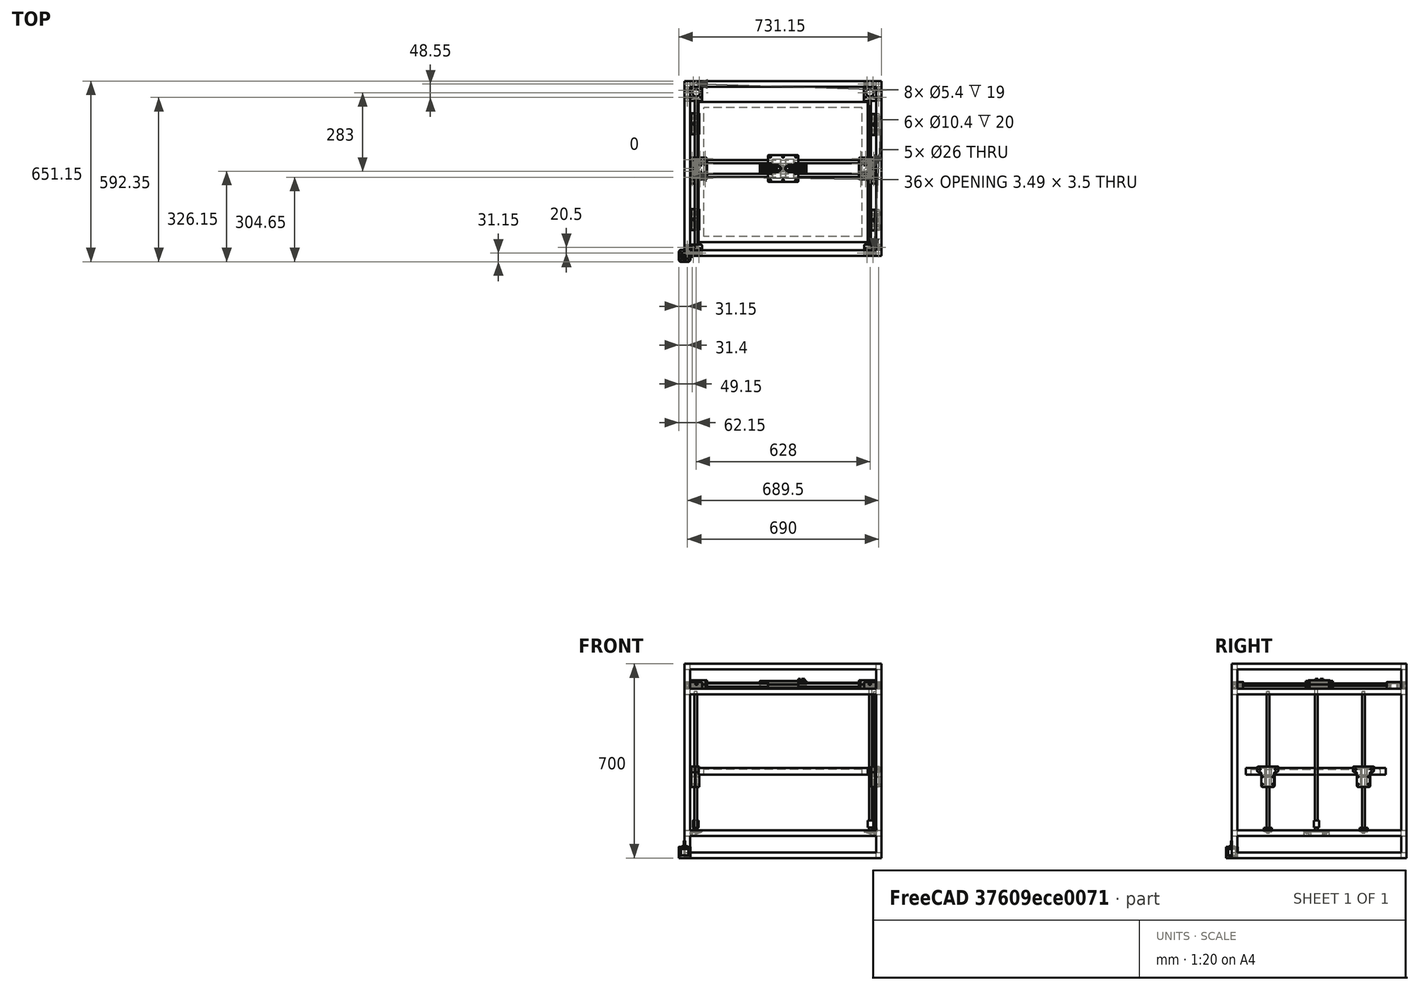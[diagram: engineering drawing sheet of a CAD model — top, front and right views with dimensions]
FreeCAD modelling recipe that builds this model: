
FCSTD DOCUMENT  (FreeCAD 0.17R13541 (Git))
Label: Modelo completo
License: All rights reserved
LicenseURL: http://en.wikipedia.org/wiki/All_rights_reserved
objects: Sketcher::SketchObject×105, Part::Cylinder×96, Part::Box×67, Part::Cut×63, Part::MultiFuse×62, Part::Prism×54, Part::FeaturePython×51, PartDesign::Pad×44, PartDesign::Pocket×44, PartDesign::Body×28, App::Part×28, Part::Fuse×24, Part::Extrusion×17, Part::Common×16, PartDesign::Chamfer×16, Part::Fillet×10, Part::Feature×10, PartDesign::Fillet×8, Part::Chamfer×5, Part::Mirroring×4, +5 more types
note: 832 computed .brp shape members not serialized (recipe doc carries the construction recipe); baked Part::Feature solids carry a one-line shape summary decoded from their .brp

FEATURE [Part::Box] Box  label="Columna"
  AttacherType = Attacher::AttachEngine3D
  Height = 700
  Length = 20
  Width = 20
FEATURE [Part::FeaturePython] Array  label="Columnas"  # Draft array (typed FeaturePython)
  Angle = 360
  ArrayType = 0
  Axis = (0,0,1)
  Base = -> Box
  Center = (0,0,0)
  Fuse = false
  IntervalAxis = (0,0,0)
  IntervalX = (690,0,0)
  IntervalY = (0,610,0)
  IntervalZ = (0,0,0)
  NumberPolar = 1
  NumberX = 2
  NumberY = 2
  NumberZ = 1
FEATURE [Part::Box] Box001  label="Laterales"
  AttacherType = Attacher::AttachEngine3D
  Height = 20
  Length = 20
  Placement = pos=(0,20,0) rot=(0,0,1;0rad)
  Width = 590
FEATURE [Part::Box] Box002  label="frontales"
  AttacherType = Attacher::AttachEngine3D
  Height = 20
  Length = 670
  Placement = pos=(20,0,0) rot=(0,0,1;0rad)
  Width = 20
FEATURE [Part::FeaturePython] Array001  label="Laterales inferiores"  # Draft array (typed FeaturePython)
  Angle = 360
  ArrayType = 0
  Axis = (0,0,1)
  Base = -> Box001
  Center = (0,0,0)
  Fuse = false
  IntervalAxis = (0,0,0)
  IntervalX = (690,0,0)
  IntervalY = (0,1,0)
  IntervalZ = (0,0,80)
  NumberPolar = 1
  NumberX = 2
  NumberY = 1
  NumberZ = 2
FEATURE [Part::Box] Box003  label="Laterales001"
  AttacherType = Attacher::AttachEngine3D
  Height = 20
  Length = 20
  Placement = pos=(0,20,0) rot=(0,0,1;0rad)
  Width = 590
FEATURE [Part::FeaturePython] Array002  label="Laterales Superiores"  # Draft array (typed FeaturePython)
  Angle = 360
  ArrayType = 0
  Axis = (0,0,1)
  Base = -> Box003
  Center = (0,0,0)
  Fuse = false
  IntervalAxis = (0,0,0)
  IntervalX = (690,0,0)
  IntervalY = (0,1,0)
  IntervalZ = (0,0,90)
  NumberPolar = 1
  NumberX = 2
  NumberY = 1
  NumberZ = 2
  Placement = pos=(0,0,590) rot=(0,0,1;0rad)
FEATURE [Part::FeaturePython] Array003  label="Frontales inferiores"  # Draft array (typed FeaturePython)
  Angle = 360
  ArrayType = 0
  Axis = (0,0,1)
  Base = -> Box002
  Center = (0,0,0)
  Fuse = false
  IntervalAxis = (0,0,0)
  IntervalX = (1,0,0)
  IntervalY = (0,610,0)
  IntervalZ = (0,0,80)
  NumberPolar = 1
  NumberX = 1
  NumberY = 2
  NumberZ = 2
FEATURE [Part::Box] Box004  label="frontales001"
  AttacherType = Attacher::AttachEngine3D
  Height = 20
  Length = 670
  Placement = pos=(20,0,0) rot=(0,0,1;0rad)
  Width = 20
FEATURE [Part::FeaturePython] Array004  label="Frontales superiores"  # Draft array (typed FeaturePython)
  Angle = 360
  ArrayType = 0
  Axis = (0,0,1)
  Base = -> Box004
  Center = (0,0,0)
  Fuse = false
  IntervalAxis = (0,0,0)
  IntervalX = (1,0,0)
  IntervalY = (0,610,0)
  IntervalZ = (0,0,90)
  NumberPolar = 1
  NumberX = 1
  NumberY = 2
  NumberZ = 2
  Placement = pos=(0,0,590) rot=(0,0,1;0rad)
FEATURE [Part::MultiFuse] Fusion  label="Estructura externa"
  Shapes = -> [Array,Array001,Array002,Array003,Array004]
FEATURE [Part::Cylinder] Cylinder  label="hueco_cabeza_tornillo"
  Angle = 360
  AttacherType = Attacher::AttachEngine3D
  Height = 35
  Placement = pos=(35,5,10) rot=(-1,0,0;1.5708rad)
  Radius = 5
FEATURE [Part::Box] Box005  label="soporte_vertical"
  AttacherType = Attacher::AttachEngine3D
  Height = 20
  Length = 28.5
  Placement = pos=(-50,0,0) rot=(0,0,1;0rad)
  Width = 5
FEATURE [Part::Box] Box006  label="Cubo"
  AttacherType = Attacher::AttachEngine3D
  Height = 20
  Length = 10
  Placement = pos=(45,0,0) rot=(0,0,1;0rad)
  Width = 20
FEATURE [Sketcher::SketchObject] Sketch002  label="sketch_refuerzo_triangular"
  MapMode = 5
  Placement = pos=(0,0,0) rot=(0.57735,0.57735,0.57735;2.0944rad)
  sketch-geometry (3):
    g0: LineSegment StartX=5 StartY=20 StartZ=0 EndX=42 EndY=6 EndZ=0
    g1: LineSegment StartX=42 StartY=6 StartZ=0 EndX=5 EndY=6 EndZ=0
    g2: LineSegment StartX=5 StartY=6 StartZ=0 EndX=5 EndY=20 EndZ=0
  constraints (9):
    c: Coincident(g0,g1)
    c: Horizontal(g1)
    c: Coincident(g1,g2)
    c: Coincident(g0,g2)
    c: Vertical(g2)
    c: DistanceX(g1,g0) = 37
    c: DistanceX(g-1,g1) = 5
    c: DistanceY(g-1,g1) = 6
    c: DistanceY(g-1,g0) = 20
FEATURE [Sketcher::SketchObject] Sketch  label="base_hueco_motor_sketch"
  MapMode = 5
  sketch-geometry (10):
    g0: LineSegment StartX=-30 StartY=42 StartZ=0 EndX=30 EndY=42 EndZ=0
    g1: LineSegment StartX=30 StartY=42 StartZ=0 EndX=50 EndY=0 EndZ=0
    g2: LineSegment StartX=50 StartY=0 StartZ=0 EndX=-50 EndY=0 EndZ=0
    g3: LineSegment StartX=-50 StartY=0 StartZ=0 EndX=-30 EndY=42 EndZ=0
    g4: Circle CenterX=-15.5 CenterY=36.5 CenterZ=0 NormalX=0 NormalY=0 NormalZ=1 AngleXU=0 Radius=1.65
    g5: Circle CenterX=15.5 CenterY=36.5 CenterZ=0 NormalX=0 NormalY=0 NormalZ=1 AngleXU=0 Radius=1.65
    g6: Circle CenterX=-15.5 CenterY=5.5 CenterZ=0 NormalX=0 NormalY=0 NormalZ=1 AngleXU=0 Radius=1.65
    g7: Circle CenterX=15.5 CenterY=5.5 CenterZ=0 NormalX=0 NormalY=0 NormalZ=1 AngleXU=0 Radius=1.65
    g8: GeomPoint [constr] X=0 Y=21 Z=0
    g9: Circle CenterX=0 CenterY=21 CenterZ=0 NormalX=0 NormalY=0 NormalZ=1 AngleXU=0 Radius=13
  constraints (28):
    c: Horizontal(g0)
    c: Coincident(g0,g1)
    c: Coincident(g1,g2)
    c: Horizontal(g2)
    c: Coincident(g2,g3)
    c: Coincident(g3,g0)
    c: DistanceY(g-1,g2) = 0
    c: DistanceX(g0,g-1) = 30
    c: DistanceX(g-1,g0) = 30
    c: DistanceX(g-1,g1) = 50
    c: DistanceX(g2,g-1) = 50
    c: DistanceY(g-1,g0) = 42
    c: Radius(g4) = 1.65  'M3'
    c: Equal(g4,g5)
    c: DistanceY(g4,g5) = 0
    c: DistanceX(g4,g5) = 31
    c: Equal(g4,g6)
    c: Equal(g7,g4)
    c: DistanceY(g6,g7) = 0
    c: DistanceX(g5,g7) = 0
    c: DistanceX(g6,g4) = 0
    c: DistanceY(g7,g5) = 31
    c: DistanceY(g-1,g8) = 21  'centro'
    c: DistanceX(g8,g-1) = 0
    c: DistanceX(g-1,g5) = 15.5
    c: DistanceY(g8,g5) = 15.5
    c: Coincident(g9,g8)
    c: Radius(g9) = 13
FEATURE [Sketcher::SketchObject] Sketch003  label="M5_repraphole"
  MapMode = 5
  Placement = pos=(0,0,10) rot=(1,0,0;1.5708rad)
  sketch-geometry (4):
    g0: ArcOfCircle CenterX=0 CenterY=0 CenterZ=0 NormalX=0 NormalY=0 NormalZ=1 AngleXU=0 Radius=2.68 StartAngle=2.3562 EndAngle=7.06858
    g1: LineSegment StartX=-1.89506 StartY=1.89504 StartZ=0 EndX=-1.11009 EndY=2.68 EndZ=0
    g2: LineSegment StartX=1.11009 StartY=2.68 StartZ=0 EndX=1.89506 EndY=1.89504 EndZ=0
    g3: LineSegment StartX=-1.11009 StartY=2.68 StartZ=0 EndX=1.11009 EndY=2.68 EndZ=0
  constraints (12):
    c: Coincident(g0,g-1)
    c: Radius(g0) = 2.68  'M5'
    c: Angle(g-1,g1) = 0.785398
    c: Horizontal(g3)
    c: Coincident(g3,g1)
    c: Coincident(g3,g2)
    c: Coincident(g0,g1)
    c: Coincident(g0,g2)
    c: DistanceY(g-1,g1) = 2.68  'M5radio'
    c: Angle(g2,g-1) = 0.785398
    c: Tangent(g2,g0)
    c: Tangent(g1,g0)
FEATURE [Part::Extrusion] Extrude002  label="M5_repraphole_extrusion"
  Base = -> Sketch003
  Dir = (0,10,0)
  DirMode = 0
  FaceMakerClass = Part::FaceMakerExtrusion
  LengthFwd = 0
  LengthRev = 0
  Placement = pos=(35,-1,0) rot=(0,0,1;0rad)
  Solid = true
  Symmetric = false
FEATURE [Part::Extrusion] Extrude001  label="refuerzo_triangular"
  Base = -> Sketch002
  Dir = (4.5,0,0)
  DirMode = 0
  FaceMakerClass = Part::FaceMakerExtrusion
  LengthFwd = 0
  LengthRev = 0
  Placement = pos=(21.5,0,0) rot=(0,0,1;0rad)
  Solid = true
  Symmetric = false
FEATURE [Part::FeaturePython] Clone001  label="refuerzo_triangular_2"  # Draft clone (typed FeaturePython)
  Objects = -> [Extrude001]
  Placement = pos=(-26,0,0) rot=(0,0,1;0rad)
  Scale = (1,1,1)
FEATURE [Part::FeaturePython] Clone  label="soporte_vertical_2"  # Draft clone (typed FeaturePython)
  Objects = -> [Box005]
  Placement = pos=(50,5,0) rot=(0,0,1;3.14159rad)
  Scale = (1,1,1)
FEATURE [Part::Cut] Cut001  label="soporte_vertical_contaladro_1"
  Base = -> Clone
  Tool = -> Extrude002
FEATURE [Part::FeaturePython] Clone003  label="hueco_cabeza_tornillo_2"  # Draft clone (typed FeaturePython)
  Objects = -> [Cylinder]
  Placement = pos=(-35,5,10) rot=(-1,0,0;1.5708rad)
  Scale = (1,1,1)
FEATURE [Part::FeaturePython] Clone004  label="Clone of Cubo"  # Draft clone (typed FeaturePython)
  Objects = -> [Box006]
  Placement = pos=(-55,0,0) rot=(0,0,1;0rad)
  Scale = (1,1,1)
FEATURE [Part::MultiFuse] Fusion002  label="cubos_recorte"
  Shapes = -> [Box006,Clone004]
FEATURE [Part::FeaturePython] Clone002  label="M5_repraphole_extrusion_2"  # Draft clone (typed FeaturePython)
  Objects = -> [Extrude002]
  Placement = pos=(-35,-1,0) rot=(0,0,1;0rad)
  Scale = (1,1,1)
FEATURE [Part::Cut] Cut  label="soporte_vertical_contaladro_2"
  Base = -> Box005
  Tool = -> Clone002
FEATURE [Part::Extrusion] Extrude  label="base_hueco_motor"
  Base = -> Sketch
  Dir = (0,0,6)
  DirMode = 0
  FaceMakerClass = Part::FaceMakerExtrusion
  LengthFwd = 0
  LengthRev = 0
  Solid = true
  Symmetric = false
FEATURE [Part::MultiFuse] Fusion003  label="huecos_cabeza_tornillo"
  Shapes = -> [Clone003,Cylinder]
FEATURE [Part::Cut] Cut002  label="base_hueco_motor_con_cabeza_tornillo"
  Base = -> Extrude
  Tool = -> Fusion003
FEATURE [Part::MultiFuse] Fusion001  label="nema17_holder"
  Shapes = -> [Extrude001,Cut,Cut001,Cut002,Clone001]
FEATURE [Part::Chamfer] Chamfer  label="nema17_holder_chaflan"
  Base = -> Fusion001
  Edges = 8 edges r=3: [Edge12,Edge13,Edge21,Edge24,Edge54,Edge55,Edge66,Edge67]
FEATURE [Part::Cut] Cut003  label="nema17_holder_recortado"
  Base = -> Chamfer
  Tool = -> Fusion002
FEATURE [Part::Fillet] Fillet  label="nema17_holder_v03"
  Base = -> Cut003
  Edges = 6 edges: [Edge10 r=2,Edge12 r=3,Edge16 r=3,Edge50 r=1,Edge76 r=2,Edge96 r=1]
  Placement = pos=(20,305,100) rot=(0.707107,0.707107,0;3.14159rad)
FEATURE [Part::Mirroring] mirror  label="Motor Z holder"
  Base = (355,315,100)
  Normal = (1,0,0)
  Source = -> Fillet
FEATURE [Part::Cylinder] Cylinder001  label="Tornillo sin fin"
  Angle = 360
  AttacherType = Attacher::AttachEngine3D
  Height = 510
  Placement = pos=(40,305,100) rot=(0,0,1;0rad)
  Radius = 5
FEATURE [Part::Cylinder] Cylinder002  label="conector tornillo sin fin y motor"
  Angle = 360
  AttacherType = Attacher::AttachEngine3D
  Height = 25
  Placement = pos=(40,305,110) rot=(0,0,1;0rad)
  Radius = 10
FEATURE [Part::MultiFuse] Fusion004
  Shapes = -> [Cylinder001,Cylinder002]
FEATURE [Part::Mirroring] mirror001  label="Mirror of Fusion004"
  Base = (355,315,0)
  Normal = (1,0,0)
  Source = -> Fusion004
FEATURE [Part::MultiFuse] Fusion005  label="tornillos y sujecciones Z"
  Shapes = -> [mirror,mirror001]
FEATURE [Part::Box] Box007  label="hueco_columna_z"
  AttacherType = Attacher::AttachEngine3D
  Height = 25
  Length = 20.5
  Width = 20.5
FEATURE [Part::Box] Box008  label="cubo_base"
  AttacherType = Attacher::AttachEngine3D
  Height = 25
  Length = 63.5
  Width = 71
FEATURE [Part::Cut] Cut004  label="cubo_base_sin_columna"
  Base = -> Box008
  Tool = -> Box007
FEATURE [Part::Box] Box009  label="hueco_motor"
  AttacherType = Attacher::AttachEngine3D
  Height = 20
  Length = 43
  Placement = pos=(20.5,20.5,5) rot=(0,0,1;0rad)
  Width = 42.3
FEATURE [Part::Chamfer] Chamfer001  label="hueco_motor_chaflan"
  Base = -> Box009
  Edges = 2 edges r=4: [Edge1,Edge3]
FEATURE [Sketcher::SketchObject] Sketch001  label="huecos_cabeza_tornillos"
  MapMode = 5
  sketch-geometry (4):
    g0: Circle CenterX=31.5 CenterY=10.25 CenterZ=0 NormalX=0 NormalY=0 NormalZ=1 AngleXU=0 Radius=5.2
    g1: Circle CenterX=52.5 CenterY=10.25 CenterZ=0 NormalX=0 NormalY=0 NormalZ=1 AngleXU=0 Radius=5.2
    g2: Circle CenterX=10.25 CenterY=32.5 CenterZ=0 NormalX=0 NormalY=0 NormalZ=1 AngleXU=0 Radius=5.2
    g3: Circle CenterX=10.25 CenterY=58.8 CenterZ=0 NormalX=0 NormalY=0 NormalZ=1 AngleXU=0 Radius=5.2
  constraints (12):
    c: DistanceY(g-1,g0) = 10.25
    c: Radius(g0) = 5.2
    c: DistanceX(g-1,g0) = 31.5
    c: DistanceY(g1,g0) = 0
    c: DistanceX(g1,g0) = -21
    c: Equal(g1,g0)
    c: DistanceX(g-1,g2) = 10.25
    c: Equal(g2,g0)
    c: DistanceY(g-1,g2) = 32.5
    c: DistanceX(g3,g2) = 0
    c: DistanceY(g3,g2) = -26.3
    c: Equal(g3,g2)
FEATURE [Sketcher::SketchObject] Sketch004
  MapMode = 5
  Placement = pos=(20.5,20.5,25) rot=(0,0,1;0rad)
  Support = -> [Box009]
  sketch-geometry (5):
    g0: Circle CenterX=21.5 CenterY=21.5 CenterZ=0 NormalX=0 NormalY=0 NormalZ=1 AngleXU=0 Radius=13
    g1: Circle CenterX=6 CenterY=37 CenterZ=0 NormalX=0 NormalY=0 NormalZ=1 AngleXU=0 Radius=1.65
    g2: Circle CenterX=37 CenterY=37 CenterZ=0 NormalX=0 NormalY=0 NormalZ=1 AngleXU=0 Radius=1.65
    g3: Circle CenterX=37 CenterY=6 CenterZ=0 NormalX=0 NormalY=0 NormalZ=1 AngleXU=0 Radius=1.65
    g4: Circle CenterX=6 CenterY=6 CenterZ=0 NormalX=0 NormalY=0 NormalZ=1 AngleXU=0 Radius=1.65
  constraints (15):
    c: DistanceY(g-1,g0) = 21.5
    c: DistanceX(g-1,g0) = 21.5
    c: Radius(g0) = 13
    c: DistanceX(g1,g0) = 15.5
    c: Radius(g1) = 1.65
    c: DistanceY(g2,g1) = 0
    c: DistanceY(g1,g0) = -15.5
    c: Equal(g2,g1)
    c: DistanceX(g2,g0) = -15.5
    c: DistanceX(g3,g2) = 0
    c: DistanceX(g4,g1) = 0
    c: DistanceY(g4,g3) = 0
    c: DistanceY(g3,g0) = 15.5
    c: Equal(g3,g2)
    c: Equal(g4,g3)
FEATURE [Part::Extrusion] Extrude003  label="agujero_motor"
  Base = -> Sketch004
  Dir = (0,0,5)
  DirMode = 0
  FaceMakerClass = Part::FaceMakerExtrusion
  LengthFwd = 0
  LengthRev = 0
  Placement = pos=(0,0,-25) rot=(0,0,1;0rad)
  Solid = true
  Symmetric = false
FEATURE [Part::MultiFuse] Fusion010  label="hueco_motor_total"
  Shapes = -> [Chamfer001,Extrude003]
FEATURE [Part::Cut] Cut006  label="base_sin_motor_columna"
  Base = -> Cut004
  Tool = -> Fusion010
FEATURE [Part::Extrusion] Extrude004  label="huecos_cabeza_tornillos_extr"
  Base = -> Sketch001
  Dir = (0,0,6)
  DirMode = 0
  FaceMakerClass = Part::FaceMakerExtrusion
  LengthFwd = 0
  LengthRev = 0
  Solid = true
  Symmetric = false
FEATURE [Sketcher::SketchObject] Sketch005  label="M10_repraphole"
  MapMode = 5
  Placement = pos=(0,0,0) rot=(0.57735,0.57735,0.57735;2.0944rad)
  sketch-geometry (4):
    g0: ArcOfCircle CenterX=0 CenterY=0 CenterZ=0 NormalX=0 NormalY=0 NormalZ=1 AngleXU=0 Radius=5.1 StartAngle=2.3562 EndAngle=7.06858
    g1: LineSegment StartX=-3.60626 StartY=3.60623 StartZ=0 EndX=-2.11249 EndY=5.1 EndZ=0
    g2: LineSegment StartX=2.11249 StartY=5.1 StartZ=0 EndX=3.60626 EndY=3.60623 EndZ=0
    g3: LineSegment StartX=-2.11249 StartY=5.1 StartZ=0 EndX=2.11249 EndY=5.1 EndZ=0
  constraints (12):
    c: Coincident(g0,g-1)
    c: Radius(g0) = 5.1  'M5'
    c: Angle(g-1,g1) = 0.785398
    c: Horizontal(g3)
    c: Coincident(g3,g1)
    c: Coincident(g3,g2)
    c: Coincident(g0,g1)
    c: Coincident(g0,g2)
    c: DistanceY(g-1,g1) = 5.1  'M5radio'
    c: Angle(g2,g-1) = 0.785398
    c: Tangent(g2,g0)
    c: Tangent(g1,g0)
FEATURE [Part::Extrusion] Extrude006  label="M10_repraphole_extr"
  Base = -> Sketch005
  Dir = (10,0,0)
  DirMode = 0
  FaceMakerClass = Part::FaceMakerExtrusion
  LengthFwd = 0
  LengthRev = 0
  Placement = pos=(42,62,10.2) rot=(0,0,1;1.5708rad)
  Solid = true
  Symmetric = false
FEATURE [Part::Prism] Prism001  label="hexagono_soporte"
  AttacherType = Attacher::AttachEngine3D
  Circumradius = 3.1
  Height = 0.3
  Placement = pos=(10.25,32.5,6.3) rot=(0,0,1;0.523599rad)
  Polygon = 6
FEATURE [Sketcher::SketchObject] Sketch006  label="huecos_tornillos"
  MapMode = 5
  sketch-geometry (4):
    g0: Circle CenterX=31.5 CenterY=10.25 CenterZ=0 NormalX=0 NormalY=0 NormalZ=1 AngleXU=0 Radius=2.7
    g1: Circle CenterX=52.5 CenterY=10.25 CenterZ=0 NormalX=0 NormalY=0 NormalZ=1 AngleXU=0 Radius=2.7
    g2: Circle CenterX=10.25 CenterY=32.5 CenterZ=0 NormalX=0 NormalY=0 NormalZ=1 AngleXU=0 Radius=2.7
    g3: Circle CenterX=10.25 CenterY=58.8 CenterZ=0 NormalX=0 NormalY=0 NormalZ=1 AngleXU=0 Radius=2.7
  constraints (12):
    c: DistanceY(g-1,g0) = 10.25
    c: Radius(g0) = 2.7
    c: DistanceX(g-1,g0) = 31.5
    c: DistanceY(g1,g0) = 0
    c: DistanceX(g1,g0) = -21
    c: Equal(g1,g0)
    c: DistanceX(g-1,g2) = 10.25
    c: Equal(g2,g0)
    c: DistanceY(g-1,g2) = 32.5
    c: DistanceX(g3,g2) = 0
    c: DistanceY(g3,g2) = -26.3
    c: Equal(g3,g2)
FEATURE [Part::Extrusion] Extrude005  label="huecos_tornillos_extr"
  Base = -> Sketch006
  Dir = (0,0,25)
  DirMode = 0
  FaceMakerClass = Part::FaceMakerExtrusion
  LengthFwd = 0
  LengthRev = 0
  Solid = true
  Symmetric = false
FEATURE [Part::MultiFuse] Fusion006  label="huecos_tornillos_todo"
  Shapes = -> [Extrude004,Extrude005]
FEATURE [Part::Prism] Prism  label="triangulo_soporte"
  AttacherType = Attacher::AttachEngine3D
  Circumradius = 5.3
  Height = 0.3
  Placement = pos=(10.25,32.5,6) rot=(0,0,1;0rad)
  Polygon = 3
FEATURE [Part::MultiFuse] Fusion007  label="soporte_circulos"
  Shapes = -> [Prism,Prism001]
FEATURE [Part::FeaturePython] Clone006  label="soporte_circulos_2"  # Draft clone (typed FeaturePython)
  Objects = -> [Fusion007]
  Placement = pos=(0,26.3,0) rot=(0,0,1;0rad)
  Scale = (1,1,1)
FEATURE [Part::FeaturePython] Clone007  label="soporte_circulos_3"  # Draft clone (typed FeaturePython)
  Objects = -> [Fusion007]
  Placement = pos=(21.25,-22.25,0) rot=(0,0,1;0rad)
  Scale = (1,1,1)
FEATURE [Part::FeaturePython] Clone005  label="soporte_circulos_4"  # Draft clone (typed FeaturePython)
  Objects = -> [Clone007]
  Placement = pos=(42.25,-22.25,0) rot=(0,0,1;0rad)
  Scale = (1,1,1)
FEATURE [Part::MultiFuse] Fusion008  label="huecos_soporte_taladros"
  Shapes = -> [Fusion007,Clone006,Clone007,Clone005]
FEATURE [Part::MultiFuse] Fusion009  label="huecos_2"
  Shapes = -> [Fusion006,Extrude006,Fusion008]
FEATURE [Part::Cut] Cut005  label="YmotorLeft_casi"
  Base = -> Cut006
  Tool = -> Fusion009
FEATURE [Part::Chamfer] Chamfer002  label="YmotorLeft_chaflan"
  Base = -> Cut005
  Edges = 2 edges: [Edge10 r=16,Edge13 r=3]
FEATURE [Part::Fillet] Fillet001  label="YmotorLeft"
  Base = -> Chamfer002
  Edges = 5 edges: [Edge17 r=2,Edge20 r=2,Edge27 r=1,Edge40 r=1,Edge44 r=2]
  Placement = pos=(0,630,635) rot=(1,0,0;3.14159rad)
FEATURE [Part::Prism] Prism002  label="triangulo_soporte001"
  AttacherType = Attacher::AttachEngine3D
  Circumradius = 5.3
  Height = 0.3
  Placement = pos=(10.25,32.5,6) rot=(0,0,1;0rad)
  Polygon = 3
FEATURE [Part::Prism] Prism003  label="hexagono_soporte001"
  AttacherType = Attacher::AttachEngine3D
  Circumradius = 3.1
  Height = 0.3
  Placement = pos=(10.25,32.5,6.3) rot=(0,0,1;0.523599rad)
  Polygon = 6
FEATURE [Part::Box] Box010  label="hueco_motor001"
  AttacherType = Attacher::AttachEngine3D
  Height = 20
  Length = 43
  Placement = pos=(20.5,20.5,5) rot=(0,0,1;0rad)
  Width = 42.3
FEATURE [Part::Box] Box011  label="hueco_columna_z001"
  AttacherType = Attacher::AttachEngine3D
  Height = 25
  Length = 20.5
  Width = 20.5
FEATURE [Part::Box] Box012  label="cubo_base001"
  AttacherType = Attacher::AttachEngine3D
  Height = 25
  Length = 63.5
  Width = 71
FEATURE [Part::Chamfer] Chamfer003  label="hueco_motor_chaflan001"
  Base = -> Box010
  Edges = 2 edges r=4: [Edge1,Edge3]
FEATURE [Part::Cut] Cut008  label="cubo_base_sin_columna001"
  Base = -> Box012
  Tool = -> Box011
FEATURE [Part::MultiFuse] Fusion012  label="soporte_circulos001"
  Shapes = -> [Prism002,Prism003]
FEATURE [Part::FeaturePython] Clone008  label="soporte_circulos_005"  # Draft clone (typed FeaturePython)
  Objects = -> [Fusion012]
  Placement = pos=(21.25,-22.25,0) rot=(0,0,1;0rad)
  Scale = (1,1,1)
FEATURE [Part::FeaturePython] Clone009  label="soporte_circulos_006"  # Draft clone (typed FeaturePython)
  Objects = -> [Fusion012]
  Placement = pos=(0,26.3,0) rot=(0,0,1;0rad)
  Scale = (1,1,1)
FEATURE [Part::FeaturePython] Clone010  label="soporte_circulos_007"  # Draft clone (typed FeaturePython)
  Objects = -> [Clone008]
  Placement = pos=(42.25,-22.25,0) rot=(0,0,1;0rad)
  Scale = (1,1,1)
FEATURE [Part::MultiFuse] Fusion013  label="huecos_soporte_taladros001"
  Shapes = -> [Fusion012,Clone009,Clone008,Clone010]
FEATURE [Sketcher::SketchObject] Sketch007
  MapMode = 5
  Placement = pos=(20.5,20.5,25) rot=(0,0,1;0rad)
  Support = -> [Box010]
  sketch-geometry (5):
    g0: Circle CenterX=21.5 CenterY=21.5 CenterZ=0 NormalX=0 NormalY=0 NormalZ=1 AngleXU=0 Radius=13
    g1: Circle CenterX=6 CenterY=37 CenterZ=0 NormalX=0 NormalY=0 NormalZ=1 AngleXU=0 Radius=1.65
    g2: Circle CenterX=37 CenterY=37 CenterZ=0 NormalX=0 NormalY=0 NormalZ=1 AngleXU=0 Radius=1.65
    g3: Circle CenterX=37 CenterY=6 CenterZ=0 NormalX=0 NormalY=0 NormalZ=1 AngleXU=0 Radius=1.65
    g4: Circle CenterX=6 CenterY=6 CenterZ=0 NormalX=0 NormalY=0 NormalZ=1 AngleXU=0 Radius=1.65
  constraints (15):
    c: DistanceY(g-1,g0) = 21.5
    c: DistanceX(g-1,g0) = 21.5
    c: Radius(g0) = 13
    c: DistanceX(g1,g0) = 15.5
    c: Radius(g1) = 1.65
    c: DistanceY(g2,g1) = 0
    c: DistanceY(g1,g0) = -15.5
    c: Equal(g2,g1)
    c: DistanceX(g2,g0) = -15.5
    c: DistanceX(g3,g2) = 0
    c: DistanceX(g4,g1) = 0
    c: DistanceY(g4,g3) = 0
    c: DistanceY(g3,g0) = 15.5
    c: Equal(g3,g2)
    c: Equal(g4,g3)
FEATURE [Sketcher::SketchObject] Sketch008  label="huecos_cabeza_tornillos001"
  MapMode = 5
  sketch-geometry (4):
    g0: Circle CenterX=31.5 CenterY=10.25 CenterZ=0 NormalX=0 NormalY=0 NormalZ=1 AngleXU=0 Radius=5.2
    g1: Circle CenterX=52.5 CenterY=10.25 CenterZ=0 NormalX=0 NormalY=0 NormalZ=1 AngleXU=0 Radius=5.2
    g2: Circle CenterX=10.25 CenterY=32.5 CenterZ=0 NormalX=0 NormalY=0 NormalZ=1 AngleXU=0 Radius=5.2
    g3: Circle CenterX=10.25 CenterY=58.8 CenterZ=0 NormalX=0 NormalY=0 NormalZ=1 AngleXU=0 Radius=5.2
  constraints (12):
    c: DistanceY(g-1,g0) = 10.25
    c: Radius(g0) = 5.2
    c: DistanceX(g-1,g0) = 31.5
    c: DistanceY(g1,g0) = 0
    c: DistanceX(g1,g0) = -21
    c: Equal(g1,g0)
    c: DistanceX(g-1,g2) = 10.25
    c: Equal(g2,g0)
    c: DistanceY(g-1,g2) = 32.5
    c: DistanceX(g3,g2) = 0
    c: DistanceY(g3,g2) = -26.3
    c: Equal(g3,g2)
FEATURE [Part::Extrusion] Extrude007  label="agujero_motor001"
  Base = -> Sketch007
  Dir = (0,0,5)
  DirMode = 0
  FaceMakerClass = Part::FaceMakerExtrusion
  LengthFwd = 0
  LengthRev = 0
  Placement = pos=(0,0,-25) rot=(0,0,1;0rad)
  Solid = true
  Symmetric = false
FEATURE [Part::MultiFuse] Fusion011  label="hueco_motor_total001"
  Shapes = -> [Chamfer003,Extrude007]
FEATURE [Part::Cut] Cut007  label="base_sin_motor_columna001"
  Base = -> Cut008
  Tool = -> Fusion011
FEATURE [Part::Extrusion] Extrude009  label="huecos_cabeza_tornillos_extr001"
  Base = -> Sketch008
  Dir = (0,0,6)
  DirMode = 0
  FaceMakerClass = Part::FaceMakerExtrusion
  LengthFwd = 0
  LengthRev = 0
  Solid = true
  Symmetric = false
FEATURE [Sketcher::SketchObject] Sketch009  label="huecos_tornillos001"
  MapMode = 5
  sketch-geometry (4):
    g0: Circle CenterX=31.5 CenterY=10.25 CenterZ=0 NormalX=0 NormalY=0 NormalZ=1 AngleXU=0 Radius=2.7
    g1: Circle CenterX=52.5 CenterY=10.25 CenterZ=0 NormalX=0 NormalY=0 NormalZ=1 AngleXU=0 Radius=2.7
    g2: Circle CenterX=10.25 CenterY=32.5 CenterZ=0 NormalX=0 NormalY=0 NormalZ=1 AngleXU=0 Radius=2.7
    g3: Circle CenterX=10.25 CenterY=58.8 CenterZ=0 NormalX=0 NormalY=0 NormalZ=1 AngleXU=0 Radius=2.7
  constraints (12):
    c: DistanceY(g-1,g0) = 10.25
    c: Radius(g0) = 2.7
    c: DistanceX(g-1,g0) = 31.5
    c: DistanceY(g1,g0) = 0
    c: DistanceX(g1,g0) = -21
    c: Equal(g1,g0)
    c: DistanceX(g-1,g2) = 10.25
    c: Equal(g2,g0)
    c: DistanceY(g-1,g2) = 32.5
    c: DistanceX(g3,g2) = 0
    c: DistanceY(g3,g2) = -26.3
    c: Equal(g3,g2)
FEATURE [Part::Extrusion] Extrude010  label="huecos_tornillos_extr001"
  Base = -> Sketch009
  Dir = (0,0,25)
  DirMode = 0
  FaceMakerClass = Part::FaceMakerExtrusion
  LengthFwd = 0
  LengthRev = 0
  Solid = true
  Symmetric = false
FEATURE [Part::MultiFuse] Fusion015  label="huecos_tornillos_todo001"
  Shapes = -> [Extrude009,Extrude010]
FEATURE [Sketcher::SketchObject] Sketch010  label="M10_repraphole001"
  MapMode = 5
  Placement = pos=(0,0,0) rot=(0.57735,0.57735,0.57735;2.0944rad)
  sketch-geometry (4):
    g0: ArcOfCircle CenterX=0 CenterY=0 CenterZ=0 NormalX=0 NormalY=0 NormalZ=1 AngleXU=0 Radius=5.1 StartAngle=2.3562 EndAngle=7.06858
    g1: LineSegment StartX=-3.60626 StartY=3.60623 StartZ=0 EndX=-2.11249 EndY=5.1 EndZ=0
    g2: LineSegment StartX=2.11249 StartY=5.1 StartZ=0 EndX=3.60626 EndY=3.60623 EndZ=0
    g3: LineSegment StartX=-2.11249 StartY=5.1 StartZ=0 EndX=2.11249 EndY=5.1 EndZ=0
  constraints (12):
    c: Coincident(g0,g-1)
    c: Radius(g0) = 5.1  'M5'
    c: Angle(g-1,g1) = 0.785398
    c: Horizontal(g3)
    c: Coincident(g3,g1)
    c: Coincident(g3,g2)
    c: Coincident(g0,g1)
    c: Coincident(g0,g2)
    c: DistanceY(g-1,g1) = 5.1  'M5radio'
    c: Angle(g2,g-1) = 0.785398
    c: Tangent(g2,g0)
    c: Tangent(g1,g0)
FEATURE [Part::Extrusion] Extrude008  label="M10_repraphole_extr001"
  Base = -> Sketch010
  Dir = (10,0,0)
  DirMode = 0
  FaceMakerClass = Part::FaceMakerExtrusion
  LengthFwd = 0
  LengthRev = 0
  Placement = pos=(42,62,10.2) rot=(0,0,1;1.5708rad)
  Solid = true
  Symmetric = false
FEATURE [Part::MultiFuse] Fusion014  label="huecos_003"
  Shapes = -> [Fusion015,Extrude008,Fusion013]
FEATURE [Part::Cut] Cut009  label="YmotorLeft_casi001"
  Base = -> Cut007
  Tool = -> Fusion014
FEATURE [Part::Chamfer] Chamfer004  label="YmotorLeft_chaflan001"
  Base = -> Cut009
  Edges = 2 edges: [Edge10 r=16,Edge13 r=3]
FEATURE [Part::Fillet] Fillet002  label="YmotorLeft001"
  Base = -> Chamfer004
  Edges = 5 edges: [Edge17 r=2,Edge20 r=2,Edge27 r=1,Edge40 r=1,Edge44 r=2]
FEATURE [Part::Mirroring] Part__Mirroring  label="YmotorRight"
  Base = (0,0,0)
  Normal = (0,1,0)
  Placement = pos=(710,630,635) rot=(0,1,0;3.14159rad)
  Source = -> Fillet002
FEATURE [Part::Cylinder] Cylinder003  label="taladro_endstop"
  Angle = 360
  AttacherType = Attacher::AttachEngine3D
  Height = 7
  Placement = pos=(35.5,26.14,12) rot=(0,0,1;0rad)
  Radius = 1.05
FEATURE [Part::FeaturePython] Clone011  label="taladro_endstop_2"  # Draft clone (typed FeaturePython)
  Objects = -> [Cylinder003]
  Placement = pos=(35.5,33.14,12) rot=(0,0,1;0rad)
  Scale = (1,1,1)
FEATURE [Part::Cylinder] Cylinder004  label="taladro4"
  Angle = 360
  AttacherType = Attacher::AttachEngine3D
  Height = 5
  Placement = pos=(10,42.7,20) rot=(0,0,1;0rad)
  Radius = 2.1
FEATURE [Part::FeaturePython] Clone012  label="taladro4_2"  # Draft clone (typed FeaturePython)
  Objects = -> [Cylinder004]
  Placement = pos=(25.5,55.8,20) rot=(0,0,1;0rad)
  Scale = (1,1,1)
FEATURE [Part::Cylinder] Cylinder005  label="taladro5"
  Angle = 360
  AttacherType = Attacher::AttachEngine3D
  Height = 5
  Placement = pos=(30.5,10,0) rot=(0,0,1;0rad)
  Radius = 2.65
FEATURE [Part::FeaturePython] Clone014  label="taladro5_2"  # Draft clone (typed FeaturePython)
  Objects = -> [Cylinder005]
  Placement = pos=(10,31,0) rot=(0,0,1;0rad)
  Scale = (1,1,1)
FEATURE [Part::FeaturePython] Clone016  label="taladro5_3"  # Draft clone (typed FeaturePython)
  Objects = -> [Clone014]
  Placement = pos=(10,52.3,0) rot=(0,0,1;0rad)
  Scale = (1,1,1)
FEATURE [Part::Box] Box013  label="hueco_taladro4"
  AttacherType = Attacher::AttachEngine3D
  Height = 6
  Length = 15
  Placement = pos=(0,39,14) rot=(0,0,1;0rad)
  Width = 7.5
FEATURE [Part::Box] Box014  label="hueco_endstop"
  AttacherType = Attacher::AttachEngine3D
  Height = 6
  Length = 13
  Placement = pos=(27.5,23.14,19) rot=(0,0,1;0rad)
  Width = 13
FEATURE [Part::Box] Box015  label="hueco_ejez"
  AttacherType = Attacher::AttachEngine3D
  Height = 25
  Length = 20.5
  Width = 20.5
FEATURE [Part::Cylinder] Cylinder006  label="taladro10"
  Angle = 360
  AttacherType = Attacher::AttachEngine3D
  Height = 20
  Placement = pos=(30.5,10,5) rot=(0,0,1;0rad)
  Radius = 5.2
FEATURE [Part::FeaturePython] Clone015  label="taladro10_2"  # Draft clone (typed FeaturePython)
  Objects = -> [Cylinder006]
  Placement = pos=(10,31,5) rot=(0,0,1;0rad)
  Scale = (1,1,1)
FEATURE [Part::FeaturePython] Clone013  label="taladro10_3"  # Draft clone (typed FeaturePython)
  Objects = -> [Clone015]
  Placement = pos=(10,52.3,5) rot=(0,0,1;0rad)
  Scale = (1,1,1)
FEATURE [Part::Box] Box016  label="hueco_taladro4_2"
  AttacherType = Attacher::AttachEngine3D
  Height = 6
  Length = 7.5
  Placement = pos=(21.75,49.8,14) rot=(0,0,1;0rad)
  Width = 13
FEATURE [Part::MultiFuse] Fusion016  label="huecos"
  Shapes = -> [Box016,Box013,Clone012,Cylinder004,Clone011,Cylinder003,Box014,Clone016,Clone014,Cylinder005,Clone013,Clone015,Cylinder006,Box015]
FEATURE [Part::Box] Box017  label="cubo_base002"
  AttacherType = Attacher::AttachEngine3D
  Height = 25
  Length = 40.5
  Width = 62.8
FEATURE [Part::Cut] Cut011  label="Yidler_right_ahuecado"
  Base = -> Box017
  Tool = -> Fusion016
FEATURE [Sketcher::SketchObject] Sketch011  label="M10_repraphole002"
  MapMode = 5
  Placement = pos=(0,0,0) rot=(0.57735,0.57735,0.57735;2.0944rad)
  sketch-geometry (4):
    g0: ArcOfCircle CenterX=0 CenterY=0 CenterZ=0 NormalX=0 NormalY=0 NormalZ=1 AngleXU=0 Radius=5.1 StartAngle=2.35619 EndAngle=7.06858
    g1: LineSegment StartX=-3.60624 StartY=3.60625 StartZ=0 EndX=-2.11249 EndY=5.1 EndZ=0
    g2: LineSegment StartX=2.11249 StartY=5.1 StartZ=0 EndX=3.60624 EndY=3.60625 EndZ=0
    g3: LineSegment StartX=-2.11249 StartY=5.1 StartZ=0 EndX=2.11249 EndY=5.1 EndZ=0
  constraints (12):
    c: Coincident(g0,g-1)
    c: Radius(g0) = 5.1  'M10'
    c: Angle(g-1,g1) = 0.785398
    c: Horizontal(g3)
    c: Coincident(g3,g1)
    c: Coincident(g3,g2)
    c: Coincident(g0,g1)
    c: Coincident(g0,g2)
    c: DistanceY(g-1,g1) = 5.1  'M10radio'
    c: Angle(g2,g-1) = 0.785398
    c: Tangent(g2,g0)
    c: Tangent(g1,g0)
FEATURE [Part::Extrusion] Extrude011  label="M10_repraphole_extrud"
  Base = -> Sketch011
  Dir = (20,0,0)
  DirMode = 0
  FaceMakerClass = Part::FaceMakerExtrusion
  LengthFwd = 0
  LengthRev = 0
  Placement = pos=(20.5,41.65,15) rot=(0,0,1;0rad)
  Solid = true
  Symmetric = false
FEATURE [Part::Cut] Cut010  label="Yidler_right_ahuecado2"
  Base = -> Cut011
  Tool = -> Extrude011
FEATURE [Part::Fillet] Fillet003  label="Yidler_right"
  Base = -> Cut010
  Edges = 5 edges: [Edge1 r=1,Edge3 r=3,Edge26 r=3,Edge46 r=1,Edge47 r=3]
  Placement = pos=(710,0,610) rot=(0,0,1;1.5708rad)
FEATURE [Part::Box] Box018  label="hueco_endstop001"
  AttacherType = Attacher::AttachEngine3D
  Height = 6
  Length = 13
  Placement = pos=(27.5,23.14,19) rot=(0,0,1;0rad)
  Width = 13
FEATURE [Part::Box] Box019  label="cubo_base003"
  AttacherType = Attacher::AttachEngine3D
  Height = 25
  Length = 40.5
  Width = 62.8
FEATURE [Part::Cylinder] Cylinder007  label="taladro011"
  Angle = 360
  AttacherType = Attacher::AttachEngine3D
  Height = 20
  Placement = pos=(30.5,10,5) rot=(0,0,1;0rad)
  Radius = 5.2
FEATURE [Part::FeaturePython] Clone018  label="taladro10_004"  # Draft clone (typed FeaturePython)
  Objects = -> [Cylinder007]
  Placement = pos=(10,31,5) rot=(0,0,1;0rad)
  Scale = (1,1,1)
FEATURE [Part::FeaturePython] Clone020  label="taladro10_005"  # Draft clone (typed FeaturePython)
  Objects = -> [Clone018]
  Placement = pos=(10,52.3,5) rot=(0,0,1;0rad)
  Scale = (1,1,1)
FEATURE [Part::Box] Box020  label="hueco_taladro005"
  AttacherType = Attacher::AttachEngine3D
  Height = 6
  Length = 15
  Placement = pos=(0,39,14) rot=(0,0,1;0rad)
  Width = 7.5
FEATURE [Part::Box] Box021  label="hueco_ejez001"
  AttacherType = Attacher::AttachEngine3D
  Height = 25
  Length = 20.5
  Width = 20.5
FEATURE [Part::Cylinder] Cylinder008  label="taladro012"
  Angle = 360
  AttacherType = Attacher::AttachEngine3D
  Height = 5
  Placement = pos=(30.5,10,0) rot=(0,0,1;0rad)
  Radius = 2.65
FEATURE [Part::FeaturePython] Clone021  label="taladro5_005"  # Draft clone (typed FeaturePython)
  Objects = -> [Cylinder008]
  Placement = pos=(10,31,0) rot=(0,0,1;0rad)
  Scale = (1,1,1)
FEATURE [Part::FeaturePython] Clone017  label="taladro5_004"  # Draft clone (typed FeaturePython)
  Objects = -> [Clone021]
  Placement = pos=(10,52.3,0) rot=(0,0,1;0rad)
  Scale = (1,1,1)
FEATURE [Part::Cylinder] Cylinder009  label="taladro_endstop001"
  Angle = 360
  AttacherType = Attacher::AttachEngine3D
  Height = 7
  Placement = pos=(35.5,26.14,12) rot=(0,0,1;0rad)
  Radius = 1.05
FEATURE [Part::FeaturePython] Clone022  label="taladro_endstop_003"  # Draft clone (typed FeaturePython)
  Objects = -> [Cylinder009]
  Placement = pos=(35.5,33.14,12) rot=(0,0,1;0rad)
  Scale = (1,1,1)
FEATURE [Part::Box] Box022  label="hueco_taladro4_003"
  AttacherType = Attacher::AttachEngine3D
  Height = 6
  Length = 7.5
  Placement = pos=(21.75,49.8,14) rot=(0,0,1;0rad)
  Width = 13
FEATURE [Part::Cylinder] Cylinder010  label="taladro013"
  Angle = 360
  AttacherType = Attacher::AttachEngine3D
  Height = 5
  Placement = pos=(10,42.7,20) rot=(0,0,1;0rad)
  Radius = 2.1
FEATURE [Part::FeaturePython] Clone019  label="taladro4_003"  # Draft clone (typed FeaturePython)
  Objects = -> [Cylinder010]
  Placement = pos=(25.5,55.8,20) rot=(0,0,1;0rad)
  Scale = (1,1,1)
FEATURE [Part::MultiFuse] Fusion017  label="huecos001"
  Shapes = -> [Box022,Box020,Clone019,Cylinder010,Clone022,Cylinder009,Box018,Clone017,Clone021,Cylinder008,Clone020,Clone018,Cylinder007,Box021]
FEATURE [Part::Cut] Cut012  label="Yidler_right_ahuecado003"
  Base = -> Box019
  Tool = -> Fusion017
FEATURE [Sketcher::SketchObject] Sketch012  label="M10_repraphole003"
  MapMode = 5
  Placement = pos=(0,0,0) rot=(0.57735,0.57735,0.57735;2.0944rad)
  sketch-geometry (4):
    g0: ArcOfCircle CenterX=0 CenterY=0 CenterZ=0 NormalX=0 NormalY=0 NormalZ=1 AngleXU=0 Radius=5.1 StartAngle=2.35619 EndAngle=7.06858
    g1: LineSegment StartX=-3.60624 StartY=3.60625 StartZ=0 EndX=-2.11249 EndY=5.1 EndZ=0
    g2: LineSegment StartX=2.11249 StartY=5.1 StartZ=0 EndX=3.60624 EndY=3.60625 EndZ=0
    g3: LineSegment StartX=-2.11249 StartY=5.1 StartZ=0 EndX=2.11249 EndY=5.1 EndZ=0
  constraints (12):
    c: Coincident(g0,g-1)
    c: Radius(g0) = 5.1  'M10'
    c: Angle(g-1,g1) = 0.785398
    c: Horizontal(g3)
    c: Coincident(g3,g1)
    c: Coincident(g3,g2)
    c: Coincident(g0,g1)
    c: Coincident(g0,g2)
    c: DistanceY(g-1,g1) = 5.1  'M10radio'
    c: Angle(g2,g-1) = 0.785398
    c: Tangent(g2,g0)
    c: Tangent(g1,g0)
FEATURE [Part::Extrusion] Extrude012  label="M10_repraphole_extrud001"
  Base = -> Sketch012
  Dir = (20,0,0)
  DirMode = 0
  FaceMakerClass = Part::FaceMakerExtrusion
  LengthFwd = 0
  LengthRev = 0
  Placement = pos=(20.5,41.65,15) rot=(0,0,1;0rad)
  Solid = true
  Symmetric = false
FEATURE [Part::Cut] Cut013  label="Yidler_right_ahuecado004"
  Base = -> Cut012
  Tool = -> Extrude012
FEATURE [Part::Fillet] Fillet004  label="Yidler_right001"
  Base = -> Cut013
  Edges = 5 edges: [Edge1 r=1,Edge3 r=3,Edge26 r=3,Edge46 r=1,Edge47 r=3]
FEATURE [Part::Mirroring] Part__Mirroring001  label="Yidler_left"
  Base = (0,0,0)
  Normal = (0,1,0)
  Placement = pos=(0,0,610) rot=(0,0,1;1.5708rad)
  Source = -> Fillet004
FEATURE [Part::Fuse] Fusion018
  Base = -> Fillet003
  Tool = -> Part__Mirroring001
FEATURE [Part::MultiFuse] Fusion019
  Shapes = -> [Part__Mirroring,Fillet001]
FEATURE [Part::MultiFuse] Fusion020  label="Soportes motores XY"
  Shapes = -> [Fusion018,Fusion019]
FEATURE [Part::Box] Box023  label="Cubo005"
  AttacherType = Attacher::AttachEngine3D
  Height = 20
  Length = 20
  Placement = pos=(485,20,0) rot=(0,0,1;0rad)
  Width = 570
FEATURE [Part::Box] Box024  label="Cubo006"
  AttacherType = Attacher::AttachEngine3D
  Height = 5
  Length = 505
  Placement = pos=(0,0,20) rot=(0,0,1;0rad)
  Width = 610
FEATURE [Part::Box] Box025  label="Cubo002"
  AttacherType = Attacher::AttachEngine3D
  Height = 20
  Length = 505
  Width = 20
FEATURE [Part::Box] Box026  label="Cubo003"
  AttacherType = Attacher::AttachEngine3D
  Height = 20
  Length = 20
  Placement = pos=(0,20,0) rot=(0,0,1;0rad)
  Width = 570
FEATURE [Part::MultiFuse] Fusion021
  Shapes = -> [Box026,Box023]
FEATURE [Part::Box] Box027  label="Cubo004"
  AttacherType = Attacher::AttachEngine3D
  Height = 20
  Length = 505
  Placement = pos=(0,590,0) rot=(0,0,1;0rad)
  Width = 20
FEATURE [Part::FeaturePython] BooleanFragments  # WARN: FeaturePython — macro-defined, semantics opaque (R4)
  Mode = 0
  Objects = -> [Box025,Box027]
  Tolerance = 0
FEATURE [Part::MultiFuse] Fusion022
  Shapes = -> [BooleanFragments,Fusion021]
FEATURE [Part::MultiFuse] Fusion023  label="Cama"
  Placement = pos=(660,50,300) rot=(0,0,1;1.5708rad)
  Shapes = -> [Fusion022,Box024]
FEATURE [Part::Polygon] gt2clamp0base_plane_yz
  Close = true
  Nodes = (12) [(0,2.60417,0),(0,2.60417,2.34375),(0,0,4.94792),(0,0,7.55208),(0,2.60417,10.1562),(0,2.60417,12.5),(0,13.4042,12.5),(0,13.4042,10.1562),+4 more]
FEATURE [Part::Cylinder] extr_outup
  Angle = 360
  AttacherType = Attacher::AttachEngine3D
  Height = 3.7
  Placement = pos=(0,0,8) rot=(0,0,1;0rad)
  Radius = 8.2
FEATURE [Part::Cylinder] extr_outup_2
  Angle = 360
  AttacherType = Attacher::AttachEngine3D
  Height = 3.7
  Placement = pos=(0,0,8) rot=(0,0,1;0rad)
  Radius = 8.2
FEATURE [Part::Box] extr_hold_tab0_hole
  AttacherType = Attacher::AttachEngine3D
  Height = 7.05
  Length = 13.24
  Placement = pos=(-40.5,0,5.65) rot=(0,0,1;0rad)
  Width = 12.8
FEATURE [Part::Box] extr_hold_tab2
  AttacherType = Attacher::AttachEngine3D
  Height = 5.65
  Length = 11.84
  Placement = pos=(27.66,-11.8,6.05) rot=(0,0,1;0rad)
  Width = 12.8
FEATURE [Part::Box] extr_hold_tab2_hole
  AttacherType = Attacher::AttachEngine3D
  Height = 7.05
  Length = 13.24
  Placement = pos=(27.26,-12.8,5.65) rot=(0,0,1;0rad)
  Width = 12.8
FEATURE [Part::Box] extr_hold_2
  AttacherType = Attacher::AttachEngine3D
  Height = 11.7
  Length = 79
  Placement = pos=(-39.5,-11.8,0) rot=(0,0,1;0rad)
  Width = 11.8
FEATURE [Part::Cylinder] extr_outbot
  Angle = 360
  AttacherType = Attacher::AttachEngine3D
  Height = 3.4
  Placement = pos=(0,0,-1) rot=(0,0,1;0rad)
  Radius = 8.2
FEATURE [Part::Box] extr_hold_tab1_hole
  AttacherType = Attacher::AttachEngine3D
  Height = 7.05
  Length = 13.24
  Placement = pos=(-40.5,-12.8,-1) rot=(0,0,1;0rad)
  Width = 12.8
FEATURE [Part::MultiFuse] extr_hold2_holes_joint
  Shapes = -> [extr_hold_tab1_hole,extr_hold_tab2_hole]
FEATURE [Part::Cylinder] extr_outbot_2
  Angle = 360
  AttacherType = Attacher::AttachEngine3D
  Height = 3.4
  Placement = pos=(0,0,-1) rot=(0,0,1;0rad)
  Radius = 8.2
FEATURE [Part::Box] extr_hold_tab3
  AttacherType = Attacher::AttachEngine3D
  Height = 5.65
  Length = 11.84
  Placement = pos=(27.66,-1,0) rot=(0,0,1;0rad)
  Width = 12.8
FEATURE [Part::Box] extr_hold_tab3_hole
  AttacherType = Attacher::AttachEngine3D
  Height = 7.05
  Length = 13.24
  Placement = pos=(27.26,0,-1) rot=(0,0,1;0rad)
  Width = 12.8
FEATURE [Part::MultiFuse] extr_hold1_holes_joint
  Shapes = -> [extr_hold_tab0_hole,extr_hold_tab3_hole]
FEATURE [Part::Cylinder] extr_in
  Angle = 360
  AttacherType = Attacher::AttachEngine3D
  Height = 5.6
  Placement = pos=(0,0,2.4) rot=(0,0,1;0rad)
  Radius = 6.2
FEATURE [Part::MultiFuse] extr_rings_1
  Placement = pos=(16.5,0,0) rot=(0,0,1;0rad)
  Shapes = -> [extr_outup,extr_in,extr_outbot]
FEATURE [Part::Cylinder] extr_in_2
  Angle = 360
  AttacherType = Attacher::AttachEngine3D
  Height = 5.6
  Placement = pos=(0,0,2.4) rot=(0,0,1;0rad)
  Radius = 6.2
FEATURE [Part::MultiFuse] extr_rings_2
  Placement = pos=(-16.5,0,0) rot=(0,0,1;0rad)
  Shapes = -> [extr_outup_2,extr_in_2,extr_outbot_2]
FEATURE [Part::Box] extr_hold_tab1
  AttacherType = Attacher::AttachEngine3D
  Height = 5.65
  Length = 11.84
  Placement = pos=(-39.5,-11.8,0) rot=(0,0,1;0rad)
  Width = 12.8
FEATURE [Part::Box] extr_hold_tab0
  AttacherType = Attacher::AttachEngine3D
  Height = 5.65
  Length = 11.84
  Placement = pos=(-39.5,-1,6.05) rot=(0,0,1;0rad)
  Width = 12.8
FEATURE [Part::MultiFuse] extr_hold2_tabs_joint
  Shapes = -> [extr_hold_2,extr_hold_tab0,extr_hold_tab3]
FEATURE [Part::Cut] extr_hold2_joint
  Base = -> extr_hold2_tabs_joint
  Tool = -> extr_hold2_holes_joint
FEATURE [Part::Box] carlow_box
  AttacherType = Attacher::AttachEngine3D
  Height = 12.5
  Length = 109.8
  Placement = pos=(-54.9,-48.7,0) rot=(0,0,1;0rad)
  Width = 97.4
FEATURE [Part::Box] carhig_box
  AttacherType = Attacher::AttachEngine3D
  Height = 12.5
  Length = 109.8
  Placement = pos=(-54.9,-48.7,0) rot=(0,0,1;0rad)
  Width = 97.4
FEATURE [Part::Box] extrhold_higcar
  AttacherType = Attacher::AttachEngine3D
  Height = 1.4
  Length = 79
  Placement = pos=(-39.5,-11.8,12.1) rot=(0,0,1;0rad)
  Width = 23.6
FEATURE [Part::Cylinder] rod_n
  Angle = 360
  AttacherType = Attacher::AttachEngine3D
  Height = 111.8
  Placement = pos=(-55.9,-25,12.5) rot=(0,1,0;1.5708rad)
  Radius = 6
FEATURE [Part::Cylinder] bearing_0
  Angle = 360
  AttacherType = Attacher::AttachEngine3D
  Height = 29.4
  Placement = pos=(8.5,25,12.5) rot=(0,1,0;1.5708rad)
  Radius = 9.7
FEATURE [Part::Box] inrect
  AttacherType = Attacher::AttachEngine3D
  Height = 14.5
  Length = 79.8
  Placement = pos=(-39.9,-12.2,-1) rot=(0,0,1;0rad)
  Width = 24.4
FEATURE [Part::Cylinder] rod_p
  Angle = 360
  AttacherType = Attacher::AttachEngine3D
  Height = 111.8
  Placement = pos=(-55.9,25,12.5) rot=(0,1,0;1.5708rad)
  Radius = 6
FEATURE [Part::Cylinder] bearing_1
  Angle = 360
  AttacherType = Attacher::AttachEngine3D
  Height = 29.4
  Placement = pos=(-37.9,25,12.5) rot=(0,1,0;1.5708rad)
  Radius = 9.7
FEATURE [Part::Box] extr_hold_1
  AttacherType = Attacher::AttachEngine3D
  Height = 11.7
  Length = 79
  Placement = pos=(-39.5,0,0) rot=(0,0,1;0rad)
  Width = 11.8
FEATURE [Part::MultiFuse] extr_hold1_tabs_joint
  Shapes = -> [extr_hold_1,extr_hold_tab1,extr_hold_tab2]
FEATURE [Part::Cut] extr_hold1_joint
  Base = -> extr_hold1_tabs_joint
  Tool = -> extr_hold1_holes_joint
FEATURE [Part::Fillet] carhig_box_fllt
  Base = -> carhig_box
  Edges = 4 edges r=4: [Edge1,Edge3,Edge5,Edge7]
  Placement = pos=(0,0,12.5) rot=(0,0,1;0rad)
FEATURE [Part::Fuse] carghig_fuse
  Base = -> carhig_box_fllt
  Tool = -> extrhold_higcar
FEATURE [Part::Fillet] carlow_box_fllt
  Base = -> carlow_box
  Edges = 4 edges r=4: [Edge1,Edge3,Edge5,Edge7]
FEATURE [Part::Prism] m3_extrbolt_hole_supnut2
  AttacherType = Attacher::AttachEngine3D
  Circumradius = 1.955
  Height = 3.6
  Placement = pos=(0,0,20) rot=(0,0,1;0rad)
  Polygon = 6
FEATURE [Part::Prism] m3_bolt_hole_bolt_sup1
  AttacherType = Attacher::AttachEngine3D
  Circumradius = 3.4
  Height = 3.7
  Placement = pos=(0,0,21.3) rot=(0,0,1;0.523599rad)
  Polygon = 3
FEATURE [Part::Prism] m3_bolt_hole_bolt_sup2
  AttacherType = Attacher::AttachEngine3D
  Circumradius = 1.955
  Height = 4
  Placement = pos=(0,0,21) rot=(0,0,1;0rad)
  Polygon = 6
FEATURE [Part::Prism] m3_bolt_hole_nut
  AttacherType = Attacher::AttachEngine3D
  Circumradius = 3.605
  Height = 3.8
  Placement = pos=(0,0,-1) rot=(0,0,1;0rad)
  Polygon = 6
FEATURE [Part::Prism] m3_extrbolt_hole_bolt_sup1
  AttacherType = Attacher::AttachEngine3D
  Circumradius = 3.4
  Height = 3.7
  Placement = pos=(0,0,0) rot=(0,0,1;0.523599rad)
  Polygon = 3
FEATURE [Part::Prism] m3_extrbolt_hole_bolt_sup2
  AttacherType = Attacher::AttachEngine3D
  Circumradius = 1.955
  Height = 4
  Polygon = 6
FEATURE [Part::Prism] m3_bolt_hole_bolt_sup1001
  AttacherType = Attacher::AttachEngine3D
  Circumradius = 3.4
  Height = 3.7
  Placement = pos=(0,0,21.3) rot=(0,0,1;0.523599rad)
  Polygon = 3
FEATURE [Part::Prism] m3_bolt_hole_bolt_sup2001
  AttacherType = Attacher::AttachEngine3D
  Circumradius = 1.955
  Height = 4
  Placement = pos=(0,0,21) rot=(0,0,1;0rad)
  Polygon = 6
FEATURE [Part::Prism] m3_bolt_hole_nut001
  AttacherType = Attacher::AttachEngine3D
  Circumradius = 3.605
  Height = 3.8
  Placement = pos=(0,0,-1) rot=(0,0,1;0rad)
  Polygon = 6
FEATURE [Part::Prism] m3_bolt_hole_bolt_sup1002
  AttacherType = Attacher::AttachEngine3D
  Circumradius = 3.4
  Height = 3.7
  Placement = pos=(0,0,21.3) rot=(0,0,1;0.523599rad)
  Polygon = 3
FEATURE [Part::Prism] m3_bolt_hole_bolt_sup2002
  AttacherType = Attacher::AttachEngine3D
  Circumradius = 1.955
  Height = 4
  Placement = pos=(0,0,21) rot=(0,0,1;0rad)
  Polygon = 6
FEATURE [Part::Prism] m3_extrbolt_hole_nut
  AttacherType = Attacher::AttachEngine3D
  Circumradius = 3.605
  Height = 4
  Placement = pos=(0,0,20.6) rot=(0,0,1;0rad)
  Polygon = 6
FEATURE [Part::Prism] m3_extrbolt_hole_nutsup1
  AttacherType = Attacher::AttachEngine3D
  Circumradius = 3.4
  Height = 3.3
  Placement = pos=(0,0,20.3) rot=(0,0,1;0.523599rad)
  Polygon = 3
FEATURE [Part::Prism] m3_extrbolt_hole_supnut1away
  AttacherType = Attacher::AttachEngine3D
  Circumradius = 3.605
  Height = 3.3
  Placement = pos=(0,0,20.3) rot=(0,0,1;0rad)
  Polygon = 6
FEATURE [Part::Common] supnut1_cut
  Base = -> m3_extrbolt_hole_nutsup1
  Tool = -> m3_extrbolt_hole_supnut1away
FEATURE [Part::Cylinder] m3_bolt_hole_bolt_sup1away003
  Angle = 360
  AttacherType = Attacher::AttachEngine3D
  Height = 3.7
  Placement = pos=(0,0,21.3) rot=(0,0,1;0rad)
  Radius = 2.95
FEATURE [Part::Cylinder] m3_bolt_hole_bolt_shank
  Angle = 360
  AttacherType = Attacher::AttachEngine3D
  Height = 27
  Placement = pos=(0,0,-1) rot=(0,0,1;0rad)
  Radius = 1.7
FEATURE [Part::Cylinder] m3_bolt_hole_bolt_head004
  Angle = 360
  AttacherType = Attacher::AttachEngine3D
  Height = 4.4
  Placement = pos=(0,0,21.6) rot=(0,0,1;0rad)
  Radius = 2.95
FEATURE [Part::Cylinder] m3_extrbolt_hole_bolt_head
  Angle = 360
  AttacherType = Attacher::AttachEngine3D
  Height = 4.4
  Placement = pos=(0,0,-1) rot=(0,0,1;0rad)
  Radius = 2.95
FEATURE [Part::Cylinder] m3_bolt_hole_bolt_sup1away004
  Angle = 360
  AttacherType = Attacher::AttachEngine3D
  Height = 3.7
  Placement = pos=(0,0,21.3) rot=(0,0,1;0rad)
  Radius = 2.95
FEATURE [Part::Cylinder] m3_bolt_hole_bolt_shank005
  Angle = 360
  AttacherType = Attacher::AttachEngine3D
  Height = 27
  Placement = pos=(0,0,-1) rot=(0,0,1;0rad)
  Radius = 1.7
FEATURE [Part::Cylinder] higcar_fil_hole2
  Angle = 360
  AttacherType = Attacher::AttachEngine3D
  Height = 15.3
  Placement = pos=(-16.5,0,10.7) rot=(0,0,1;0rad)
  Radius = 9.2
FEATURE [Part::Cylinder] m3_bolt_hole_bolt_head005
  Angle = 360
  AttacherType = Attacher::AttachEngine3D
  Height = 4.4
  Placement = pos=(0,0,21.6) rot=(0,0,1;0rad)
  Radius = 2.95
FEATURE [Part::Cylinder] m3_bolt_hole_bolt_head001
  Angle = 360
  AttacherType = Attacher::AttachEngine3D
  Height = 4.4
  Placement = pos=(0,0,21.6) rot=(0,0,1;0rad)
  Radius = 2.95
FEATURE [Part::Cylinder] m3_bolt_hole_bolt_sup1away001
  Angle = 360
  AttacherType = Attacher::AttachEngine3D
  Height = 3.7
  Placement = pos=(0,0,21.3) rot=(0,0,1;0rad)
  Radius = 2.95
FEATURE [Part::Common] sup1cut002
  Base = -> m3_bolt_hole_bolt_sup1001
  Tool = -> m3_bolt_hole_bolt_sup1away001
FEATURE [Part::Cylinder] bearing_3
  Angle = 360
  AttacherType = Attacher::AttachEngine3D
  Height = 29.4
  Placement = pos=(-37.9,-25,12.5) rot=(0,1,0;1.5708rad)
  Radius = 9.7
FEATURE [Part::Cylinder] m3_bolt_hole_bolt_sup1away
  Angle = 360
  AttacherType = Attacher::AttachEngine3D
  Height = 3.7
  Placement = pos=(0,0,21.3) rot=(0,0,1;0rad)
  Radius = 2.95
FEATURE [Part::Common] sup1cut001
  Base = -> m3_bolt_hole_bolt_sup1
  Tool = -> m3_bolt_hole_bolt_sup1away
FEATURE [Part::Cylinder] m3_bolt_hole_bolt_shank001
  Angle = 360
  AttacherType = Attacher::AttachEngine3D
  Height = 27
  Placement = pos=(0,0,-1) rot=(0,0,1;0rad)
  Radius = 1.7
FEATURE [Part::Cylinder] m3_bolt_hole_bolt_head002
  Angle = 360
  AttacherType = Attacher::AttachEngine3D
  Height = 4.4
  Placement = pos=(0,0,21.6) rot=(0,0,1;0rad)
  Radius = 2.95
FEATURE [Part::Cylinder] m3_bolt_hole_bolt_sup1away002
  Angle = 360
  AttacherType = Attacher::AttachEngine3D
  Height = 3.7
  Placement = pos=(0,0,21.3) rot=(0,0,1;0rad)
  Radius = 2.95
FEATURE [Part::Common] sup1cut003
  Base = -> m3_bolt_hole_bolt_sup1002
  Tool = -> m3_bolt_hole_bolt_sup1away002
FEATURE [Part::Cylinder] bearing_2
  Angle = 360
  AttacherType = Attacher::AttachEngine3D
  Height = 29.4
  Placement = pos=(8.5,-25,12.5) rot=(0,1,0;1.5708rad)
  Radius = 9.7
FEATURE [Part::Cylinder] m3_extrbolt_hole_bolt_shank
  Angle = 360
  AttacherType = Attacher::AttachEngine3D
  Height = 25.6
  Placement = pos=(0,0,-1) rot=(0,0,1;0rad)
  Radius = 1.7
FEATURE [Part::Cylinder] m3_bolt_hole_bolt_shank003
  Angle = 360
  AttacherType = Attacher::AttachEngine3D
  Height = 27
  Placement = pos=(0,0,-1) rot=(0,0,1;0rad)
  Radius = 1.7
FEATURE [Part::Cylinder] m3_extrbolt_hole_bolt_sup1away
  Angle = 360
  AttacherType = Attacher::AttachEngine3D
  Height = 3.7
  Radius = 2.95
FEATURE [Part::Common] sup1cut
  Base = -> m3_extrbolt_hole_bolt_sup1
  Tool = -> m3_extrbolt_hole_bolt_sup1away
FEATURE [Part::MultiFuse] m3_extrbolt_hole_bolt
  Shapes = -> [m3_extrbolt_hole_bolt_shank,m3_extrbolt_hole_bolt_head,sup1cut,m3_extrbolt_hole_bolt_sup2]
FEATURE [Part::Cylinder] m3_bolt_hole_bolt_head
  Angle = 360
  AttacherType = Attacher::AttachEngine3D
  Height = 4.4
  Placement = pos=(0,0,21.6) rot=(0,0,1;0rad)
  Radius = 2.95
FEATURE [Part::Cylinder] m3_bolt_hole_bolt_head003
  Angle = 360
  AttacherType = Attacher::AttachEngine3D
  Height = 4.4
  Placement = pos=(0,0,21.6) rot=(0,0,1;0rad)
  Radius = 2.95
FEATURE [Part::Cylinder] higcar_fil_hole1
  Angle = 360
  AttacherType = Attacher::AttachEngine3D
  Height = 15.3
  Placement = pos=(16.5,0,10.7) rot=(0,0,1;0rad)
  Radius = 9.2
FEATURE [Part::Cylinder] m3_bolt_hole_bolt_shank002
  Angle = 360
  AttacherType = Attacher::AttachEngine3D
  Height = 27
  Placement = pos=(0,0,-1) rot=(0,0,1;0rad)
  Radius = 1.7
FEATURE [Part::Cylinder] m3_bolt_hole_bolt_shank004
  Angle = 360
  AttacherType = Attacher::AttachEngine3D
  Height = 27
  Placement = pos=(0,0,-1) rot=(0,0,1;0rad)
  Radius = 1.7
FEATURE [Part::Extrusion] gt2clamp0extr_base
  Base = -> gt2clamp0base_plane_yz
  Dir = (23,0,0)
  DirMode = 0
  FaceMakerClass = Part::FaceMakerExtrusion
  LengthFwd = 0
  LengthRev = 0
  Solid = true
  Symmetric = false
FEATURE [Part::Prism] m3_bolt_hole_nut002
  AttacherType = Attacher::AttachEngine3D
  Circumradius = 3.605
  Height = 3.8
  Placement = pos=(0,0,-1) rot=(0,0,1;0rad)
  Polygon = 6
FEATURE [Part::Prism] m3_bolt_hole_nutsup1
  AttacherType = Attacher::AttachEngine3D
  Circumradius = 3.4
  Height = 3.1
  Placement = pos=(0,0,0) rot=(0,0,1;0.523599rad)
  Polygon = 3
FEATURE [Part::Prism] m3_bolt_hole_supnut1away
  AttacherType = Attacher::AttachEngine3D
  Circumradius = 3.605
  Height = 3.1
  Polygon = 6
FEATURE [Part::Common] supnut1_cut001
  Base = -> m3_bolt_hole_nutsup1
  Tool = -> m3_bolt_hole_supnut1away
FEATURE [Part::MultiFuse] m3_bolt_hole_bolt002
  Shapes = -> [m3_bolt_hole_bolt_shank002,m3_bolt_hole_bolt_head002,sup1cut003,m3_bolt_hole_bolt_sup2002]
FEATURE [Part::MultiFuse] m3_bolt_hole_bolt
  Shapes = -> [m3_bolt_hole_bolt_shank,m3_bolt_hole_bolt_head,sup1cut001,m3_bolt_hole_bolt_sup2]
FEATURE [Part::MultiFuse] m3_bolt_hole_bolt001
  Shapes = -> [m3_bolt_hole_bolt_shank001,m3_bolt_hole_bolt_head001,sup1cut002,m3_bolt_hole_bolt_sup2001]
FEATURE [Part::MultiFuse] boltnut002
  Placement = pos=(-33.58,0,0) rot=(0,0,1;0rad)
  Shapes = -> [m3_bolt_hole_bolt001,m3_bolt_hole_nut001]
FEATURE [Part::MultiFuse] boltnut001
  Placement = pos=(33.58,0,0) rot=(0,0,1;0rad)
  Shapes = -> [m3_bolt_hole_bolt,m3_bolt_hole_nut]
FEATURE [Part::MultiFuse] boltnut
  Placement = pos=(0,11.8,5.85) rot=(1,0,0;1.5708rad)
  Shapes = -> [m3_extrbolt_hole_bolt,m3_extrbolt_hole_nut,supnut1_cut,m3_extrbolt_hole_supnut2]
FEATURE [Part::Prism] m3_bolt_hole_supnut2
  AttacherType = Attacher::AttachEngine3D
  Circumradius = 1.955
  Height = 3.4
  Polygon = 6
FEATURE [Part::MultiFuse] boltnut003
  Placement = pos=(46.4,41.7,0) rot=(0,0,1;0rad)
  Shapes = -> [m3_bolt_hole_bolt002,m3_bolt_hole_nut002,supnut1_cut001,m3_bolt_hole_supnut2]
FEATURE [Part::Prism] m3_bolt_hole_bolt_sup2003
  AttacherType = Attacher::AttachEngine3D
  Circumradius = 1.955
  Height = 4
  Placement = pos=(0,0,21) rot=(0,0,1;0rad)
  Polygon = 6
FEATURE [Part::Prism] m3_bolt_hole_nut003
  AttacherType = Attacher::AttachEngine3D
  Circumradius = 3.605
  Height = 3.8
  Placement = pos=(0,0,-1) rot=(0,0,1;0rad)
  Polygon = 6
FEATURE [Part::Prism] m3_bolt_hole_bolt_sup1003
  AttacherType = Attacher::AttachEngine3D
  Circumradius = 3.4
  Height = 3.7
  Placement = pos=(0,0,21.3) rot=(0,0,1;0.523599rad)
  Polygon = 3
FEATURE [Part::Common] sup1cut004
  Base = -> m3_bolt_hole_bolt_sup1003
  Tool = -> m3_bolt_hole_bolt_sup1away003
FEATURE [Part::MultiFuse] m3_bolt_hole_bolt003
  Shapes = -> [m3_bolt_hole_bolt_shank003,m3_bolt_hole_bolt_head003,sup1cut004,m3_bolt_hole_bolt_sup2003]
FEATURE [Part::Prism] m3_bolt_hole_nutsup1001
  AttacherType = Attacher::AttachEngine3D
  Circumradius = 3.4
  Height = 3.1
  Placement = pos=(0,0,0) rot=(0,0,1;0.523599rad)
  Polygon = 3
FEATURE [Part::Prism] m3_bolt_hole_supnut1away001
  AttacherType = Attacher::AttachEngine3D
  Circumradius = 3.605
  Height = 3.1
  Polygon = 6
FEATURE [Part::Common] supnut1_cut002
  Base = -> m3_bolt_hole_nutsup1001
  Tool = -> m3_bolt_hole_supnut1away001
FEATURE [Part::Prism] m3_bolt_hole_bolt_sup1005
  AttacherType = Attacher::AttachEngine3D
  Circumradius = 3.4
  Height = 3.7
  Placement = pos=(0,0,21.3) rot=(0,0,1;0.523599rad)
  Polygon = 3
FEATURE [Part::Prism] m3_bolt_hole_bolt_sup2005
  AttacherType = Attacher::AttachEngine3D
  Circumradius = 1.955
  Height = 4
  Placement = pos=(0,0,21) rot=(0,0,1;0rad)
  Polygon = 6
FEATURE [Part::Prism] m3_bolt_hole_bolt_sup2004
  AttacherType = Attacher::AttachEngine3D
  Circumradius = 1.955
  Height = 4
  Placement = pos=(0,0,21) rot=(0,0,1;0rad)
  Polygon = 6
FEATURE [Part::Prism] m3_bolt_hole_nut004
  AttacherType = Attacher::AttachEngine3D
  Circumradius = 3.605
  Height = 3.8
  Placement = pos=(0,0,-1) rot=(0,0,1;0rad)
  Polygon = 6
FEATURE [Part::Prism] m3_bolt_hole_bolt_sup1004
  AttacherType = Attacher::AttachEngine3D
  Circumradius = 3.4
  Height = 3.7
  Placement = pos=(0,0,21.3) rot=(0,0,1;0.523599rad)
  Polygon = 3
FEATURE [Part::Common] sup1cut005
  Base = -> m3_bolt_hole_bolt_sup1004
  Tool = -> m3_bolt_hole_bolt_sup1away004
FEATURE [Part::MultiFuse] m3_bolt_hole_bolt004
  Shapes = -> [m3_bolt_hole_bolt_shank004,m3_bolt_hole_bolt_head004,sup1cut005,m3_bolt_hole_bolt_sup2004]
FEATURE [Part::Prism] m3_bolt_hole_supnut2001
  AttacherType = Attacher::AttachEngine3D
  Circumradius = 1.955
  Height = 3.4
  Polygon = 6
FEATURE [Part::MultiFuse] boltnut004
  Placement = pos=(0,41.7,0) rot=(0,0,1;0rad)
  Shapes = -> [m3_bolt_hole_bolt003,m3_bolt_hole_nut003,supnut1_cut002,m3_bolt_hole_supnut2001]
FEATURE [Part::Prism] m3_bolt_hole_nutsup1002
  AttacherType = Attacher::AttachEngine3D
  Circumradius = 3.4
  Height = 3.1
  Placement = pos=(0,0,0) rot=(0,0,1;0.523599rad)
  Polygon = 3
FEATURE [Part::Prism] m3_bolt_hole_supnut1away002
  AttacherType = Attacher::AttachEngine3D
  Circumradius = 3.605
  Height = 3.1
  Polygon = 6
FEATURE [Part::Prism] m3_bolt_hole_supnut2002
  AttacherType = Attacher::AttachEngine3D
  Circumradius = 1.955
  Height = 3.4
  Polygon = 6
FEATURE [Part::Common] supnut1_cut003
  Base = -> m3_bolt_hole_nutsup1002
  Tool = -> m3_bolt_hole_supnut1away002
FEATURE [Part::MultiFuse] boltnut005
  Placement = pos=(-46.4,41.7,0) rot=(0,0,1;0rad)
  Shapes = -> [m3_bolt_hole_bolt004,m3_bolt_hole_nut004,supnut1_cut003,m3_bolt_hole_supnut2002]
FEATURE [Part::Cylinder] gt2clamp1_cyl
  Angle = 360
  AttacherType = Attacher::AttachEngine3D
  Height = 9
  Placement = pos=(4,8.00417,11.5) rot=(0,0,1;0rad)
  Radius = 4
FEATURE [Part::Cylinder] gt2clamp1_base_lscrew_head
  Angle = 360
  AttacherType = Attacher::AttachEngine3D
  Height = 9.5
  Placement = pos=(0,0,-1) rot=(0,0,1;0rad)
  Radius = 2.95
FEATURE [Part::Cylinder] m3_bolt_hole_bolt_shank006
  Angle = 360
  AttacherType = Attacher::AttachEngine3D
  Height = 27
  Placement = pos=(0,0,-1) rot=(0,0,1;0rad)
  Radius = 1.7
FEATURE [Part::Cylinder] m3_bolt_hole_bolt_head007
  Angle = 360
  AttacherType = Attacher::AttachEngine3D
  Height = 4.4
  Placement = pos=(0,0,21.6) rot=(0,0,1;0rad)
  Radius = 2.95
FEATURE [Part::Box] gt2clamp0_cb3
  AttacherType = Attacher::AttachEngine3D
  Height = 9
  Length = 12
  Placement = pos=(11,9.40417,11.5) rot=(0,0,1;0rad)
  Width = 4
FEATURE [Part::Cylinder] gt2clamp0_cyl
  Angle = 360
  AttacherType = Attacher::AttachEngine3D
  Height = 9
  Placement = pos=(4,8.00417,11.5) rot=(0,0,1;0rad)
  Radius = 4
FEATURE [Part::Box] gt2clamp1_cb1
  AttacherType = Attacher::AttachEngine3D
  Height = 9
  Length = 12
  Placement = pos=(11,2.60417,11.5) rot=(0,0,1;0rad)
  Width = 4
FEATURE [Part::Cylinder] m3_bolt_hole_bolt_sup1away006
  Angle = 360
  AttacherType = Attacher::AttachEngine3D
  Height = 3.7
  Placement = pos=(0,0,21.3) rot=(0,0,1;0rad)
  Radius = 2.95
FEATURE [Part::Cylinder] m3_bolt_hole_bolt_head006
  Angle = 360
  AttacherType = Attacher::AttachEngine3D
  Height = 4.4
  Placement = pos=(0,0,21.6) rot=(0,0,1;0rad)
  Radius = 2.95
FEATURE [Part::Cylinder] m3_bolt_hole_bolt_shank007
  Angle = 360
  AttacherType = Attacher::AttachEngine3D
  Height = 27
  Placement = pos=(0,0,-1) rot=(0,0,1;0rad)
  Radius = 1.7
FEATURE [Part::Box] bccr_box
  AttacherType = Attacher::AttachEngine3D
  Height = 25
  Length = 41
  Placement = pos=(43,-19,0) rot=(0,0,1;0rad)
  Width = 38
FEATURE [Part::Box] bccr_box001
  AttacherType = Attacher::AttachEngine3D
  Height = 25
  Length = 41
  Placement = pos=(42.6,-19.4,0) rot=(0,0,1;0rad)
  Width = 38.8
FEATURE [Part::Box] gt2clamp0_cb1
  AttacherType = Attacher::AttachEngine3D
  Height = 9
  Length = 12
  Placement = pos=(11,2.60417,11.5) rot=(0,0,1;0rad)
  Width = 4
FEATURE [Part::MultiFuse] gt2clamp0clamp_base
  Shapes = -> [gt2clamp0_cb1,gt2clamp0_cb3,gt2clamp0_cyl,gt2clamp0extr_base]
FEATURE [Part::Box] gt2clamp1_base_lscrew_nut2
  AttacherType = Attacher::AttachEngine3D
  Height = 6.65
  Length = 5.04
  Placement = pos=(3,4.88224,0) rot=(0,0,1;0rad)
  Width = 6.24386
FEATURE [Part::Box] bccr_box_of_clean
  AttacherType = Attacher::AttachEngine3D
  Height = 6
  Length = 41
  Placement = pos=(42.6,-25,12.5) rot=(0,0,1;0rad)
  Width = 50
FEATURE [Part::Fuse] fuse_bccr_box_of
  Base = -> bccr_box001
  Tool = -> bccr_box_of_clean
FEATURE [Part::FeaturePython] Clone024  label="Clone of fuse_bccr_box_of"  # Draft clone (typed FeaturePython)
  Objects = -> [fuse_bccr_box_of]
  Placement = pos=(0,0,0) rot=(0,0,1;3.14159rad)
  Scale = (1,1,1)
FEATURE [Part::Box] highcar_lscrew_hole0
  AttacherType = Attacher::AttachEngine3D
  Height = 11
  Length = 27.1
  Placement = pos=(16.5,5.45417,15) rot=(0,0,1;0rad)
  Width = 7.5
FEATURE [Part::Box] highcar_lscrew_hole1
  AttacherType = Attacher::AttachEngine3D
  Height = 11
  Length = 27.1
  Placement = pos=(16.5,-12.9542,15) rot=(0,0,1;0rad)
  Width = 7.5
FEATURE [Part::Fuse] higcar_lscrew_fuse
  Base = -> highcar_lscrew_hole0
  Tool = -> highcar_lscrew_hole1
FEATURE [Part::FeaturePython] Clone023  label="Clone of higcar_lscrew_fuse"  # Draft clone (typed FeaturePython)
  Objects = -> [higcar_lscrew_fuse]
  Placement = pos=(0,0,0) rot=(0,0,1;3.14159rad)
  Scale = (1,1,1)
FEATURE [Part::Cylinder] m3_bolt_hole_bolt_sup1away005
  Angle = 360
  AttacherType = Attacher::AttachEngine3D
  Height = 3.7
  Placement = pos=(0,0,21.3) rot=(0,0,1;0rad)
  Radius = 2.95
FEATURE [Part::Common] sup1cut006
  Base = -> m3_bolt_hole_bolt_sup1005
  Tool = -> m3_bolt_hole_bolt_sup1away005
FEATURE [Part::MultiFuse] m3_bolt_hole_bolt005
  Shapes = -> [m3_bolt_hole_bolt_shank005,m3_bolt_hole_bolt_head005,sup1cut006,m3_bolt_hole_bolt_sup2005]
FEATURE [Part::Cylinder] m3_bolt_hole_bolt_sup1away007
  Angle = 360
  AttacherType = Attacher::AttachEngine3D
  Height = 3.7
  Placement = pos=(0,0,21.3) rot=(0,0,1;0rad)
  Radius = 2.95
FEATURE [Part::Cylinder] gt2clamp0_base_lscrew_head
  Angle = 360
  AttacherType = Attacher::AttachEngine3D
  Height = 9.5
  Placement = pos=(0,0,-1) rot=(0,0,1;0rad)
  Radius = 2.95
FEATURE [Part::Cylinder] gt2clamp0_base_lscrew_shank
  Angle = 360
  AttacherType = Attacher::AttachEngine3D
  Height = 25
  Placement = pos=(0,0,-1) rot=(0,0,1;0rad)
  Radius = 1.7
FEATURE [Part::MultiFuse] gt2clamp0_base_lscrew
  Placement = pos=(23,8.00417,6.25) rot=(0,-1,0;1.5708rad)
  Shapes = -> [gt2clamp0_base_lscrew_shank,gt2clamp0_base_lscrew_head]
FEATURE [Part::Box] gt2clamp0_base_lscrew_nut2
  AttacherType = Attacher::AttachEngine3D
  Height = 6.65
  Length = 5.04
  Placement = pos=(3,4.88224,0) rot=(0,0,1;0rad)
  Width = 6.24386
FEATURE [Part::Cylinder] gt2clamp1_base_lscrew_shank
  Angle = 360
  AttacherType = Attacher::AttachEngine3D
  Height = 25
  Placement = pos=(0,0,-1) rot=(0,0,1;0rad)
  Radius = 1.7
FEATURE [Part::Box] gt2clamp1_cb3
  AttacherType = Attacher::AttachEngine3D
  Height = 9
  Length = 12
  Placement = pos=(11,9.40417,11.5) rot=(0,0,1;0rad)
  Width = 4
FEATURE [Part::Prism] m3_bolt_hole_bolt_sup1006
  AttacherType = Attacher::AttachEngine3D
  Circumradius = 3.4
  Height = 3.7
  Placement = pos=(0,0,21.3) rot=(0,0,1;0.523599rad)
  Polygon = 3
FEATURE [Part::Common] sup1cut007
  Base = -> m3_bolt_hole_bolt_sup1006
  Tool = -> m3_bolt_hole_bolt_sup1away006
FEATURE [Part::Prism] m3_bolt_hole_supnut2003
  AttacherType = Attacher::AttachEngine3D
  Circumradius = 1.955
  Height = 3.4
  Polygon = 6
FEATURE [Part::Prism] m3_bolt_hole_bolt_sup2006
  AttacherType = Attacher::AttachEngine3D
  Circumradius = 1.955
  Height = 4
  Placement = pos=(0,0,21) rot=(0,0,1;0rad)
  Polygon = 6
FEATURE [Part::MultiFuse] m3_bolt_hole_bolt006
  Shapes = -> [m3_bolt_hole_bolt_shank006,m3_bolt_hole_bolt_head006,sup1cut007,m3_bolt_hole_bolt_sup2006]
FEATURE [Part::Prism] m3_bolt_hole_nut006
  AttacherType = Attacher::AttachEngine3D
  Circumradius = 3.605
  Height = 3.8
  Placement = pos=(0,0,-1) rot=(0,0,1;0rad)
  Polygon = 6
FEATURE [Part::Prism] m3_bolt_hole_supnut1away004
  AttacherType = Attacher::AttachEngine3D
  Circumradius = 3.605
  Height = 3.1
  Polygon = 6
FEATURE [Part::Prism] m3_bolt_hole_nutsup1003
  AttacherType = Attacher::AttachEngine3D
  Circumradius = 3.4
  Height = 3.1
  Placement = pos=(0,0,0) rot=(0,0,1;0.523599rad)
  Polygon = 3
FEATURE [Part::Prism] m3_bolt_hole_nutsup1004
  AttacherType = Attacher::AttachEngine3D
  Circumradius = 3.4
  Height = 3.1
  Placement = pos=(0,0,0) rot=(0,0,1;0.523599rad)
  Polygon = 3
FEATURE [Part::Common] supnut1_cut005
  Base = -> m3_bolt_hole_nutsup1004
  Tool = -> m3_bolt_hole_supnut1away004
FEATURE [Part::Prism] m3_bolt_hole_nut005
  AttacherType = Attacher::AttachEngine3D
  Circumradius = 3.605
  Height = 3.8
  Placement = pos=(0,0,-1) rot=(0,0,1;0rad)
  Polygon = 6
FEATURE [Part::Prism] m3_bolt_hole_supnut1away003
  AttacherType = Attacher::AttachEngine3D
  Circumradius = 3.605
  Height = 3.1
  Polygon = 6
FEATURE [Part::Common] supnut1_cut004
  Base = -> m3_bolt_hole_nutsup1003
  Tool = -> m3_bolt_hole_supnut1away003
FEATURE [Part::MultiFuse] boltnut006
  Placement = pos=(46.4,-41.7,0) rot=(0,0,1;0rad)
  Shapes = -> [m3_bolt_hole_bolt005,m3_bolt_hole_nut005,supnut1_cut004,m3_bolt_hole_supnut2003]
FEATURE [Part::Prism] m3_bolt_hole_supnut2004
  AttacherType = Attacher::AttachEngine3D
  Circumradius = 1.955
  Height = 3.4
  Polygon = 6
FEATURE [Part::MultiFuse] boltnut007
  Placement = pos=(0,-41.7,0) rot=(0,0,1;0rad)
  Shapes = -> [m3_bolt_hole_bolt006,m3_bolt_hole_nut006,supnut1_cut005,m3_bolt_hole_supnut2004]
FEATURE [Part::Prism] m3_bolt_hole_bolt_sup2007
  AttacherType = Attacher::AttachEngine3D
  Circumradius = 1.955
  Height = 4
  Placement = pos=(0,0,21) rot=(0,0,1;0rad)
  Polygon = 6
FEATURE [Part::Prism] m3_bolt_hole_bolt_sup1007
  AttacherType = Attacher::AttachEngine3D
  Circumradius = 3.4
  Height = 3.7
  Placement = pos=(0,0,21.3) rot=(0,0,1;0.523599rad)
  Polygon = 3
FEATURE [Part::Common] sup1cut008
  Base = -> m3_bolt_hole_bolt_sup1007
  Tool = -> m3_bolt_hole_bolt_sup1away007
FEATURE [Part::MultiFuse] m3_bolt_hole_bolt007
  Shapes = -> [m3_bolt_hole_bolt_shank007,m3_bolt_hole_bolt_head007,sup1cut008,m3_bolt_hole_bolt_sup2007]
FEATURE [Part::Prism] m3_bolt_hole_nut007
  AttacherType = Attacher::AttachEngine3D
  Circumradius = 3.605
  Height = 3.8
  Placement = pos=(0,0,-1) rot=(0,0,1;0rad)
  Polygon = 6
FEATURE [Part::Prism] gt2clamp0_base_lscrew_nut
  AttacherType = Attacher::AttachEngine3D
  Circumradius = 3.605
  Height = 5.04
  Placement = pos=(3,8.00417,6.65) rot=(0,1,0;1.5708rad)
  Polygon = 6
FEATURE [Part::Prism] m3_bolt_hole_supnut2005
  AttacherType = Attacher::AttachEngine3D
  Circumradius = 1.955
  Height = 3.4
  Polygon = 6
FEATURE [Part::Prism] m3_bolt_hole_supnut1away005
  AttacherType = Attacher::AttachEngine3D
  Circumradius = 3.605
  Height = 3.1
  Polygon = 6
FEATURE [Part::Prism] m3_bolt_hole_nutsup1005
  AttacherType = Attacher::AttachEngine3D
  Circumradius = 3.4
  Height = 3.1
  Placement = pos=(0,0,0) rot=(0,0,1;0.523599rad)
  Polygon = 3
FEATURE [Part::Common] supnut1_cut006
  Base = -> m3_bolt_hole_nutsup1005
  Tool = -> m3_bolt_hole_supnut1away005
FEATURE [Part::MultiFuse] boltnut008
  Placement = pos=(-46.4,-41.7,0) rot=(0,0,1;0rad)
  Shapes = -> [m3_bolt_hole_bolt007,m3_bolt_hole_nut007,supnut1_cut006,m3_bolt_hole_supnut2005]
FEATURE [Part::Polygon] gt2clamp1base_plane_yz
  Close = true
  Nodes = (12) [(0,2.60417,0),(0,2.60417,2.34375),(0,0,4.94792),(0,0,7.55208),(0,2.60417,10.1562),(0,2.60417,12.5),(0,13.4042,12.5),(0,13.4042,10.1562),+4 more]
FEATURE [Part::Polygon] gt2clamp0_baseof_plane_yz
  Close = true
  Nodes = (12) [(0,2.20417,0),(0,2.20417,2.34375),(0,-0.4,4.94792),(0,-0.4,7.55208),(0,2.20417,10.1562),(0,2.20417,12.5),(0,13.8042,12.5),(0,13.8042,10.1562),+4 more]
FEATURE [Part::Polygon] gt2clamp1_baseof_plane_yz
  Close = true
  Nodes = (12) [(0,2.20417,0),(0,2.20417,2.34375),(0,-0.4,4.94792),(0,-0.4,7.55208),(0,2.20417,10.1562),(0,2.20417,12.5),(0,13.8042,12.5),(0,13.8042,10.1562),+4 more]
FEATURE [Part::Extrusion] gt2clamp0_baseof
  Base = -> gt2clamp0_baseof_plane_yz
  Dir = (39,0,0)
  DirMode = 0
  FaceMakerClass = Part::FaceMakerExtrusion
  LengthFwd = 0
  LengthRev = 0
  Placement = pos=(46,1.2,12.5) rot=(0,0,1;0rad)
  Solid = true
  Symmetric = false
FEATURE [Part::Extrusion] gt2clamp1extr_base
  Base = -> gt2clamp1base_plane_yz
  Dir = (23,0,0)
  DirMode = 0
  FaceMakerClass = Part::FaceMakerExtrusion
  LengthFwd = 0
  LengthRev = 0
  Solid = true
  Symmetric = false
FEATURE [Part::Extrusion] gt2clamp1_baseof
  Base = -> gt2clamp1_baseof_plane_yz
  Dir = (39,0,0)
  DirMode = 0
  FaceMakerClass = Part::FaceMakerExtrusion
  LengthFwd = 0
  LengthRev = 0
  Placement = pos=(46,-17.2083,12.5) rot=(0,0,1;0rad)
  Solid = true
  Symmetric = false
FEATURE [Part::Fillet] bccr_fllt
  Base = -> bccr_box
  Edges = 4 edges r=4: [Edge1,Edge3,Edge5,Edge7]
FEATURE [Part::MultiFuse] gt2clamp1_base_lscrew
  Placement = pos=(23,8.00417,6.25) rot=(0,-1,0;1.5708rad)
  Shapes = -> [gt2clamp1_base_lscrew_shank,gt2clamp1_base_lscrew_head]
FEATURE [Part::MultiFuse] fuse_extr_holder_holes
  Shapes = -> [extr_rings_1,extr_rings_2,boltnut,boltnut001,boltnut002]
FEATURE [Part::Cut] tot_extr_hold_1
  Base = -> extr_hold1_joint
  Tool = -> fuse_extr_holder_holes
FEATURE [Part::Cut] tot_extr_hold_2
  Base = -> extr_hold2_joint
  Tool = -> fuse_extr_holder_holes
FEATURE [Part::MultiFuse] fuse_higcar_holes
  Shapes = -> [rod_n,rod_p,bearing_0,bearing_1,bearing_2,bearing_3,higcar_fil_hole1,higcar_fil_hole2,boltnut001,boltnut002,boltnut003,boltnut004,boltnut005,boltnut006,boltnut007,boltnut008,fuse_bccr_box_of,Clone024,higcar_lscrew_fuse,Clone023]
FEATURE [Part::Cut] higcar_hole
  Base = -> carghig_fuse
  Tool = -> fuse_higcar_holes
FEATURE [Part::MultiFuse] gt2clamp0_clamp_hole
  Shapes = -> [gt2clamp0_base_lscrew,gt2clamp0_base_lscrew_nut,gt2clamp0_base_lscrew_nut2]
FEATURE [Part::Cut] gt2clamp0
  Base = -> gt2clamp0clamp_base
  Placement = pos=(54.9,1.2,12.5) rot=(0,0,1;0rad)
  Tool = -> gt2clamp0_clamp_hole
FEATURE [Part::MultiFuse] gt2clamp1clamp_base
  Shapes = -> [gt2clamp1_cb1,gt2clamp1_cb3,gt2clamp1_cyl,gt2clamp1extr_base]
FEATURE [Part::Prism] gt2clamp1_base_lscrew_nut
  AttacherType = Attacher::AttachEngine3D
  Circumradius = 3.605
  Height = 5.04
  Placement = pos=(3,8.00417,6.65) rot=(0,1,0;1.5708rad)
  Polygon = 6
FEATURE [Part::MultiFuse] gt2clamp1_clamp_hole
  Shapes = -> [gt2clamp1_base_lscrew,gt2clamp1_base_lscrew_nut,gt2clamp1_base_lscrew_nut2]
FEATURE [Part::Cut] gt2clamp1
  Base = -> gt2clamp1clamp_base
  Placement = pos=(54.9,-17.2083,12.5) rot=(0,0,1;0rad)
  Tool = -> gt2clamp1_clamp_hole
FEATURE [Part::Box] bccr_bthole0
  AttacherType = Attacher::AttachEngine3D
  Height = 14.5
  Length = 35
  Placement = pos=(0,-3.12193,0) rot=(0,0,1;0rad)
  Width = 6.24386
FEATURE [Part::Fillet] bccr_bthole0_fllt
  Base = -> bccr_bthole0
  Edges = 4 edges r=2: [Edge1,Edge3,Edge5,Edge7]
  Placement = pos=(46,9.20417,-1) rot=(0,0,1;0rad)
FEATURE [Part::Cylinder] bccr_bolthole1
  Angle = 360
  AttacherType = Attacher::AttachEngine3D
  Height = 5
  Placement = pos=(42,-9.20417,18.75) rot=(0,1,0;1.5708rad)
  Radius = 1.7
FEATURE [Part::Box] bccr_bthole1
  AttacherType = Attacher::AttachEngine3D
  Height = 14.5
  Length = 35
  Placement = pos=(0,-3.12193,0) rot=(0,0,1;0rad)
  Width = 6.24386
FEATURE [Part::Fillet] bccr_bthole1_fllt
  Base = -> bccr_bthole1
  Edges = 4 edges r=2: [Edge1,Edge3,Edge5,Edge7]
  Placement = pos=(46,-9.20417,-1) rot=(0,0,1;0rad)
FEATURE [Part::Fuse] bccr_bthole_fused
  Base = -> bccr_bthole0_fllt
  Tool = -> bccr_bthole1_fllt
FEATURE [Part::FeaturePython] Clone025  label="Clone of bccr_bthole_fused"  # Draft clone (typed FeaturePython)
  Objects = -> [bccr_bthole_fused]
  Placement = pos=(0,0,0) rot=(0,0,1;3.14159rad)
  Scale = (1,1,1)
FEATURE [Part::MultiFuse] fuse_lowcar_holes
  Shapes = -> [inrect,rod_n,rod_p,bearing_0,bearing_1,bearing_2,bearing_3,boltnut003,boltnut004,boltnut005,boltnut006,boltnut007,boltnut008,bccr_bthole_fused,Clone025]
FEATURE [Part::Cut] lowcar_hole
  Base = -> carlow_box_fllt
  Tool = -> fuse_lowcar_holes
FEATURE [Part::Cylinder] bccr_bolthole0
  Angle = 360
  AttacherType = Attacher::AttachEngine3D
  Height = 5
  Placement = pos=(42,9.20417,18.75) rot=(0,1,0;1.5708rad)
  Radius = 1.7
FEATURE [Part::MultiFuse] bccr_holes
  Shapes = -> [gt2clamp0_baseof,gt2clamp1_baseof,bccr_bthole0_fllt,bccr_bthole1_fllt,bccr_bolthole0,bccr_bolthole1]
FEATURE [Part::Cut] bccr_final
  Base = -> bccr_fllt
  Tool = -> bccr_holes
FEATURE [Part::FeaturePython] Clone026  label="Clone of bccr_final"  # Draft clone (typed FeaturePython)
  Objects = -> [bccr_final]
  Placement = pos=(0,0,0) rot=(0,0,1;3.14159rad)
  Scale = (1,1,1)
FEATURE [Part::MultiFuse] lowcar_bccr
  Shapes = -> [lowcar_hole,bccr_final,Clone026]
FEATURE [Part::FeaturePython] BooleanFragments001  label="Carrito"  # WARN: FeaturePython — macro-defined, semantics opaque (R4)
  Mode = 0
  Objects = -> [gt2clamp1,gt2clamp0,tot_extr_hold_1,lowcar_bccr,tot_extr_hold_2,higcar_hole]
  Placement = pos=(355,315,613) rot=(0,0,1;0rad)
  Tolerance = 0
FEATURE [Part::Cylinder] Cylinder013  label="Cilindro002"
  Angle = 360
  AttacherType = Attacher::AttachEngine3D
  Height = 32.4
  Placement = pos=(0,3,14) rot=(-1,0,0;1.5708rad)
  Radius = 11.3
FEATURE [Part::Cylinder] Cylinder014  label="Cilindro003"
  Angle = 360
  AttacherType = Attacher::AttachEngine3D
  Height = 80
  Placement = pos=(0,-2,14) rot=(-1,0,0;1.5708rad)
  Radius = 7
FEATURE [Part::Feature] Cylinder015  label="Cilindro2"
  Placement = pos=(0,38.4,14) rot=(-1,0,0;1.5708rad)
  shape: bbox 22.6 x 32.4 x 22.6 mm, 3 faces (baked)
FEATURE [Sketcher::SketchObject] Sketch013
  MapMode = 5
  sketch-geometry (22):
    g0: LineSegment StartX=-33 StartY=0 StartZ=0 EndX=33 EndY=0 EndZ=0
    g1: ArcOfCircle CenterX=-33 CenterY=5 CenterZ=0 NormalX=0 NormalY=0 NormalZ=1 AngleXU=0 Radius=5 StartAngle=3.14159 EndAngle=4.71239
    g2: LineSegment StartX=-38 StartY=5 StartZ=0 EndX=-38 EndY=15 EndZ=0
    g3: ArcOfCircle CenterX=-33 CenterY=15 CenterZ=0 NormalX=0 NormalY=0 NormalZ=1 AngleXU=0 Radius=5 StartAngle=1.5708 EndAngle=3.14159
    g4: LineSegment StartX=-33 StartY=20 StartZ=0 EndX=-28 EndY=20 EndZ=0
    g5: ArcOfCircle CenterX=-28 CenterY=25 CenterZ=0 NormalX=0 NormalY=0 NormalZ=1 AngleXU=0 Radius=5 StartAngle=4.71239 EndAngle=6.28319
    g6: LineSegment StartX=-23 StartY=25 StartZ=0 EndX=-23 EndY=69 EndZ=0
    g7: ArcOfCircle CenterX=-18 CenterY=69 CenterZ=0 NormalX=0 NormalY=0 NormalZ=1 AngleXU=0 Radius=5 StartAngle=1.57079 EndAngle=3.14159
    g8: LineSegment StartX=-18 StartY=74 StartZ=0 EndX=18 EndY=74 EndZ=0
    g9: ArcOfCircle CenterX=33 CenterY=5 CenterZ=0 NormalX=0 NormalY=0 NormalZ=1 AngleXU=0 Radius=5 StartAngle=4.71239 EndAngle=6.28319
    g10: LineSegment StartX=38 StartY=5 StartZ=0 EndX=38 EndY=15 EndZ=0
    g11: ArcOfCircle CenterX=18 CenterY=69 CenterZ=0 NormalX=0 NormalY=0 NormalZ=1 AngleXU=0 Radius=5 StartAngle=2.37406e-07 EndAngle=1.5708
    g12: LineSegment StartX=23 StartY=69 StartZ=0 EndX=23 EndY=25 EndZ=0
    g13: ArcOfCircle CenterX=28 CenterY=25 CenterZ=0 NormalX=0 NormalY=0 NormalZ=1 AngleXU=0 Radius=5 StartAngle=3.14159 EndAngle=4.71239
    g14: LineSegment StartX=28 StartY=20 StartZ=0 EndX=33 EndY=20 EndZ=0
    g15: ArcOfCircle CenterX=33 CenterY=15 CenterZ=0 NormalX=0 NormalY=0 NormalZ=1 AngleXU=0 Radius=5 StartAngle=6.28318 EndAngle=7.85398
    g16: Circle CenterX=28 CenterY=10 CenterZ=0 NormalX=0 NormalY=0 NormalZ=1 AngleXU=0 Radius=2.7
    g17: Circle CenterX=-28 CenterY=10 CenterZ=0 NormalX=0 NormalY=0 NormalZ=1 AngleXU=0 Radius=2.7
    g18: Circle CenterX=18 CenterY=64 CenterZ=0 NormalX=0 NormalY=0 NormalZ=1 AngleXU=0 Radius=1.68
    g19: Circle CenterX=18 CenterY=37 CenterZ=0 NormalX=0 NormalY=0 NormalZ=1 AngleXU=0 Radius=1.68
    g20: Circle CenterX=-18 CenterY=37 CenterZ=0 NormalX=0 NormalY=0 NormalZ=1 AngleXU=0 Radius=1.68
    g21: Circle CenterX=-18 CenterY=64 CenterZ=0 NormalX=0 NormalY=0 NormalZ=1 AngleXU=0 Radius=1.68
  constraints (67):
    c: Horizontal(g0)
    c: Vertical(g2)
    c: Coincident(g1,g2)
    c: Coincident(g1,g0)
    c: Coincident(g2,g3)
    c: Tangent(g2,g3)
    c: Tangent(g1,g2)
    c: Tangent(g0,g1)
    c: Horizontal(g4)
    c: Coincident(g3,g4)
    c: Tangent(g4,g5) = -1.5708
    c: Vertical(g6)
    c: Tangent(g4,g3)
    c: Coincident(g6,g7)
    c: Tangent(g7,g6)
    c: Horizontal(g8)
    c: Coincident(g8,g7)
    c: Tangent(g8,g7)
    c: Coincident(g5,g6)
    c: Tangent(g5,g6)
    c: DistanceX(g-1,g6) = -23
    c: Radius(g3) = 5
    c: Radius(g1) = 5
    c: Radius(g5) = 5
    c: Equal(g7,g5)
    c: DistanceY(g3,g0) = -20
    c: DistanceY(g7,g0) = -74
    c: Coincident(g9,g0)
    c: Equal(g9,g1)
    c: Tangent(g9,g0)
    c: DistanceY(g-1,g0) = 0
    c: DistanceX(g2,g5) = 15
    c: Vertical(g10)
    c: Symmetric(g10,g1,g-2)
    c: Coincident(g10,g9)
    c: Symmetric(g10,g2,g-2)
    c: Symmetric(g8,g7,g-2)
    c: Symmetric(g11,g7,g-2)
    c: Coincident(g11,g8)
    c: Vertical(g12)
    c: Coincident(g12,g11)
    c: Coincident(g13,g12)
    c: Tangent(g12,g11)
    c: Tangent(g13,g12)
    c: Horizontal(g14)
    c: Coincident(g13,g14)
    c: Coincident(g15,g14)
    c: Coincident(g15,g10)
    c: Symmetric(g13,g4,g-2)
    c: Symmetric(g14,g3,g-2)
    c: Equal(g13,g5)
    c: Equal(g15,g3)
    c: DistanceY(g16,g0) = -10
    c: DistanceX(g16,g10) = 10
    c: Radius(g16) = 2.7
    c: Symmetric(g17,g16,g-2)
    c: Equal(g17,g16)
    c: DistanceY(g18,g8) = 10
    c: Radius(g18) = 1.68
    c: DistanceX(g18,g11) = 5
    c: DistanceY(g19,g16) = -27
    c: Equal(g19,g18)
    c: DistanceX(g19,g18) = 0
    c: Symmetric(g20,g19,g-2)
    c: Equal(g20,g19)
    c: Equal(g21,g18)
    c: Symmetric(g21,g18,g-2)
FEATURE [PartDesign::Pad] Pad
  Length = 14
  Length2 = 100
  Profile = -> Sketch013
  Type = 0
FEATURE [Part::Cut] Cut015
  Base = -> Pad
  Tool = -> Cylinder013
FEATURE [Part::Cut] Cut014  label="Z_axis_LM12UU_nut"
  Base = -> Cut015
  Tool = -> Cylinder015
FEATURE [Part::Cut] Cut016  label="CoreXY_Z_Axix_LM12UU_Nut A"
  Base = -> Cut014
  Placement = pos=(24,305,330) rot=(0.57735,-0.57735,0.57735;4.18879rad)
  Tool = -> Cylinder014
FEATURE [Part::Feature] Cylinder017  label="Cilindro004"
  Placement = pos=(0,38.4,14) rot=(-1,0,0;1.5708rad)
  shape: bbox 22.6 x 32.4 x 22.6 mm, 3 faces (baked)
FEATURE [Sketcher::SketchObject] Sketch014
  MapMode = 5
  sketch-geometry (22):
    g0: LineSegment StartX=-33 StartY=0 StartZ=0 EndX=33 EndY=0 EndZ=0
    g1: ArcOfCircle CenterX=-33 CenterY=5 CenterZ=0 NormalX=0 NormalY=0 NormalZ=1 AngleXU=0 Radius=5 StartAngle=3.14159 EndAngle=4.71239
    g2: LineSegment StartX=-38 StartY=5 StartZ=0 EndX=-38 EndY=15 EndZ=0
    g3: ArcOfCircle CenterX=-33 CenterY=15 CenterZ=0 NormalX=0 NormalY=0 NormalZ=1 AngleXU=0 Radius=5 StartAngle=1.5708 EndAngle=3.14159
    g4: LineSegment StartX=-33 StartY=20 StartZ=0 EndX=-28 EndY=20 EndZ=0
    g5: ArcOfCircle CenterX=-28 CenterY=25 CenterZ=0 NormalX=0 NormalY=0 NormalZ=1 AngleXU=0 Radius=5 StartAngle=4.71239 EndAngle=6.28319
    g6: LineSegment StartX=-23 StartY=25 StartZ=0 EndX=-23 EndY=69 EndZ=0
    g7: ArcOfCircle CenterX=-18 CenterY=69 CenterZ=0 NormalX=0 NormalY=0 NormalZ=1 AngleXU=0 Radius=5 StartAngle=1.57079 EndAngle=3.14159
    g8: LineSegment StartX=-18 StartY=74 StartZ=0 EndX=18 EndY=74 EndZ=0
    g9: ArcOfCircle CenterX=33 CenterY=5 CenterZ=0 NormalX=0 NormalY=0 NormalZ=1 AngleXU=0 Radius=5 StartAngle=4.71239 EndAngle=6.28319
    g10: LineSegment StartX=38 StartY=5 StartZ=0 EndX=38 EndY=15 EndZ=0
    g11: ArcOfCircle CenterX=18 CenterY=69 CenterZ=0 NormalX=0 NormalY=0 NormalZ=1 AngleXU=0 Radius=5 StartAngle=2.37406e-07 EndAngle=1.5708
    g12: LineSegment StartX=23 StartY=69 StartZ=0 EndX=23 EndY=25 EndZ=0
    g13: ArcOfCircle CenterX=28 CenterY=25 CenterZ=0 NormalX=0 NormalY=0 NormalZ=1 AngleXU=0 Radius=5 StartAngle=3.14159 EndAngle=4.71239
    g14: LineSegment StartX=28 StartY=20 StartZ=0 EndX=33 EndY=20 EndZ=0
    g15: ArcOfCircle CenterX=33 CenterY=15 CenterZ=0 NormalX=0 NormalY=0 NormalZ=1 AngleXU=0 Radius=5 StartAngle=6.28318 EndAngle=7.85398
    g16: Circle CenterX=28 CenterY=10 CenterZ=0 NormalX=0 NormalY=0 NormalZ=1 AngleXU=0 Radius=2.7
    g17: Circle CenterX=-28 CenterY=10 CenterZ=0 NormalX=0 NormalY=0 NormalZ=1 AngleXU=0 Radius=2.7
    g18: Circle CenterX=18 CenterY=64 CenterZ=0 NormalX=0 NormalY=0 NormalZ=1 AngleXU=0 Radius=1.68
    g19: Circle CenterX=18 CenterY=37 CenterZ=0 NormalX=0 NormalY=0 NormalZ=1 AngleXU=0 Radius=1.68
    g20: Circle CenterX=-18 CenterY=37 CenterZ=0 NormalX=0 NormalY=0 NormalZ=1 AngleXU=0 Radius=1.68
    g21: Circle CenterX=-18 CenterY=64 CenterZ=0 NormalX=0 NormalY=0 NormalZ=1 AngleXU=0 Radius=1.68
  constraints (67):
    c: Horizontal(g0)
    c: Vertical(g2)
    c: Coincident(g1,g2)
    c: Coincident(g1,g0)
    c: Coincident(g2,g3)
    c: Tangent(g2,g3)
    c: Tangent(g1,g2)
    c: Tangent(g0,g1)
    c: Horizontal(g4)
    c: Coincident(g3,g4)
    c: Tangent(g4,g5) = -1.5708
    c: Vertical(g6)
    c: Tangent(g4,g3)
    c: Coincident(g6,g7)
    c: Tangent(g7,g6)
    c: Horizontal(g8)
    c: Coincident(g8,g7)
    c: Tangent(g8,g7)
    c: Coincident(g5,g6)
    c: Tangent(g5,g6)
    c: DistanceX(g-1,g6) = -23
    c: Radius(g3) = 5
    c: Radius(g1) = 5
    c: Radius(g5) = 5
    c: Equal(g7,g5)
    c: DistanceY(g3,g0) = -20
    c: DistanceY(g7,g0) = -74
    c: Coincident(g9,g0)
    c: Equal(g9,g1)
    c: Tangent(g9,g0)
    c: DistanceY(g-1,g0) = 0
    c: DistanceX(g2,g5) = 15
    c: Vertical(g10)
    c: Symmetric(g10,g1,g-2)
    c: Coincident(g10,g9)
    c: Symmetric(g10,g2,g-2)
    c: Symmetric(g8,g7,g-2)
    c: Symmetric(g11,g7,g-2)
    c: Coincident(g11,g8)
    c: Vertical(g12)
    c: Coincident(g12,g11)
    c: Coincident(g13,g12)
    c: Tangent(g12,g11)
    c: Tangent(g13,g12)
    c: Horizontal(g14)
    c: Coincident(g13,g14)
    c: Coincident(g15,g14)
    c: Coincident(g15,g10)
    c: Symmetric(g13,g4,g-2)
    c: Symmetric(g14,g3,g-2)
    c: Equal(g13,g5)
    c: Equal(g15,g3)
    c: DistanceY(g16,g0) = -10
    c: DistanceX(g16,g10) = 10
    c: Radius(g16) = 2.7
    c: Symmetric(g17,g16,g-2)
    c: Equal(g17,g16)
    c: DistanceY(g18,g8) = 10
    c: Radius(g18) = 1.68
    c: DistanceX(g18,g11) = 5
    c: DistanceY(g19,g16) = -27
    c: Equal(g19,g18)
    c: DistanceX(g19,g18) = 0
    c: Symmetric(g20,g19,g-2)
    c: Equal(g20,g19)
    c: Equal(g21,g18)
    c: Symmetric(g21,g18,g-2)
FEATURE [Part::Cylinder] Cylinder018  label="Cilindro005"
  Angle = 360
  AttacherType = Attacher::AttachEngine3D
  Height = 32.4
  Placement = pos=(0,3,14) rot=(-1,0,0;1.5708rad)
  Radius = 11.3
FEATURE [Part::Cylinder] Cylinder019  label="Cilindro006"
  Angle = 360
  AttacherType = Attacher::AttachEngine3D
  Height = 80
  Placement = pos=(0,-2,14) rot=(-1,0,0;1.5708rad)
  Radius = 7
FEATURE [PartDesign::Pad] Pad001
  Length = 14
  Length2 = 100
  Profile = -> Sketch014
  Type = 0
FEATURE [Part::Cut] Cut017
  Base = -> Pad001
  Tool = -> Cylinder018
FEATURE [Part::Cut] Cut019  label="Z_axis_LM12UU_nut001"
  Base = -> Cut017
  Tool = -> Cylinder017
FEATURE [Part::Cut] Cut018  label="CoreXY_Z_Axix_LM12UU_Nut B"
  Base = -> Cut019
  Placement = pos=(53,305,330) rot=(0.57735,0.57735,-0.57735;4.18879rad)
  Tool = -> Cylinder019
FEATURE [Part::Fuse] Fusion024  label="sujetacamas izquierdo"
  Base = -> Cut016
  Placement = pos=(0,-174,0) rot=(0,0,1;0rad)
  Tool = -> Cut018
FEATURE [Part::Feature] X_End_Nut001_solid002  label="X_End_Nut001 (Solid)002"
  Placement = pos=(380,0,30.5275) rot=(0,1,0;3.14159rad)
  shape: bbox 79 x 58 x 15 mm, 1430 faces (baked)
FEATURE [Part::Feature] X_End_Nut001_solid001  label="X_End_Nut001 (Solid)001"
  shape: bbox 79 x 58 x 15 mm, 1430 faces (baked)
FEATURE [Part::Fuse] Fusion026
  Base = -> X_End_Nut001_solid001
  Placement = pos=(737,125,610) rot=(0,0,1;1.5708rad)
  Tool = -> X_End_Nut001_solid002
FEATURE [Part::Fuse] Fusion027
  Base = -> X_End_Nut001_solid001
  Placement = pos=(-28,505,610) rot=(0,0,-1;1.5708rad)
  Tool = -> X_End_Nut001_solid002
FEATURE [Part::FeaturePython] BooleanFragments002  label="Tornillo sin fin005"  # WARN: FeaturePython — macro-defined, semantics opaque (R4)
  Mode = 0
  Objects = -> [Fusion004,Fillet,mirror001,mirror,Fusion005]
  Tolerance = 0
FEATURE [Part::Cylinder] Cylinder027  label="Tornillo sin fin001"
  Angle = 360
  AttacherType = Attacher::AttachEngine3D
  Height = 510
  Placement = pos=(40,130,90) rot=(0,0,1;0rad)
  Radius = 5
FEATURE [Part::Box] Box028  label="Cubo007"
  AttacherType = Attacher::AttachEngine3D
  Height = 14
  Length = 2
  Placement = pos=(6,8,0) rot=(0,0,1;0rad)
  Width = 10
FEATURE [Part::Cylinder] Cylinder029  label="Cilindro013"
  Angle = 360
  AttacherType = Attacher::AttachEngine3D
  Height = 10
  Placement = pos=(17,7,7) rot=(1,0,0;1.5708rad)
  Radius = 2
FEATURE [Part::Box] Box029  label="Cubo008"
  AttacherType = Attacher::AttachEngine3D
  Height = 14
  Length = 14
  Width = 14
FEATURE [Part::Box] Box030  label="Cubo001"
  AttacherType = Attacher::AttachEngine3D
  Height = 14
  Length = 26
  Placement = pos=(-6,0,0) rot=(0,0,1;0rad)
  Width = 2
FEATURE [Part::MultiFuse] Fusion028
  Shapes = -> [Box029,Box030]
FEATURE [Part::Cylinder] Cylinder030  label="Cilindro014"
  Angle = 360
  AttacherType = Attacher::AttachEngine3D
  Height = 10
  Placement = pos=(-3,7,7) rot=(1,0,0;1.5708rad)
  Radius = 2
FEATURE [Part::Cylinder] Cylinder031  label="Cilindro015"
  Angle = 360
  AttacherType = Attacher::AttachEngine3D
  Height = 14
  Placement = pos=(7,8,0) rot=(0,0,1;0rad)
  Radius = 5
FEATURE [Part::Cut] Cut027
  Base = -> Fusion028
  Tool = -> Cylinder031
FEATURE [Part::Cut] Cut026
  Base = -> Cut027
  Tool = -> Box028
FEATURE [Part::Cut] Cut029
  Base = -> Cut026
  Tool = -> Cylinder030
FEATURE [Part::Cut] Cut028  label="Sujección barilla eje zZ"
  Base = -> Cut029
  Placement = pos=(32,135,95) rot=(0,0,-1;1.5708rad)
  Tool = -> Cylinder029
FEATURE [Part::Fuse] Fusion029  label="Barra sujeeción 1"
  Base = -> Cylinder027
  Tool = -> Cut028
FEATURE [Part::Fuse] Fusion030  label="Sujetacamas izq 1"
  Base = -> Fusion024
  Tool = -> Fusion029
FEATURE [Part::Cylinder] Cylinder032  label="Cilindro016"
  Angle = 360
  AttacherType = Attacher::AttachEngine3D
  Height = 32.4
  Placement = pos=(0,3,14) rot=(-1,0,0;1.5708rad)
  Radius = 11.3
FEATURE [Part::Cylinder] Cylinder033  label="Cilindro017"
  Angle = 360
  AttacherType = Attacher::AttachEngine3D
  Height = 32.4
  Placement = pos=(0,3,14) rot=(-1,0,0;1.5708rad)
  Radius = 11.3
FEATURE [Part::Feature] Cylinder036  label="Cilindro020"
  Placement = pos=(0,38.4,14) rot=(-1,0,0;1.5708rad)
  shape: bbox 22.6 x 32.4 x 22.6 mm, 3 faces (baked)
FEATURE [Part::Feature] Cylinder037  label="Cilindro021"
  Placement = pos=(0,38.4,14) rot=(-1,0,0;1.5708rad)
  shape: bbox 22.6 x 32.4 x 22.6 mm, 3 faces (baked)
FEATURE [Sketcher::SketchObject] Sketch017
  MapMode = 5
  sketch-geometry (22):
    g0: LineSegment StartX=-33 StartY=0 StartZ=0 EndX=33 EndY=0 EndZ=0
    g1: ArcOfCircle CenterX=-33 CenterY=5 CenterZ=0 NormalX=0 NormalY=0 NormalZ=1 AngleXU=0 Radius=5 StartAngle=3.14159 EndAngle=4.71239
    g2: LineSegment StartX=-38 StartY=5 StartZ=0 EndX=-38 EndY=15 EndZ=0
    g3: ArcOfCircle CenterX=-33 CenterY=15 CenterZ=0 NormalX=0 NormalY=0 NormalZ=1 AngleXU=0 Radius=5 StartAngle=1.5708 EndAngle=3.14159
    g4: LineSegment StartX=-33 StartY=20 StartZ=0 EndX=-28 EndY=20 EndZ=0
    g5: ArcOfCircle CenterX=-28 CenterY=25 CenterZ=0 NormalX=0 NormalY=0 NormalZ=1 AngleXU=0 Radius=5 StartAngle=4.71239 EndAngle=6.28319
    g6: LineSegment StartX=-23 StartY=25 StartZ=0 EndX=-23 EndY=69 EndZ=0
    g7: ArcOfCircle CenterX=-18 CenterY=69 CenterZ=0 NormalX=0 NormalY=0 NormalZ=1 AngleXU=0 Radius=5 StartAngle=1.57079 EndAngle=3.14159
    g8: LineSegment StartX=-18 StartY=74 StartZ=0 EndX=18 EndY=74 EndZ=0
    g9: ArcOfCircle CenterX=33 CenterY=5 CenterZ=0 NormalX=0 NormalY=0 NormalZ=1 AngleXU=0 Radius=5 StartAngle=4.71239 EndAngle=6.28319
    g10: LineSegment StartX=38 StartY=5 StartZ=0 EndX=38 EndY=15 EndZ=0
    g11: ArcOfCircle CenterX=18 CenterY=69 CenterZ=0 NormalX=0 NormalY=0 NormalZ=1 AngleXU=0 Radius=5 StartAngle=2.37406e-07 EndAngle=1.5708
    g12: LineSegment StartX=23 StartY=69 StartZ=0 EndX=23 EndY=25 EndZ=0
    g13: ArcOfCircle CenterX=28 CenterY=25 CenterZ=0 NormalX=0 NormalY=0 NormalZ=1 AngleXU=0 Radius=5 StartAngle=3.14159 EndAngle=4.71239
    g14: LineSegment StartX=28 StartY=20 StartZ=0 EndX=33 EndY=20 EndZ=0
    g15: ArcOfCircle CenterX=33 CenterY=15 CenterZ=0 NormalX=0 NormalY=0 NormalZ=1 AngleXU=0 Radius=5 StartAngle=6.28318 EndAngle=7.85398
    g16: Circle CenterX=28 CenterY=10 CenterZ=0 NormalX=0 NormalY=0 NormalZ=1 AngleXU=0 Radius=2.7
    g17: Circle CenterX=-28 CenterY=10 CenterZ=0 NormalX=0 NormalY=0 NormalZ=1 AngleXU=0 Radius=2.7
    g18: Circle CenterX=18 CenterY=64 CenterZ=0 NormalX=0 NormalY=0 NormalZ=1 AngleXU=0 Radius=1.68
    g19: Circle CenterX=18 CenterY=37 CenterZ=0 NormalX=0 NormalY=0 NormalZ=1 AngleXU=0 Radius=1.68
    g20: Circle CenterX=-18 CenterY=37 CenterZ=0 NormalX=0 NormalY=0 NormalZ=1 AngleXU=0 Radius=1.68
    g21: Circle CenterX=-18 CenterY=64 CenterZ=0 NormalX=0 NormalY=0 NormalZ=1 AngleXU=0 Radius=1.68
  constraints (67):
    c: Horizontal(g0)
    c: Vertical(g2)
    c: Coincident(g1,g2)
    c: Coincident(g1,g0)
    c: Coincident(g2,g3)
    c: Tangent(g2,g3)
    c: Tangent(g1,g2)
    c: Tangent(g0,g1)
    c: Horizontal(g4)
    c: Coincident(g3,g4)
    c: Tangent(g4,g5) = -1.5708
    c: Vertical(g6)
    c: Tangent(g4,g3)
    c: Coincident(g6,g7)
    c: Tangent(g7,g6)
    c: Horizontal(g8)
    c: Coincident(g8,g7)
    c: Tangent(g8,g7)
    c: Coincident(g5,g6)
    c: Tangent(g5,g6)
    c: DistanceX(g-1,g6) = -23
    c: Radius(g3) = 5
    c: Radius(g1) = 5
    c: Radius(g5) = 5
    c: Equal(g7,g5)
    c: DistanceY(g3,g0) = -20
    c: DistanceY(g7,g0) = -74
    c: Coincident(g9,g0)
    c: Equal(g9,g1)
    c: Tangent(g9,g0)
    c: DistanceY(g-1,g0) = 0
    c: DistanceX(g2,g5) = 15
    c: Vertical(g10)
    c: Symmetric(g10,g1,g-2)
    c: Coincident(g10,g9)
    c: Symmetric(g10,g2,g-2)
    c: Symmetric(g8,g7,g-2)
    c: Symmetric(g11,g7,g-2)
    c: Coincident(g11,g8)
    c: Vertical(g12)
    c: Coincident(g12,g11)
    c: Coincident(g13,g12)
    c: Tangent(g12,g11)
    c: Tangent(g13,g12)
    c: Horizontal(g14)
    c: Coincident(g13,g14)
    c: Coincident(g15,g14)
    c: Coincident(g15,g10)
    c: Symmetric(g13,g4,g-2)
    c: Symmetric(g14,g3,g-2)
    c: Equal(g13,g5)
    c: Equal(g15,g3)
    c: DistanceY(g16,g0) = -10
    c: DistanceX(g16,g10) = 10
    c: Radius(g16) = 2.7
    c: Symmetric(g17,g16,g-2)
    c: Equal(g17,g16)
    c: DistanceY(g18,g8) = 10
    c: Radius(g18) = 1.68
    c: DistanceX(g18,g11) = 5
    c: DistanceY(g19,g16) = -27
    c: Equal(g19,g18)
    c: DistanceX(g19,g18) = 0
    c: Symmetric(g20,g19,g-2)
    c: Equal(g20,g19)
    c: Equal(g21,g18)
    c: Symmetric(g21,g18,g-2)
FEATURE [PartDesign::Pad] Pad005
  Length = 14
  Length2 = 100
  Profile = -> Sketch017
  Type = 0
FEATURE [Part::Cut] Cut036
  Base = -> Pad005
  Tool = -> Cylinder033
FEATURE [Sketcher::SketchObject] Sketch018
  MapMode = 5
  sketch-geometry (22):
    g0: LineSegment StartX=-33 StartY=0 StartZ=0 EndX=33 EndY=0 EndZ=0
    g1: ArcOfCircle CenterX=-33 CenterY=5 CenterZ=0 NormalX=0 NormalY=0 NormalZ=1 AngleXU=0 Radius=5 StartAngle=3.14159 EndAngle=4.71239
    g2: LineSegment StartX=-38 StartY=5 StartZ=0 EndX=-38 EndY=15 EndZ=0
    g3: ArcOfCircle CenterX=-33 CenterY=15 CenterZ=0 NormalX=0 NormalY=0 NormalZ=1 AngleXU=0 Radius=5 StartAngle=1.5708 EndAngle=3.14159
    g4: LineSegment StartX=-33 StartY=20 StartZ=0 EndX=-28 EndY=20 EndZ=0
    g5: ArcOfCircle CenterX=-28 CenterY=25 CenterZ=0 NormalX=0 NormalY=0 NormalZ=1 AngleXU=0 Radius=5 StartAngle=4.71239 EndAngle=6.28319
    g6: LineSegment StartX=-23 StartY=25 StartZ=0 EndX=-23 EndY=69 EndZ=0
    g7: ArcOfCircle CenterX=-18 CenterY=69 CenterZ=0 NormalX=0 NormalY=0 NormalZ=1 AngleXU=0 Radius=5 StartAngle=1.57079 EndAngle=3.14159
    g8: LineSegment StartX=-18 StartY=74 StartZ=0 EndX=18 EndY=74 EndZ=0
    g9: ArcOfCircle CenterX=33 CenterY=5 CenterZ=0 NormalX=0 NormalY=0 NormalZ=1 AngleXU=0 Radius=5 StartAngle=4.71239 EndAngle=6.28319
    g10: LineSegment StartX=38 StartY=5 StartZ=0 EndX=38 EndY=15 EndZ=0
    g11: ArcOfCircle CenterX=18 CenterY=69 CenterZ=0 NormalX=0 NormalY=0 NormalZ=1 AngleXU=0 Radius=5 StartAngle=2.37406e-07 EndAngle=1.5708
    g12: LineSegment StartX=23 StartY=69 StartZ=0 EndX=23 EndY=25 EndZ=0
    g13: ArcOfCircle CenterX=28 CenterY=25 CenterZ=0 NormalX=0 NormalY=0 NormalZ=1 AngleXU=0 Radius=5 StartAngle=3.14159 EndAngle=4.71239
    g14: LineSegment StartX=28 StartY=20 StartZ=0 EndX=33 EndY=20 EndZ=0
    g15: ArcOfCircle CenterX=33 CenterY=15 CenterZ=0 NormalX=0 NormalY=0 NormalZ=1 AngleXU=0 Radius=5 StartAngle=6.28318 EndAngle=7.85398
    g16: Circle CenterX=28 CenterY=10 CenterZ=0 NormalX=0 NormalY=0 NormalZ=1 AngleXU=0 Radius=2.7
    g17: Circle CenterX=-28 CenterY=10 CenterZ=0 NormalX=0 NormalY=0 NormalZ=1 AngleXU=0 Radius=2.7
    g18: Circle CenterX=18 CenterY=64 CenterZ=0 NormalX=0 NormalY=0 NormalZ=1 AngleXU=0 Radius=1.68
    g19: Circle CenterX=18 CenterY=37 CenterZ=0 NormalX=0 NormalY=0 NormalZ=1 AngleXU=0 Radius=1.68
    g20: Circle CenterX=-18 CenterY=37 CenterZ=0 NormalX=0 NormalY=0 NormalZ=1 AngleXU=0 Radius=1.68
    g21: Circle CenterX=-18 CenterY=64 CenterZ=0 NormalX=0 NormalY=0 NormalZ=1 AngleXU=0 Radius=1.68
  constraints (67):
    c: Horizontal(g0)
    c: Vertical(g2)
    c: Coincident(g1,g2)
    c: Coincident(g1,g0)
    c: Coincident(g2,g3)
    c: Tangent(g2,g3)
    c: Tangent(g1,g2)
    c: Tangent(g0,g1)
    c: Horizontal(g4)
    c: Coincident(g3,g4)
    c: Tangent(g4,g5) = -1.5708
    c: Vertical(g6)
    c: Tangent(g4,g3)
    c: Coincident(g6,g7)
    c: Tangent(g7,g6)
    c: Horizontal(g8)
    c: Coincident(g8,g7)
    c: Tangent(g8,g7)
    c: Coincident(g5,g6)
    c: Tangent(g5,g6)
    c: DistanceX(g-1,g6) = -23
    c: Radius(g3) = 5
    c: Radius(g1) = 5
    c: Radius(g5) = 5
    c: Equal(g7,g5)
    c: DistanceY(g3,g0) = -20
    c: DistanceY(g7,g0) = -74
    c: Coincident(g9,g0)
    c: Equal(g9,g1)
    c: Tangent(g9,g0)
    c: DistanceY(g-1,g0) = 0
    c: DistanceX(g2,g5) = 15
    c: Vertical(g10)
    c: Symmetric(g10,g1,g-2)
    c: Coincident(g10,g9)
    c: Symmetric(g10,g2,g-2)
    c: Symmetric(g8,g7,g-2)
    c: Symmetric(g11,g7,g-2)
    c: Coincident(g11,g8)
    c: Vertical(g12)
    c: Coincident(g12,g11)
    c: Coincident(g13,g12)
    c: Tangent(g12,g11)
    c: Tangent(g13,g12)
    c: Horizontal(g14)
    c: Coincident(g13,g14)
    c: Coincident(g15,g14)
    c: Coincident(g15,g10)
    c: Symmetric(g13,g4,g-2)
    c: Symmetric(g14,g3,g-2)
    c: Equal(g13,g5)
    c: Equal(g15,g3)
    c: DistanceY(g16,g0) = -10
    c: DistanceX(g16,g10) = 10
    c: Radius(g16) = 2.7
    c: Symmetric(g17,g16,g-2)
    c: Equal(g17,g16)
    c: DistanceY(g18,g8) = 10
    c: Radius(g18) = 1.68
    c: DistanceX(g18,g11) = 5
    c: DistanceY(g19,g16) = -27
    c: Equal(g19,g18)
    c: DistanceX(g19,g18) = 0
    c: Symmetric(g20,g19,g-2)
    c: Equal(g20,g19)
    c: Equal(g21,g18)
    c: Symmetric(g21,g18,g-2)
FEATURE [PartDesign::Pad] Pad004
  Length = 14
  Length2 = 100
  Profile = -> Sketch018
  Type = 0
FEATURE [Part::Cut] Cut039
  Base = -> Pad004
  Tool = -> Cylinder032
FEATURE [Part::Cylinder] Cylinder039  label="Cilindro022"
  Angle = 360
  AttacherType = Attacher::AttachEngine3D
  Height = 10
  Placement = pos=(-3,7,7) rot=(1,0,0;1.5708rad)
  Radius = 2
FEATURE [Part::Box] Box031  label="Cubo009"
  AttacherType = Attacher::AttachEngine3D
  Height = 14
  Length = 26
  Placement = pos=(-6,0,0) rot=(0,0,1;0rad)
  Width = 2
FEATURE [Part::Cylinder] Cylinder041  label="Cilindro024"
  Angle = 360
  AttacherType = Attacher::AttachEngine3D
  Height = 14
  Placement = pos=(7,8,0) rot=(0,0,1;0rad)
  Radius = 5
FEATURE [Part::Box] Box032  label="Cubo010"
  AttacherType = Attacher::AttachEngine3D
  Height = 14
  Length = 2
  Placement = pos=(6,8,0) rot=(0,0,1;0rad)
  Width = 10
FEATURE [Part::Box] Box033  label="Cubo011"
  AttacherType = Attacher::AttachEngine3D
  Height = 14
  Length = 14
  Width = 14
FEATURE [Part::MultiFuse] Fusion034
  Shapes = -> [Box033,Box031]
FEATURE [Part::Cut] Cut030
  Base = -> Fusion034
  Tool = -> Cylinder041
FEATURE [Part::Cut] Cut033
  Base = -> Cut030
  Tool = -> Box032
FEATURE [Part::Cylinder] Cylinder042  label="Cilindro025"
  Angle = 360
  AttacherType = Attacher::AttachEngine3D
  Height = 32.4
  Placement = pos=(0,3,14) rot=(-1,0,0;1.5708rad)
  Radius = 11.3
FEATURE [Part::Cylinder] Cylinder043  label="Cilindro026"
  Angle = 360
  AttacherType = Attacher::AttachEngine3D
  Height = 32.4
  Placement = pos=(0,3,14) rot=(-1,0,0;1.5708rad)
  Radius = 11.3
FEATURE [Part::Cylinder] Cylinder044  label="Cilindro027"
  Angle = 360
  AttacherType = Attacher::AttachEngine3D
  Height = 80
  Placement = pos=(0,-2,14) rot=(-1,0,0;1.5708rad)
  Radius = 7
FEATURE [Part::Cylinder] Cylinder045  label="Cilindro028"
  Angle = 360
  AttacherType = Attacher::AttachEngine3D
  Height = 80
  Placement = pos=(0,-2,14) rot=(-1,0,0;1.5708rad)
  Radius = 7
FEATURE [Part::Box] Box034  label="Cubo012"
  AttacherType = Attacher::AttachEngine3D
  Height = 14
  Length = 14
  Width = 14
FEATURE [Part::Cylinder] Cylinder046  label="Cilindro029"
  Angle = 360
  AttacherType = Attacher::AttachEngine3D
  Height = 32.4
  Placement = pos=(0,3,14) rot=(-1,0,0;1.5708rad)
  Radius = 11.3
FEATURE [Part::Cylinder] Cylinder047  label="Cilindro030"
  Angle = 360
  AttacherType = Attacher::AttachEngine3D
  Height = 80
  Placement = pos=(0,-2,14) rot=(-1,0,0;1.5708rad)
  Radius = 7
FEATURE [Part::Cylinder] Cylinder048  label="Tornillo sin fin003"
  Angle = 360
  AttacherType = Attacher::AttachEngine3D
  Height = 510
  Placement = pos=(40,130,90) rot=(0,0,1;0rad)
  Radius = 5
FEATURE [Part::Cylinder] Cylinder049  label="Cilindro031"
  Angle = 360
  AttacherType = Attacher::AttachEngine3D
  Height = 10
  Placement = pos=(-3,7,7) rot=(1,0,0;1.5708rad)
  Radius = 2
FEATURE [Part::Box] Box035  label="Cubo013"
  AttacherType = Attacher::AttachEngine3D
  Height = 14
  Length = 26
  Placement = pos=(-6,0,0) rot=(0,0,1;0rad)
  Width = 2
FEATURE [Part::MultiFuse] Fusion043
  Shapes = -> [Box034,Box035]
FEATURE [Part::Cylinder] Cylinder050  label="Cilindro032"
  Angle = 360
  AttacherType = Attacher::AttachEngine3D
  Height = 10
  Placement = pos=(17,7,7) rot=(1,0,0;1.5708rad)
  Radius = 2
FEATURE [Part::Cylinder] Cylinder051  label="Cilindro033"
  Angle = 360
  AttacherType = Attacher::AttachEngine3D
  Height = 14
  Placement = pos=(7,8,0) rot=(0,0,1;0rad)
  Radius = 5
FEATURE [Part::Cut] Cut053
  Base = -> Fusion043
  Tool = -> Cylinder051
FEATURE [Part::Cylinder] Cylinder052  label="Cilindro034"
  Angle = 360
  AttacherType = Attacher::AttachEngine3D
  Height = 32.4
  Placement = pos=(0,3,14) rot=(-1,0,0;1.5708rad)
  Radius = 11.3
FEATURE [Part::Box] Box036  label="Cubo014"
  AttacherType = Attacher::AttachEngine3D
  Height = 14
  Length = 2
  Placement = pos=(6,8,0) rot=(0,0,1;0rad)
  Width = 10
FEATURE [Part::Cut] Cut047
  Base = -> Cut053
  Tool = -> Box036
FEATURE [Part::Cut] Cut054
  Base = -> Cut047
  Tool = -> Cylinder049
FEATURE [Part::Cut] Cut049  label="Sujección barilla eje zZ003"
  Base = -> Cut054
  Placement = pos=(32,135,95) rot=(0,0,-1;1.5708rad)
  Tool = -> Cylinder050
FEATURE [Part::Fuse] Fusion038  label="Barra sujeeción 004"
  Base = -> Cylinder048
  Tool = -> Cut049
FEATURE [Part::Cylinder] Cylinder053  label="Cilindro035"
  Angle = 360
  AttacherType = Attacher::AttachEngine3D
  Height = 80
  Placement = pos=(0,-2,14) rot=(-1,0,0;1.5708rad)
  Radius = 7
FEATURE [Sketcher::SketchObject] Sketch019
  MapMode = 5
  sketch-geometry (22):
    g0: LineSegment StartX=-33 StartY=0 StartZ=0 EndX=33 EndY=0 EndZ=0
    g1: ArcOfCircle CenterX=-33 CenterY=5 CenterZ=0 NormalX=0 NormalY=0 NormalZ=1 AngleXU=0 Radius=5 StartAngle=3.14159 EndAngle=4.71239
    g2: LineSegment StartX=-38 StartY=5 StartZ=0 EndX=-38 EndY=15 EndZ=0
    g3: ArcOfCircle CenterX=-33 CenterY=15 CenterZ=0 NormalX=0 NormalY=0 NormalZ=1 AngleXU=0 Radius=5 StartAngle=1.5708 EndAngle=3.14159
    g4: LineSegment StartX=-33 StartY=20 StartZ=0 EndX=-28 EndY=20 EndZ=0
    g5: ArcOfCircle CenterX=-28 CenterY=25 CenterZ=0 NormalX=0 NormalY=0 NormalZ=1 AngleXU=0 Radius=5 StartAngle=4.71239 EndAngle=6.28319
    g6: LineSegment StartX=-23 StartY=25 StartZ=0 EndX=-23 EndY=69 EndZ=0
    g7: ArcOfCircle CenterX=-18 CenterY=69 CenterZ=0 NormalX=0 NormalY=0 NormalZ=1 AngleXU=0 Radius=5 StartAngle=1.57079 EndAngle=3.14159
    g8: LineSegment StartX=-18 StartY=74 StartZ=0 EndX=18 EndY=74 EndZ=0
    g9: ArcOfCircle CenterX=33 CenterY=5 CenterZ=0 NormalX=0 NormalY=0 NormalZ=1 AngleXU=0 Radius=5 StartAngle=4.71239 EndAngle=6.28319
    g10: LineSegment StartX=38 StartY=5 StartZ=0 EndX=38 EndY=15 EndZ=0
    g11: ArcOfCircle CenterX=18 CenterY=69 CenterZ=0 NormalX=0 NormalY=0 NormalZ=1 AngleXU=0 Radius=5 StartAngle=2.37406e-07 EndAngle=1.5708
    g12: LineSegment StartX=23 StartY=69 StartZ=0 EndX=23 EndY=25 EndZ=0
    g13: ArcOfCircle CenterX=28 CenterY=25 CenterZ=0 NormalX=0 NormalY=0 NormalZ=1 AngleXU=0 Radius=5 StartAngle=3.14159 EndAngle=4.71239
    g14: LineSegment StartX=28 StartY=20 StartZ=0 EndX=33 EndY=20 EndZ=0
    g15: ArcOfCircle CenterX=33 CenterY=15 CenterZ=0 NormalX=0 NormalY=0 NormalZ=1 AngleXU=0 Radius=5 StartAngle=6.28318 EndAngle=7.85398
    g16: Circle CenterX=28 CenterY=10 CenterZ=0 NormalX=0 NormalY=0 NormalZ=1 AngleXU=0 Radius=2.7
    g17: Circle CenterX=-28 CenterY=10 CenterZ=0 NormalX=0 NormalY=0 NormalZ=1 AngleXU=0 Radius=2.7
    g18: Circle CenterX=18 CenterY=64 CenterZ=0 NormalX=0 NormalY=0 NormalZ=1 AngleXU=0 Radius=1.68
    g19: Circle CenterX=18 CenterY=37 CenterZ=0 NormalX=0 NormalY=0 NormalZ=1 AngleXU=0 Radius=1.68
    g20: Circle CenterX=-18 CenterY=37 CenterZ=0 NormalX=0 NormalY=0 NormalZ=1 AngleXU=0 Radius=1.68
    g21: Circle CenterX=-18 CenterY=64 CenterZ=0 NormalX=0 NormalY=0 NormalZ=1 AngleXU=0 Radius=1.68
  constraints (67):
    c: Horizontal(g0)
    c: Vertical(g2)
    c: Coincident(g1,g2)
    c: Coincident(g1,g0)
    c: Coincident(g2,g3)
    c: Tangent(g2,g3)
    c: Tangent(g1,g2)
    c: Tangent(g0,g1)
    c: Horizontal(g4)
    c: Coincident(g3,g4)
    c: Tangent(g4,g5) = -1.5708
    c: Vertical(g6)
    c: Tangent(g4,g3)
    c: Coincident(g6,g7)
    c: Tangent(g7,g6)
    c: Horizontal(g8)
    c: Coincident(g8,g7)
    c: Tangent(g8,g7)
    c: Coincident(g5,g6)
    c: Tangent(g5,g6)
    c: DistanceX(g-1,g6) = -23
    c: Radius(g3) = 5
    c: Radius(g1) = 5
    c: Radius(g5) = 5
    c: Equal(g7,g5)
    c: DistanceY(g3,g0) = -20
    c: DistanceY(g7,g0) = -74
    c: Coincident(g9,g0)
    c: Equal(g9,g1)
    c: Tangent(g9,g0)
    c: DistanceY(g-1,g0) = 0
    c: DistanceX(g2,g5) = 15
    c: Vertical(g10)
    c: Symmetric(g10,g1,g-2)
    c: Coincident(g10,g9)
    c: Symmetric(g10,g2,g-2)
    c: Symmetric(g8,g7,g-2)
    c: Symmetric(g11,g7,g-2)
    c: Coincident(g11,g8)
    c: Vertical(g12)
    c: Coincident(g12,g11)
    c: Coincident(g13,g12)
    c: Tangent(g12,g11)
    c: Tangent(g13,g12)
    c: Horizontal(g14)
    c: Coincident(g13,g14)
    c: Coincident(g15,g14)
    c: Coincident(g15,g10)
    c: Symmetric(g13,g4,g-2)
    c: Symmetric(g14,g3,g-2)
    c: Equal(g13,g5)
    c: Equal(g15,g3)
    c: DistanceY(g16,g0) = -10
    c: DistanceX(g16,g10) = 10
    c: Radius(g16) = 2.7
    c: Symmetric(g17,g16,g-2)
    c: Equal(g17,g16)
    c: DistanceY(g18,g8) = 10
    c: Radius(g18) = 1.68
    c: DistanceX(g18,g11) = 5
    c: DistanceY(g19,g16) = -27
    c: Equal(g19,g18)
    c: DistanceX(g19,g18) = 0
    c: Symmetric(g20,g19,g-2)
    c: Equal(g20,g19)
    c: Equal(g21,g18)
    c: Symmetric(g21,g18,g-2)
FEATURE [Sketcher::SketchObject] Sketch020
  MapMode = 5
  sketch-geometry (22):
    g0: LineSegment StartX=-33 StartY=0 StartZ=0 EndX=33 EndY=0 EndZ=0
    g1: ArcOfCircle CenterX=-33 CenterY=5 CenterZ=0 NormalX=0 NormalY=0 NormalZ=1 AngleXU=0 Radius=5 StartAngle=3.14159 EndAngle=4.71239
    g2: LineSegment StartX=-38 StartY=5 StartZ=0 EndX=-38 EndY=15 EndZ=0
    g3: ArcOfCircle CenterX=-33 CenterY=15 CenterZ=0 NormalX=0 NormalY=0 NormalZ=1 AngleXU=0 Radius=5 StartAngle=1.5708 EndAngle=3.14159
    g4: LineSegment StartX=-33 StartY=20 StartZ=0 EndX=-28 EndY=20 EndZ=0
    g5: ArcOfCircle CenterX=-28 CenterY=25 CenterZ=0 NormalX=0 NormalY=0 NormalZ=1 AngleXU=0 Radius=5 StartAngle=4.71239 EndAngle=6.28319
    g6: LineSegment StartX=-23 StartY=25 StartZ=0 EndX=-23 EndY=69 EndZ=0
    g7: ArcOfCircle CenterX=-18 CenterY=69 CenterZ=0 NormalX=0 NormalY=0 NormalZ=1 AngleXU=0 Radius=5 StartAngle=1.57079 EndAngle=3.14159
    g8: LineSegment StartX=-18 StartY=74 StartZ=0 EndX=18 EndY=74 EndZ=0
    g9: ArcOfCircle CenterX=33 CenterY=5 CenterZ=0 NormalX=0 NormalY=0 NormalZ=1 AngleXU=0 Radius=5 StartAngle=4.71239 EndAngle=6.28319
    g10: LineSegment StartX=38 StartY=5 StartZ=0 EndX=38 EndY=15 EndZ=0
    g11: ArcOfCircle CenterX=18 CenterY=69 CenterZ=0 NormalX=0 NormalY=0 NormalZ=1 AngleXU=0 Radius=5 StartAngle=2.37406e-07 EndAngle=1.5708
    g12: LineSegment StartX=23 StartY=69 StartZ=0 EndX=23 EndY=25 EndZ=0
    g13: ArcOfCircle CenterX=28 CenterY=25 CenterZ=0 NormalX=0 NormalY=0 NormalZ=1 AngleXU=0 Radius=5 StartAngle=3.14159 EndAngle=4.71239
    g14: LineSegment StartX=28 StartY=20 StartZ=0 EndX=33 EndY=20 EndZ=0
    g15: ArcOfCircle CenterX=33 CenterY=15 CenterZ=0 NormalX=0 NormalY=0 NormalZ=1 AngleXU=0 Radius=5 StartAngle=6.28318 EndAngle=7.85398
    g16: Circle CenterX=28 CenterY=10 CenterZ=0 NormalX=0 NormalY=0 NormalZ=1 AngleXU=0 Radius=2.7
    g17: Circle CenterX=-28 CenterY=10 CenterZ=0 NormalX=0 NormalY=0 NormalZ=1 AngleXU=0 Radius=2.7
    g18: Circle CenterX=18 CenterY=64 CenterZ=0 NormalX=0 NormalY=0 NormalZ=1 AngleXU=0 Radius=1.68
    g19: Circle CenterX=18 CenterY=37 CenterZ=0 NormalX=0 NormalY=0 NormalZ=1 AngleXU=0 Radius=1.68
    g20: Circle CenterX=-18 CenterY=37 CenterZ=0 NormalX=0 NormalY=0 NormalZ=1 AngleXU=0 Radius=1.68
    g21: Circle CenterX=-18 CenterY=64 CenterZ=0 NormalX=0 NormalY=0 NormalZ=1 AngleXU=0 Radius=1.68
  constraints (67):
    c: Horizontal(g0)
    c: Vertical(g2)
    c: Coincident(g1,g2)
    c: Coincident(g1,g0)
    c: Coincident(g2,g3)
    c: Tangent(g2,g3)
    c: Tangent(g1,g2)
    c: Tangent(g0,g1)
    c: Horizontal(g4)
    c: Coincident(g3,g4)
    c: Tangent(g4,g5) = -1.5708
    c: Vertical(g6)
    c: Tangent(g4,g3)
    c: Coincident(g6,g7)
    c: Tangent(g7,g6)
    c: Horizontal(g8)
    c: Coincident(g8,g7)
    c: Tangent(g8,g7)
    c: Coincident(g5,g6)
    c: Tangent(g5,g6)
    c: DistanceX(g-1,g6) = -23
    c: Radius(g3) = 5
    c: Radius(g1) = 5
    c: Radius(g5) = 5
    c: Equal(g7,g5)
    c: DistanceY(g3,g0) = -20
    c: DistanceY(g7,g0) = -74
    c: Coincident(g9,g0)
    c: Equal(g9,g1)
    c: Tangent(g9,g0)
    c: DistanceY(g-1,g0) = 0
    c: DistanceX(g2,g5) = 15
    c: Vertical(g10)
    c: Symmetric(g10,g1,g-2)
    c: Coincident(g10,g9)
    c: Symmetric(g10,g2,g-2)
    c: Symmetric(g8,g7,g-2)
    c: Symmetric(g11,g7,g-2)
    c: Coincident(g11,g8)
    c: Vertical(g12)
    c: Coincident(g12,g11)
    c: Coincident(g13,g12)
    c: Tangent(g12,g11)
    c: Tangent(g13,g12)
    c: Horizontal(g14)
    c: Coincident(g13,g14)
    c: Coincident(g15,g14)
    c: Coincident(g15,g10)
    c: Symmetric(g13,g4,g-2)
    c: Symmetric(g14,g3,g-2)
    c: Equal(g13,g5)
    c: Equal(g15,g3)
    c: DistanceY(g16,g0) = -10
    c: DistanceX(g16,g10) = 10
    c: Radius(g16) = 2.7
    c: Symmetric(g17,g16,g-2)
    c: Equal(g17,g16)
    c: DistanceY(g18,g8) = 10
    c: Radius(g18) = 1.68
    c: DistanceX(g18,g11) = 5
    c: DistanceY(g19,g16) = -27
    c: Equal(g19,g18)
    c: DistanceX(g19,g18) = 0
    c: Symmetric(g20,g19,g-2)
    c: Equal(g20,g19)
    c: Equal(g21,g18)
    c: Symmetric(g21,g18,g-2)
FEATURE [Part::Feature] Cylinder054  label="Cilindro036"
  Placement = pos=(0,38.4,14) rot=(-1,0,0;1.5708rad)
  shape: bbox 22.6 x 32.4 x 22.6 mm, 3 faces (baked)
FEATURE [Part::Feature] Cylinder055  label="Cilindro037"
  Placement = pos=(0,38.4,14) rot=(-1,0,0;1.5708rad)
  shape: bbox 22.6 x 32.4 x 22.6 mm, 3 faces (baked)
FEATURE [PartDesign::Pad] Pad008
  Length = 14
  Length2 = 100
  Profile = -> Sketch019
  Type = 0
FEATURE [Part::Cut] Cut052
  Base = -> Pad008
  Tool = -> Cylinder046
FEATURE [Part::Cut] Cut050  label="Z_axis_LM12UU_nut008"
  Base = -> Cut052
  Tool = -> Cylinder054
FEATURE [Part::Cut] Cut048  label="CoreXY_Z_Axix_LM12UU_Nut A003"
  Base = -> Cut050
  Placement = pos=(24,305,330) rot=(0.57735,-0.57735,0.57735;4.18879rad)
  Tool = -> Cylinder047
FEATURE [PartDesign::Pad] Pad009
  Length = 14
  Length2 = 100
  Profile = -> Sketch020
  Type = 0
FEATURE [Part::Cut] Cut051
  Base = -> Pad009
  Tool = -> Cylinder052
FEATURE [Part::Cut] Cut046  label="Z_axis_LM12UU_nut007"
  Base = -> Cut051
  Tool = -> Cylinder055
FEATURE [Part::Cut] Cut045  label="CoreXY_Z_Axix_LM12UU_Nut B003"
  Base = -> Cut046
  Placement = pos=(53,305,330) rot=(0.57735,0.57735,-0.57735;4.18879rad)
  Tool = -> Cylinder053
FEATURE [Part::Fuse] Fusion039  label="sujetacamas izquierdo003"
  Base = -> Cut048
  Placement = pos=(0,-174,0) rot=(0,0,1;0rad)
  Tool = -> Cut045
FEATURE [Part::Feature] Cylinder056  label="Cilindro038"
  Placement = pos=(0,38.4,14) rot=(-1,0,0;1.5708rad)
  shape: bbox 22.6 x 32.4 x 22.6 mm, 3 faces (baked)
FEATURE [Part::Feature] Cylinder057  label="Cilindro039"
  Placement = pos=(0,38.4,14) rot=(-1,0,0;1.5708rad)
  shape: bbox 22.6 x 32.4 x 22.6 mm, 3 faces (baked)
FEATURE [Sketcher::SketchObject] Sketch021
  MapMode = 5
  sketch-geometry (22):
    g0: LineSegment StartX=-33 StartY=0 StartZ=0 EndX=33 EndY=0 EndZ=0
    g1: ArcOfCircle CenterX=-33 CenterY=5 CenterZ=0 NormalX=0 NormalY=0 NormalZ=1 AngleXU=0 Radius=5 StartAngle=3.14159 EndAngle=4.71239
    g2: LineSegment StartX=-38 StartY=5 StartZ=0 EndX=-38 EndY=15 EndZ=0
    g3: ArcOfCircle CenterX=-33 CenterY=15 CenterZ=0 NormalX=0 NormalY=0 NormalZ=1 AngleXU=0 Radius=5 StartAngle=1.5708 EndAngle=3.14159
    g4: LineSegment StartX=-33 StartY=20 StartZ=0 EndX=-28 EndY=20 EndZ=0
    g5: ArcOfCircle CenterX=-28 CenterY=25 CenterZ=0 NormalX=0 NormalY=0 NormalZ=1 AngleXU=0 Radius=5 StartAngle=4.71239 EndAngle=6.28319
    g6: LineSegment StartX=-23 StartY=25 StartZ=0 EndX=-23 EndY=69 EndZ=0
    g7: ArcOfCircle CenterX=-18 CenterY=69 CenterZ=0 NormalX=0 NormalY=0 NormalZ=1 AngleXU=0 Radius=5 StartAngle=1.57079 EndAngle=3.14159
    g8: LineSegment StartX=-18 StartY=74 StartZ=0 EndX=18 EndY=74 EndZ=0
    g9: ArcOfCircle CenterX=33 CenterY=5 CenterZ=0 NormalX=0 NormalY=0 NormalZ=1 AngleXU=0 Radius=5 StartAngle=4.71239 EndAngle=6.28319
    g10: LineSegment StartX=38 StartY=5 StartZ=0 EndX=38 EndY=15 EndZ=0
    g11: ArcOfCircle CenterX=18 CenterY=69 CenterZ=0 NormalX=0 NormalY=0 NormalZ=1 AngleXU=0 Radius=5 StartAngle=2.37406e-07 EndAngle=1.5708
    g12: LineSegment StartX=23 StartY=69 StartZ=0 EndX=23 EndY=25 EndZ=0
    g13: ArcOfCircle CenterX=28 CenterY=25 CenterZ=0 NormalX=0 NormalY=0 NormalZ=1 AngleXU=0 Radius=5 StartAngle=3.14159 EndAngle=4.71239
    g14: LineSegment StartX=28 StartY=20 StartZ=0 EndX=33 EndY=20 EndZ=0
    g15: ArcOfCircle CenterX=33 CenterY=15 CenterZ=0 NormalX=0 NormalY=0 NormalZ=1 AngleXU=0 Radius=5 StartAngle=6.28318 EndAngle=7.85398
    g16: Circle CenterX=28 CenterY=10 CenterZ=0 NormalX=0 NormalY=0 NormalZ=1 AngleXU=0 Radius=2.7
    g17: Circle CenterX=-28 CenterY=10 CenterZ=0 NormalX=0 NormalY=0 NormalZ=1 AngleXU=0 Radius=2.7
    g18: Circle CenterX=18 CenterY=64 CenterZ=0 NormalX=0 NormalY=0 NormalZ=1 AngleXU=0 Radius=1.68
    g19: Circle CenterX=18 CenterY=37 CenterZ=0 NormalX=0 NormalY=0 NormalZ=1 AngleXU=0 Radius=1.68
    g20: Circle CenterX=-18 CenterY=37 CenterZ=0 NormalX=0 NormalY=0 NormalZ=1 AngleXU=0 Radius=1.68
    g21: Circle CenterX=-18 CenterY=64 CenterZ=0 NormalX=0 NormalY=0 NormalZ=1 AngleXU=0 Radius=1.68
  constraints (67):
    c: Horizontal(g0)
    c: Vertical(g2)
    c: Coincident(g1,g2)
    c: Coincident(g1,g0)
    c: Coincident(g2,g3)
    c: Tangent(g2,g3)
    c: Tangent(g1,g2)
    c: Tangent(g0,g1)
    c: Horizontal(g4)
    c: Coincident(g3,g4)
    c: Tangent(g4,g5) = -1.5708
    c: Vertical(g6)
    c: Tangent(g4,g3)
    c: Coincident(g6,g7)
    c: Tangent(g7,g6)
    c: Horizontal(g8)
    c: Coincident(g8,g7)
    c: Tangent(g8,g7)
    c: Coincident(g5,g6)
    c: Tangent(g5,g6)
    c: DistanceX(g-1,g6) = -23
    c: Radius(g3) = 5
    c: Radius(g1) = 5
    c: Radius(g5) = 5
    c: Equal(g7,g5)
    c: DistanceY(g3,g0) = -20
    c: DistanceY(g7,g0) = -74
    c: Coincident(g9,g0)
    c: Equal(g9,g1)
    c: Tangent(g9,g0)
    c: DistanceY(g-1,g0) = 0
    c: DistanceX(g2,g5) = 15
    c: Vertical(g10)
    c: Symmetric(g10,g1,g-2)
    c: Coincident(g10,g9)
    c: Symmetric(g10,g2,g-2)
    c: Symmetric(g8,g7,g-2)
    c: Symmetric(g11,g7,g-2)
    c: Coincident(g11,g8)
    c: Vertical(g12)
    c: Coincident(g12,g11)
    c: Coincident(g13,g12)
    c: Tangent(g12,g11)
    c: Tangent(g13,g12)
    c: Horizontal(g14)
    c: Coincident(g13,g14)
    c: Coincident(g15,g14)
    c: Coincident(g15,g10)
    c: Symmetric(g13,g4,g-2)
    c: Symmetric(g14,g3,g-2)
    c: Equal(g13,g5)
    c: Equal(g15,g3)
    c: DistanceY(g16,g0) = -10
    c: DistanceX(g16,g10) = 10
    c: Radius(g16) = 2.7
    c: Symmetric(g17,g16,g-2)
    c: Equal(g17,g16)
    c: DistanceY(g18,g8) = 10
    c: Radius(g18) = 1.68
    c: DistanceX(g18,g11) = 5
    c: DistanceY(g19,g16) = -27
    c: Equal(g19,g18)
    c: DistanceX(g19,g18) = 0
    c: Symmetric(g20,g19,g-2)
    c: Equal(g20,g19)
    c: Equal(g21,g18)
    c: Symmetric(g21,g18,g-2)
FEATURE [PartDesign::Pad] Pad007
  Length = 14
  Length2 = 100
  Profile = -> Sketch021
  Type = 0
FEATURE [Part::Cut] Cut056
  Base = -> Pad007
  Tool = -> Cylinder043
FEATURE [Part::Cut] Cut044  label="Z_axis_LM12UU_nut006"
  Base = -> Cut056
  Tool = -> Cylinder056
FEATURE [Part::Cut] Cut055  label="CoreXY_Z_Axix_LM12UU_Nut B004"
  Base = -> Cut044
  Placement = pos=(53,305,330) rot=(0.57735,0.57735,-0.57735;4.18879rad)
  Tool = -> Cylinder044
FEATURE [Sketcher::SketchObject] Sketch022
  MapMode = 5
  sketch-geometry (22):
    g0: LineSegment StartX=-33 StartY=0 StartZ=0 EndX=33 EndY=0 EndZ=0
    g1: ArcOfCircle CenterX=-33 CenterY=5 CenterZ=0 NormalX=0 NormalY=0 NormalZ=1 AngleXU=0 Radius=5 StartAngle=3.14159 EndAngle=4.71239
    g2: LineSegment StartX=-38 StartY=5 StartZ=0 EndX=-38 EndY=15 EndZ=0
    g3: ArcOfCircle CenterX=-33 CenterY=15 CenterZ=0 NormalX=0 NormalY=0 NormalZ=1 AngleXU=0 Radius=5 StartAngle=1.5708 EndAngle=3.14159
    g4: LineSegment StartX=-33 StartY=20 StartZ=0 EndX=-28 EndY=20 EndZ=0
    g5: ArcOfCircle CenterX=-28 CenterY=25 CenterZ=0 NormalX=0 NormalY=0 NormalZ=1 AngleXU=0 Radius=5 StartAngle=4.71239 EndAngle=6.28319
    g6: LineSegment StartX=-23 StartY=25 StartZ=0 EndX=-23 EndY=69 EndZ=0
    g7: ArcOfCircle CenterX=-18 CenterY=69 CenterZ=0 NormalX=0 NormalY=0 NormalZ=1 AngleXU=0 Radius=5 StartAngle=1.57079 EndAngle=3.14159
    g8: LineSegment StartX=-18 StartY=74 StartZ=0 EndX=18 EndY=74 EndZ=0
    g9: ArcOfCircle CenterX=33 CenterY=5 CenterZ=0 NormalX=0 NormalY=0 NormalZ=1 AngleXU=0 Radius=5 StartAngle=4.71239 EndAngle=6.28319
    g10: LineSegment StartX=38 StartY=5 StartZ=0 EndX=38 EndY=15 EndZ=0
    g11: ArcOfCircle CenterX=18 CenterY=69 CenterZ=0 NormalX=0 NormalY=0 NormalZ=1 AngleXU=0 Radius=5 StartAngle=2.37406e-07 EndAngle=1.5708
    g12: LineSegment StartX=23 StartY=69 StartZ=0 EndX=23 EndY=25 EndZ=0
    g13: ArcOfCircle CenterX=28 CenterY=25 CenterZ=0 NormalX=0 NormalY=0 NormalZ=1 AngleXU=0 Radius=5 StartAngle=3.14159 EndAngle=4.71239
    g14: LineSegment StartX=28 StartY=20 StartZ=0 EndX=33 EndY=20 EndZ=0
    g15: ArcOfCircle CenterX=33 CenterY=15 CenterZ=0 NormalX=0 NormalY=0 NormalZ=1 AngleXU=0 Radius=5 StartAngle=6.28318 EndAngle=7.85398
    g16: Circle CenterX=28 CenterY=10 CenterZ=0 NormalX=0 NormalY=0 NormalZ=1 AngleXU=0 Radius=2.7
    g17: Circle CenterX=-28 CenterY=10 CenterZ=0 NormalX=0 NormalY=0 NormalZ=1 AngleXU=0 Radius=2.7
    g18: Circle CenterX=18 CenterY=64 CenterZ=0 NormalX=0 NormalY=0 NormalZ=1 AngleXU=0 Radius=1.68
    g19: Circle CenterX=18 CenterY=37 CenterZ=0 NormalX=0 NormalY=0 NormalZ=1 AngleXU=0 Radius=1.68
    g20: Circle CenterX=-18 CenterY=37 CenterZ=0 NormalX=0 NormalY=0 NormalZ=1 AngleXU=0 Radius=1.68
    g21: Circle CenterX=-18 CenterY=64 CenterZ=0 NormalX=0 NormalY=0 NormalZ=1 AngleXU=0 Radius=1.68
  constraints (67):
    c: Horizontal(g0)
    c: Vertical(g2)
    c: Coincident(g1,g2)
    c: Coincident(g1,g0)
    c: Coincident(g2,g3)
    c: Tangent(g2,g3)
    c: Tangent(g1,g2)
    c: Tangent(g0,g1)
    c: Horizontal(g4)
    c: Coincident(g3,g4)
    c: Tangent(g4,g5) = -1.5708
    c: Vertical(g6)
    c: Tangent(g4,g3)
    c: Coincident(g6,g7)
    c: Tangent(g7,g6)
    c: Horizontal(g8)
    c: Coincident(g8,g7)
    c: Tangent(g8,g7)
    c: Coincident(g5,g6)
    c: Tangent(g5,g6)
    c: DistanceX(g-1,g6) = -23
    c: Radius(g3) = 5
    c: Radius(g1) = 5
    c: Radius(g5) = 5
    c: Equal(g7,g5)
    c: DistanceY(g3,g0) = -20
    c: DistanceY(g7,g0) = -74
    c: Coincident(g9,g0)
    c: Equal(g9,g1)
    c: Tangent(g9,g0)
    c: DistanceY(g-1,g0) = 0
    c: DistanceX(g2,g5) = 15
    c: Vertical(g10)
    c: Symmetric(g10,g1,g-2)
    c: Coincident(g10,g9)
    c: Symmetric(g10,g2,g-2)
    c: Symmetric(g8,g7,g-2)
    c: Symmetric(g11,g7,g-2)
    c: Coincident(g11,g8)
    c: Vertical(g12)
    c: Coincident(g12,g11)
    c: Coincident(g13,g12)
    c: Tangent(g12,g11)
    c: Tangent(g13,g12)
    c: Horizontal(g14)
    c: Coincident(g13,g14)
    c: Coincident(g15,g14)
    c: Coincident(g15,g10)
    c: Symmetric(g13,g4,g-2)
    c: Symmetric(g14,g3,g-2)
    c: Equal(g13,g5)
    c: Equal(g15,g3)
    c: DistanceY(g16,g0) = -10
    c: DistanceX(g16,g10) = 10
    c: Radius(g16) = 2.7
    c: Symmetric(g17,g16,g-2)
    c: Equal(g17,g16)
    c: DistanceY(g18,g8) = 10
    c: Radius(g18) = 1.68
    c: DistanceX(g18,g11) = 5
    c: DistanceY(g19,g16) = -27
    c: Equal(g19,g18)
    c: DistanceX(g19,g18) = 0
    c: Symmetric(g20,g19,g-2)
    c: Equal(g20,g19)
    c: Equal(g21,g18)
    c: Symmetric(g21,g18,g-2)
FEATURE [PartDesign::Pad] Pad006
  Length = 14
  Length2 = 100
  Profile = -> Sketch022
  Type = 0
FEATURE [Part::Cut] Cut059
  Base = -> Pad006
  Tool = -> Cylinder042
FEATURE [Part::Cut] Cut057  label="Z_axis_LM12UU_nut009"
  Base = -> Cut059
  Tool = -> Cylinder057
FEATURE [Part::Cut] Cut058  label="CoreXY_Z_Axix_LM12UU_Nut A004"
  Base = -> Cut057
  Placement = pos=(24,305,330) rot=(0.57735,-0.57735,0.57735;4.18879rad)
  Tool = -> Cylinder045
FEATURE [Part::Fuse] Fusion037  label="sujetacamas izquierdo002"
  Base = -> Cut058
  Placement = pos=(0,-174,0) rot=(0,0,1;0rad)
  Tool = -> Cut055
FEATURE [Part::Cylinder] Cylinder058  label="Tornillo sin fin004"
  Angle = 360
  AttacherType = Attacher::AttachEngine3D
  Height = 510
  Placement = pos=(40,130,90) rot=(0,0,1;0rad)
  Radius = 5
FEATURE [Part::Cylinder] Cylinder059  label="Cilindro040"
  Angle = 360
  AttacherType = Attacher::AttachEngine3D
  Height = 10
  Placement = pos=(-3,7,7) rot=(1,0,0;1.5708rad)
  Radius = 2
FEATURE [Part::Box] Box037  label="Cubo015"
  AttacherType = Attacher::AttachEngine3D
  Height = 14
  Length = 26
  Placement = pos=(-6,0,0) rot=(0,0,1;0rad)
  Width = 2
FEATURE [Part::Cylinder] Cylinder060  label="Cilindro041"
  Angle = 360
  AttacherType = Attacher::AttachEngine3D
  Height = 10
  Placement = pos=(17,7,7) rot=(1,0,0;1.5708rad)
  Radius = 2
FEATURE [Part::Cylinder] Cylinder061  label="Cilindro042"
  Angle = 360
  AttacherType = Attacher::AttachEngine3D
  Height = 14
  Placement = pos=(7,8,0) rot=(0,0,1;0rad)
  Radius = 5
FEATURE [Part::Box] Box038  label="Cubo016"
  AttacherType = Attacher::AttachEngine3D
  Height = 14
  Length = 2
  Placement = pos=(6,8,0) rot=(0,0,1;0rad)
  Width = 10
FEATURE [Part::Box] Box039  label="Cubo017"
  AttacherType = Attacher::AttachEngine3D
  Height = 14
  Length = 14
  Width = 14
FEATURE [Part::MultiFuse] Fusion044
  Shapes = -> [Box039,Box037]
FEATURE [Part::Cut] Cut040
  Base = -> Fusion044
  Tool = -> Cylinder061
FEATURE [Part::Cut] Cut043
  Base = -> Cut040
  Tool = -> Box038
FEATURE [Part::Cut] Cut042
  Base = -> Cut043
  Tool = -> Cylinder059
FEATURE [Part::Cut] Cut041  label="Sujección barilla eje zZ002"
  Base = -> Cut042
  Placement = pos=(32,135,95) rot=(0,0,-1;1.5708rad)
  Tool = -> Cylinder060
FEATURE [Part::Fuse] Fusion036  label="Barra sujeeción 003"
  Base = -> Cylinder058
  Tool = -> Cut041
FEATURE [Part::Fuse] Fusion041  label="Sujetacamas izq 004"
  Base = -> Fusion037
  Tool = -> Fusion036
FEATURE [Part::Fuse] Fusion045  label="Soporte Varillas del carrito"
  Base = -> Fusion026
  Tool = -> Fusion027
FEATURE [Part::Cylinder] Cylinder026  label="Barra del carrito 2"
  Angle = 360
  AttacherType = Attacher::AttachEngine3D
  Height = 630
  Placement = pos=(36,340,626) rot=(0.707107,0,0.707107;3.14159rad)
  Radius = 6
FEATURE [Part::Cylinder] Cylinder016  label="Barra del carrito 1"
  Angle = 360
  AttacherType = Attacher::AttachEngine3D
  Height = 630
  Placement = pos=(38,290,624) rot=(0.707107,0,0.707107;3.14159rad)
  Radius = 6
FEATURE [Part::Fuse] Fusion046
  Base = -> Cylinder026
  Tool = -> Cylinder016
FEATURE [Part::Cylinder] Cylinder012  label="Cilindro001"
  Angle = 360
  AttacherType = Attacher::AttachEngine3D
  Height = 540
  Placement = pos=(667,570,625) rot=(1,0,0;1.5708rad)
  Radius = 5
FEATURE [Part::Cylinder] Cylinder011  label="Cilindro"
  Angle = 360
  AttacherType = Attacher::AttachEngine3D
  Height = 540
  Placement = pos=(42,570,625) rot=(1,0,0;1.5708rad)
  Radius = 5
FEATURE [Part::Fuse] Fusion047
  Base = -> Cylinder012
  Tool = -> Cylinder011
FEATURE [Part::FeaturePython] Screw001  label="M2.5x25-Screw006"  # Fasteners workbench fastener (typed FeaturePython)
  Placement = pos=(-15.5,-15.5,4) rot=(0,1,0;3.14159rad)
  diameter = 3
  invert = true
  length = 10
  matchOuter = true
  offset = 1
  thread = true
  type = 16
FEATURE [Part::FeaturePython] Screw002  label="M2.5x25-Screw005"  # Fasteners workbench fastener (typed FeaturePython)
  Placement = pos=(15.5,-15.5,4) rot=(0,1,0;3.14159rad)
  diameter = 3
  invert = true
  length = 10
  matchOuter = true
  offset = 1
  thread = true
  type = 16
FEATURE [Part::FeaturePython] Screw  label="M2.5x25-Screw"  # Fasteners workbench fastener (typed FeaturePython)
  Placement = pos=(15.5,15.5,4) rot=(0,1,0;3.14159rad)
  diameter = 3
  invert = true
  length = 10
  matchOuter = true
  offset = 1
  thread = true
  type = 16
FEATURE [PartDesign::Body] Body004  label="Stator"
  Origin = -> Origin010
FEATURE [Sketcher::SketchObject] Sketch024
  MapMode = 5
  Support = -> [XY_Plane001]
  sketch-geometry (4):
    g0: LineSegment StartX=-21.15 StartY=21.15 StartZ=0 EndX=21.15 EndY=21.15 EndZ=0
    g1: LineSegment StartX=21.15 StartY=21.15 StartZ=0 EndX=21.15 EndY=-21.15 EndZ=0
    g2: LineSegment StartX=21.15 StartY=-21.15 StartZ=0 EndX=-21.15 EndY=-21.15 EndZ=0
    g3: LineSegment StartX=-21.15 StartY=-21.15 StartZ=0 EndX=-21.15 EndY=21.15 EndZ=0
  constraints (11):
    c: Coincident(g0,g1)
    c: Coincident(g1,g2)
    c: Coincident(g2,g3)
    c: Coincident(g3,g0)
    c: Horizontal(g0)
    c: Horizontal(g2)
    c: Vertical(g1)
    c: Vertical(g3)
    c: Symmetric(g0,g1,g-1)
    c: DistanceX(g0,g0) = 42.3
    c: Equal(g0,g3)
FEATURE [Sketcher::SketchObject] Sketch025
  MapMode = 5
  Support = -> [XY_Plane003]
  sketch-geometry (4):
    g0: LineSegment StartX=-21.15 StartY=21.15 StartZ=0 EndX=21.15 EndY=21.15 EndZ=0
    g1: LineSegment StartX=21.15 StartY=21.15 StartZ=0 EndX=21.15 EndY=-21.15 EndZ=0
    g2: LineSegment StartX=21.15 StartY=-21.15 StartZ=0 EndX=-21.15 EndY=-21.15 EndZ=0
    g3: LineSegment StartX=-21.15 StartY=-21.15 StartZ=0 EndX=-21.15 EndY=21.15 EndZ=0
  constraints (11):
    c: Coincident(g0,g1)
    c: Coincident(g1,g2)
    c: Coincident(g2,g3)
    c: Coincident(g3,g0)
    c: Horizontal(g0)
    c: Horizontal(g2)
    c: Vertical(g1)
    c: Vertical(g3)
    c: Symmetric(g0,g1,g-1)
    c: DistanceX(g0,g0) = 42.3
    c: Equal(g0,g3)
FEATURE [PartDesign::Pad] Pad003
  Length = 7.75
  Length2 = 100
  Profile = -> Sketch025
  Refine = true
  Type = 0
FEATURE [PartDesign::Chamfer] Chamfer007
  Base = -> Pad003 [Edge8,Edge5,Edge2,Edge1]
  BaseFeature = -> Pad003
  Size = 5
FEATURE [PartDesign::Fillet] Fillet006
  Base = -> Chamfer007 [Edge22,Edge24,Edge23,Edge21,Edge12,Edge2,Edge3,Edge14]
  BaseFeature = -> Chamfer007
  Radius = 2
FEATURE [PartDesign::Pad] Pad011
  Length = 9.6
  Length2 = 100
  Profile = -> Sketch024
  Refine = true
  Type = 0
FEATURE [Sketcher::SketchObject] Sketch023
  ExternalGeometry = -> [Pad011]
  MapMode = 5
  Support = -> [XY_Plane001]
  sketch-geometry (4):
    g0: LineSegment StartX=21.15 StartY=8.2 StartZ=0 EndX=25.45 EndY=8.2 EndZ=0
    g1: LineSegment StartX=25.45 StartY=8.2 StartZ=0 EndX=25.45 EndY=-8.2 EndZ=0
    g2: LineSegment StartX=25.45 StartY=-8.2 StartZ=0 EndX=21.15 EndY=-8.2 EndZ=0
    g3: LineSegment StartX=21.15 StartY=-8.2 StartZ=0 EndX=21.15 EndY=8.2 EndZ=0
  constraints (11):
    c: Coincident(g0,g1)
    c: Coincident(g1,g2)
    c: Coincident(g2,g3)
    c: Coincident(g3,g0)
    c: Horizontal(g0)
    c: Horizontal(g2)
    c: Vertical(g3)
    c: PointOnObject(g0,g-3)
    c: Symmetric(g1,g0,g-1)
    c: DistanceX(g0,g0) = 4.3
    c: DistanceY(g1,g1) = 16.4
FEATURE [PartDesign::Pad] Pad010
  BaseFeature = -> Pad011
  Length = 3.6
  Length2 = 100
  Profile = -> Sketch023
  Refine = true
  Type = 0
FEATURE [PartDesign::Chamfer] Chamfer006
  Base = -> Pad010 [Edge13,Edge5,Edge1,Edge2]
  BaseFeature = -> Pad010
  Size = 5
FEATURE [PartDesign::Fillet] Fillet005
  Base = -> Chamfer006 [Edge33,Edge28,Edge18,Edge3,Edge2,Edge16,Edge30,Edge25]
  BaseFeature = -> Chamfer006
  Radius = 2
FEATURE [Sketcher::SketchObject] Sketch027
  MapMode = 5
  Support = -> [XY_Plane002]
  sketch-geometry (4):
    g0: LineSegment StartX=-21 StartY=21 StartZ=0 EndX=21 EndY=21 EndZ=0
    g1: LineSegment StartX=21 StartY=21 StartZ=0 EndX=21 EndY=-21 EndZ=0
    g2: LineSegment StartX=21 StartY=-21 StartZ=0 EndX=-21 EndY=-21 EndZ=0
    g3: LineSegment StartX=-21 StartY=-21 StartZ=0 EndX=-21 EndY=21 EndZ=0
  constraints (11):
    c: Coincident(g0,g1)
    c: Coincident(g1,g2)
    c: Coincident(g2,g3)
    c: Coincident(g3,g0)
    c: Horizontal(g0)
    c: Horizontal(g2)
    c: Vertical(g1)
    c: Vertical(g3)
    c: DistanceX(g0,g0) = 42
    c: Symmetric(g0,g1,g-1)
    c: Equal(g0,g3)
FEATURE [PartDesign::Pad] Pad002
  Length = 22.75
  Length2 = 100
  Profile = -> Sketch027
  Refine = true
  Type = 0
FEATURE [PartDesign::Chamfer] Chamfer005
  Base = -> Pad002 [Edge8,Edge1,Edge5,Edge2]
  BaseFeature = -> Pad002
  Size = 7.5
FEATURE [Sketcher::SketchObject] Sketch030
  MapMode = 5
  Support = -> [XY_Plane004]
  sketch-geometry (1):
    g0: Circle CenterX=0 CenterY=0 CenterZ=0 NormalX=0 NormalY=0 NormalZ=1 AngleXU=0 Radius=2.5
  constraints (2):
    c: Coincident(g0,g-1)
    c: Radius(g0) = 2.5
FEATURE [Sketcher::SketchObject] Sketch031
  MapMode = 5
  Placement = pos=(0,0,0) rot=(1,0,0;3.14159rad)
  Support = -> [Fillet005]
  sketch-geometry (8):
    g0: LineSegment [constr] StartX=-15.5 StartY=15.5 StartZ=0 EndX=15.5 EndY=15.5 EndZ=0
    g1: LineSegment [constr] StartX=15.5 StartY=15.5 StartZ=0 EndX=15.5 EndY=-15.5 EndZ=0
    g2: LineSegment [constr] StartX=15.5 StartY=-15.5 StartZ=0 EndX=-15.5 EndY=-15.5 EndZ=0
    g3: LineSegment [constr] StartX=-15.5 StartY=-15.5 StartZ=0 EndX=-15.5 EndY=15.5 EndZ=0
    g4: Circle CenterX=-15.5 CenterY=15.5 CenterZ=0 NormalX=0 NormalY=0 NormalZ=1 AngleXU=0 Radius=1.225
    g5: Circle CenterX=15.5 CenterY=15.5 CenterZ=0 NormalX=0 NormalY=0 NormalZ=1 AngleXU=0 Radius=1.225
    g6: Circle CenterX=15.5 CenterY=-15.5 CenterZ=0 NormalX=0 NormalY=0 NormalZ=1 AngleXU=0 Radius=1.225
    g7: Circle CenterX=-15.5 CenterY=-15.5 CenterZ=0 NormalX=0 NormalY=0 NormalZ=1 AngleXU=0 Radius=1.225
  constraints (19):
    c: Coincident(g0,g1)
    c: Coincident(g1,g2)
    c: Coincident(g2,g3)
    c: Coincident(g3,g0)
    c: Horizontal(g0)
    c: Horizontal(g2)
    c: Vertical(g1)
    c: Vertical(g3)
    c: Symmetric(g0,g1,g-1)
    c: DistanceX(g0,g0) = 31
    c: Equal(g3,g0)
    c: Coincident(g4,g0)
    c: Coincident(g5,g0)
    c: Coincident(g6,g1)
    c: Coincident(g7,g2)
    c: Equal(g6,g5)
    c: Equal(g5,g4)
    c: Equal(g4,g7)
    c: Radius(g4) = 1.225
FEATURE [PartDesign::Hole] Hole
  BaseFeature = -> Fillet005
  Depth = 25
  DepthType = 0
  Diameter = 3
  DrillPoint = 1
  DrillPointAngle = 118
  HoleCutCountersinkAngle = 90
  HoleCutDepth = 5
  HoleCutDiameter = 5
  HoleCutType = 1
  ModelActualThread = false
  Profile = -> Sketch031
  Refine = true
  Tapered = false
  TaperedAngle = 90
  ThreadAngle = 0
  ThreadClass = 0
  ThreadCutOffInner = 0
  ThreadCutOffOuter = 0
  ThreadDirection = 0
  ThreadFit = 0
  ThreadPitch = 0
  ThreadSize = 0
  ThreadType = 0
  Threaded = false
FEATURE [Sketcher::SketchObject] Sketch032
  MapMode = 5
  Placement = pos=(0,0,0) rot=(1,0,0;3.14159rad)
  Support = -> [Chamfer005]
  sketch-geometry (8):
    g0: LineSegment [constr] StartX=-15.5 StartY=15.5 StartZ=0 EndX=15.5 EndY=15.5 EndZ=0
    g1: LineSegment [constr] StartX=15.5 StartY=15.5 StartZ=0 EndX=15.5 EndY=-15.5 EndZ=0
    g2: LineSegment [constr] StartX=15.5 StartY=-15.5 StartZ=0 EndX=-15.5 EndY=-15.5 EndZ=0
    g3: LineSegment [constr] StartX=-15.5 StartY=-15.5 StartZ=0 EndX=-15.5 EndY=15.5 EndZ=0
    g4: Circle CenterX=-15.5 CenterY=15.5 CenterZ=0 NormalX=0 NormalY=0 NormalZ=1 AngleXU=0 Radius=1.22
    g5: Circle CenterX=15.5 CenterY=15.5 CenterZ=0 NormalX=0 NormalY=0 NormalZ=1 AngleXU=0 Radius=1.22
    g6: Circle CenterX=15.5 CenterY=-15.5 CenterZ=0 NormalX=0 NormalY=0 NormalZ=1 AngleXU=0 Radius=1.22
    g7: Circle CenterX=-15.5 CenterY=-15.5 CenterZ=0 NormalX=0 NormalY=0 NormalZ=1 AngleXU=0 Radius=1.22
  constraints (19):
    c: Coincident(g0,g1)
    c: Coincident(g1,g2)
    c: Coincident(g2,g3)
    c: Coincident(g3,g0)
    c: Horizontal(g0)
    c: Horizontal(g2)
    c: Vertical(g1)
    c: Vertical(g3)
    c: Equal(g0,g3)
    c: Symmetric(g0,g1,g-1)
    c: DistanceX(g0,g0) = 31
    c: Coincident(g4,g0)
    c: Coincident(g5,g0)
    c: Coincident(g6,g1)
    c: Coincident(g7,g2)
    c: Equal(g6,g5)
    c: Equal(g5,g4)
    c: Equal(g4,g7)
    c: Radius(g4) = 1.22
FEATURE [PartDesign::Pocket] Pocket001
  BaseFeature = -> Chamfer005
  Length = 5
  Length2 = 100
  Profile = -> Sketch032
  Refine = true
  Type = 1
FEATURE [Sketcher::SketchObject] Sketch035
  MapMode = 5
  Placement = pos=(0,0,0) rot=(0.57735,0.57735,0.57735;2.0944rad)
  Support = -> [YZ_Plane013]
  sketch-geometry (4):
    g0: LineSegment StartX=-5.5 StartY=1 StartZ=0 EndX=5.5 EndY=1 EndZ=0
    g1: LineSegment StartX=5.5 StartY=1 StartZ=0 EndX=5.5 EndY=0 EndZ=0
    g2: LineSegment StartX=5.5 StartY=0 StartZ=0 EndX=-5.5 EndY=0 EndZ=0
    g3: LineSegment StartX=-5.5 StartY=0 StartZ=0 EndX=-5.5 EndY=1 EndZ=0
  constraints (11):
    c: Coincident(g0,g1)
    c: Coincident(g1,g2)
    c: Coincident(g2,g3)
    c: Coincident(g3,g0)
    c: Horizontal(g0)
    c: Vertical(g1)
    c: Vertical(g3)
    c: PointOnObject(g1,g-1)
    c: DistanceY(g3,g3) = 1
    c: DistanceX(g2,g2) = 11
    c: Symmetric(g1,g2,g-2)
FEATURE [PartDesign::Pad] Pad012
  Length = 60
  Length2 = 100
  Profile = -> Sketch030
  Refine = true
  Type = 0
FEATURE [Sketcher::SketchObject] Sketch026
  MapMode = 5
  Placement = pos=(0,0,60) rot=(0,0,1;0rad)
  Support = -> [Pad012]
  sketch-geometry (4):
    g0: LineSegment StartX=2 StartY=2 StartZ=0 EndX=6 EndY=2 EndZ=0
    g1: LineSegment StartX=6 StartY=2 StartZ=0 EndX=6 EndY=-2 EndZ=0
    g2: LineSegment StartX=6 StartY=-2 StartZ=0 EndX=2 EndY=-2 EndZ=0
    g3: LineSegment StartX=2 StartY=-2 StartZ=0 EndX=2 EndY=2 EndZ=0
  constraints (11):
    c: Coincident(g0,g1)
    c: Coincident(g1,g2)
    c: Coincident(g2,g3)
    c: Coincident(g3,g0)
    c: Horizontal(g0)
    c: Horizontal(g2)
    c: Vertical(g1)
    c: Symmetric(g2,g0,g-1)
    c: DistanceX(g-1,g0) = 2
    c: Equal(g0,g3)
    c: DistanceX(g0,g0) = 4
FEATURE [PartDesign::Pocket] Pocket005
  BaseFeature = -> Pad012
  Length = 16
  Length2 = 100
  Profile = -> Sketch026
  Refine = true
  Type = 0
FEATURE [PartDesign::Chamfer] Chamfer008
  Base = -> Pocket005 [Edge3,Edge5,Edge9]
  BaseFeature = -> Pocket005
  Size = 0.3
FEATURE [PartDesign::Body] Body003  label="Rotor"
  Group = -> [Sketch030,Pad012,Sketch026,Pocket005,Chamfer008]
  Origin = -> Origin004
  Placement = pos=(0,0,2) rot=(0,0,1;0rad)
  Tip = -> Chamfer008
FEATURE [App::Part] Part004  label="Rotor001"
  Group = -> [Body003]
  Origin = -> Origin008
FEATURE [Sketcher::SketchObject] Sketch037
  MapMode = 5
  Placement = pos=(0,0,22.75) rot=(0,0,1;0rad)
  Support = -> [Pocket001]
  sketch-geometry (1):
    g0: Circle CenterX=0 CenterY=0 CenterZ=0 NormalX=0 NormalY=0 NormalZ=1 AngleXU=0 Radius=18
  constraints (2):
    c: Coincident(g0,g-1)
    c: Radius(g0) = 18
FEATURE [Sketcher::SketchObject] Sketch038
  MapMode = 5
  Placement = pos=(0,0,7.75) rot=(0,0,1;0rad)
  Support = -> [Fillet006]
  sketch-geometry (8):
    g0: LineSegment [constr] StartX=-15.5 StartY=15.5 StartZ=0 EndX=15.5 EndY=15.5 EndZ=0
    g1: LineSegment [constr] StartX=15.5 StartY=15.5 StartZ=0 EndX=15.5 EndY=-15.5 EndZ=0
    g2: LineSegment [constr] StartX=15.5 StartY=-15.5 StartZ=0 EndX=-15.5 EndY=-15.5 EndZ=0
    g3: LineSegment [constr] StartX=-15.5 StartY=-15.5 StartZ=0 EndX=-15.5 EndY=15.5 EndZ=0
    g4: Circle CenterX=-15.5 CenterY=15.5 CenterZ=0 NormalX=0 NormalY=0 NormalZ=1 AngleXU=0 Radius=1.225
    g5: Circle CenterX=15.5 CenterY=15.5 CenterZ=0 NormalX=0 NormalY=0 NormalZ=1 AngleXU=0 Radius=1.225
    g6: Circle CenterX=15.5 CenterY=-15.5 CenterZ=0 NormalX=0 NormalY=0 NormalZ=1 AngleXU=0 Radius=1.225
    g7: Circle CenterX=-15.5 CenterY=-15.5 CenterZ=0 NormalX=0 NormalY=0 NormalZ=1 AngleXU=0 Radius=1.225
  constraints (19):
    c: Coincident(g0,g1)
    c: Coincident(g1,g2)
    c: Coincident(g2,g3)
    c: Coincident(g3,g0)
    c: Horizontal(g0)
    c: Horizontal(g2)
    c: Vertical(g1)
    c: Vertical(g3)
    c: Equal(g0,g3)
    c: Symmetric(g0,g1,g-1)
    c: DistanceX(g0,g0) = 31
    c: Coincident(g4,g0)
    c: Coincident(g7,g2)
    c: Coincident(g0,g5)
    c: Coincident(g1,g6)
    c: Equal(g7,g4)
    c: Equal(g4,g5)
    c: Equal(g5,g6)
    c: Radius(g4) = 1.225
FEATURE [PartDesign::Pocket] Pocket002
  BaseFeature = -> Fillet006
  Length = 5
  Length2 = 100
  Profile = -> Sketch038
  Refine = true
  Type = 1
FEATURE [Sketcher::SketchObject] Sketch028
  MapMode = 5
  Placement = pos=(0,0,7.75) rot=(0,0,1;0rad)
  Support = -> [Pocket002]
  sketch-geometry (1):
    g0: Circle CenterX=0 CenterY=0 CenterZ=0 NormalX=0 NormalY=0 NormalZ=1 AngleXU=0 Radius=14
  constraints (2):
    c: Coincident(g0,g-1)
    c: Radius(g0) = 14
FEATURE [PartDesign::Pocket] Pocket003
  BaseFeature = -> Pocket002
  Length = 1
  Length2 = 100
  Profile = -> Sketch028
  Refine = true
  Type = 0
FEATURE [Sketcher::SketchObject] Sketch029
  MapMode = 5
  Placement = pos=(0,0,6.75) rot=(0,0,1;0rad)
  Support = -> [Pocket003]
  sketch-geometry (1):
    g0: Circle CenterX=0 CenterY=0 CenterZ=0 NormalX=0 NormalY=0 NormalZ=1 AngleXU=0 Radius=11
  constraints (2):
    c: Coincident(g0,g-1)
    c: Radius(g0) = 11
FEATURE [PartDesign::Pad] Pad014
  BaseFeature = -> Pocket003
  Length = 3
  Length2 = 100
  Profile = -> Sketch029
  Refine = true
  Type = 0
FEATURE [PartDesign::Draft] Draft
  Angle = 10
  Base = -> Pad014 [Face25]
  BaseFeature = -> Pad014
  NeutralPlane = -> Pad014 [Face24]
FEATURE [Sketcher::SketchObject] Sketch039
  MapMode = 5
  Placement = pos=(0,0,9.75) rot=(0,0,1;0rad)
  Support = -> [Draft]
  sketch-geometry (1):
    g0: Circle CenterX=0 CenterY=0 CenterZ=0 NormalX=0 NormalY=0 NormalZ=1 AngleXU=0 Radius=5
  constraints (2):
    c: Coincident(g0,g-1)
    c: Radius(g0) = 5
FEATURE [PartDesign::Pocket] Pocket004
  BaseFeature = -> Draft
  Length = 8
  Length2 = 100
  Profile = -> Sketch039
  Refine = true
  Type = 1
FEATURE [Sketcher::SketchObject] Sketch036
  MapMode = 5
  Placement = pos=(0,0,0) rot=(1,0,0;3.14159rad)
  Support = -> [Pocket004]
  sketch-geometry (1):
    g0: Circle CenterX=0 CenterY=0 CenterZ=0 NormalX=0 NormalY=0 NormalZ=1 AngleXU=0 Radius=15.35
  constraints (2):
    c: Coincident(g0,g-1)
    c: Radius(g0) = 15.35
FEATURE [PartDesign::Pocket] Pocket
  BaseFeature = -> Pocket001
  Length = 5
  Length2 = 100
  Profile = -> Sketch037
  Refine = true
  Type = 1
FEATURE [PartDesign::Body] Body001
  Group = -> [Sketch027,Pad002,Chamfer005,Sketch032,Pocket001,Sketch037,Pocket]
  Origin = -> Origin002
  Placement = pos=(0,0,9.6) rot=(0,0,1;0rad)
  Tip = -> Pocket
FEATURE [App::Part] Part002  label="Body"
  Group = -> [Body001,Body004]
  Origin = -> Origin006
FEATURE [Part::FeaturePython] Screw003  label="M2.5x25-Screw007"  # Fasteners workbench fastener (typed FeaturePython)
  Placement = pos=(-15.5,15.5,4) rot=(0,1,0;3.14159rad)
  diameter = 3
  invert = true
  length = 10
  matchOuter = true
  offset = 1
  thread = true
  type = 16
FEATURE [App::Part] Part005  label="Screw"
  Group = -> [Screw,Screw001,Screw002,Screw003]
  Origin = -> Origin009
FEATURE [Sketcher::SketchObject] Sketch040
  ExternalGeometry = -> [Hole]
  MapMode = 5
  Placement = pos=(21.15,0,0) rot=(0.57735,0.57735,0.57735;2.0944rad)
  Support = -> [Hole]
  sketch-geometry (4):
    g0: LineSegment StartX=-8.2 StartY=3.6 StartZ=0 EndX=8.2 EndY=3.6 EndZ=0
    g1: LineSegment StartX=8.2 StartY=3.6 StartZ=0 EndX=8.2 EndY=9.6 EndZ=0
    g2: LineSegment StartX=8.2 StartY=9.6 StartZ=0 EndX=-8.2 EndY=9.6 EndZ=0
    g3: LineSegment StartX=-8.2 StartY=9.6 StartZ=0 EndX=-8.2 EndY=3.6 EndZ=0
  constraints (10):
    c: Coincident(g0,g1)
    c: Coincident(g1,g2)
    c: Coincident(g2,g3)
    c: Coincident(g3,g0)
    c: Horizontal(g0)
    c: Vertical(g1)
    c: Vertical(g3)
    c: Coincident(g0,g-3)
    c: PointOnObject(g1,g-5)
    c: Symmetric(g2,g1,g-2)
FEATURE [PartDesign::Pocket] Pocket006
  BaseFeature = -> Hole
  Length = 4
  Length2 = 100
  Profile = -> Sketch040
  Refine = true
  Type = 0
FEATURE [PartDesign::Body] Body  label="Aluminium rear001"
  Group = -> [Sketch024,Pad011,Sketch023,Pad010,Chamfer006,Fillet005,Sketch031,Hole,Sketch040,Pocket006]
  Origin = -> Origin001
  Tip = -> Pocket006
FEATURE [App::Part] Part001  label="Aluminium rear"
  Group = -> [Body]
  Origin = -> Origin005
FEATURE [Sketcher::SketchObject] Sketch041
  MapMode = 5
  Placement = pos=(0,0,0) rot=(0.57735,0.57735,0.57735;2.0944rad)
  Support = -> [YZ_Plane012]
  sketch-geometry (4):
    g0: LineSegment StartX=-7.5 StartY=0 StartZ=0 EndX=7.5 EndY=0 EndZ=0
    g1: LineSegment StartX=7.5 StartY=0 StartZ=0 EndX=7.5 EndY=5 EndZ=0
    g2: LineSegment StartX=7.5 StartY=5 StartZ=0 EndX=-7.5 EndY=5 EndZ=0
    g3: LineSegment StartX=-7.5 StartY=5 StartZ=0 EndX=-7.5 EndY=0 EndZ=0
  constraints (11):
    c: Coincident(g0,g1)
    c: Coincident(g1,g2)
    c: Coincident(g2,g3)
    c: Coincident(g3,g0)
    c: Horizontal(g0)
    c: Horizontal(g2)
    c: Vertical(g1)
    c: Vertical(g3)
    c: Symmetric(g0,g0,g-1)
    c: DistanceX(g0,g0) = 15
    c: DistanceY(g3,g3) = 5
FEATURE [PartDesign::Pad] Pad013
  Length = 10
  Length2 = 100
  Placement = pos=(0,0,0) rot=(0.57735,0.57735,0.57735;2.0944rad)
  Profile = -> Sketch041
  Refine = true
  Type = 0
FEATURE [Sketcher::SketchObject] Sketch015
  ExternalGeometry = -> [Pad013]
  MapMode = 5
  Placement = pos=(10,0,0) rot=(0.57735,0.57735,0.57735;2.0944rad)
  Support = -> [Pad013]
  sketch-geometry (8):
    g0: LineSegment StartX=-6.5 StartY=4 StartZ=0 EndX=6.5 EndY=4 EndZ=0
    g1: LineSegment StartX=6.5 StartY=4 StartZ=0 EndX=6.5 EndY=1 EndZ=0
    g2: LineSegment StartX=6.5 StartY=1 StartZ=0 EndX=-6.5 EndY=1 EndZ=0
    g3: LineSegment StartX=-6.5 StartY=1 StartZ=0 EndX=-6.5 EndY=4 EndZ=0
    g4: LineSegment [constr] StartX=-6.5 StartY=1 StartZ=0 EndX=-7.5 EndY=1 EndZ=0
    g5: LineSegment [constr] StartX=-6.5 StartY=1 StartZ=0 EndX=-6.5 EndY=0 EndZ=0
    g6: LineSegment [constr] StartX=6.5 StartY=4 StartZ=0 EndX=6.5 EndY=5 EndZ=0
    g7: LineSegment [constr] StartX=6.5 StartY=4 StartZ=0 EndX=7.5 EndY=4 EndZ=0
  constraints (23):
    c: Coincident(g0,g1)
    c: Coincident(g1,g2)
    c: Coincident(g2,g3)
    c: Coincident(g3,g0)
    c: Horizontal(g2)
    c: Vertical(g1)
    c: Vertical(g3)
    c: Symmetric(g0,g0,g-2)
    c: Coincident(g4,g2)
    c: PointOnObject(g4,g-4)
    c: Horizontal(g4)
    c: PointOnObject(g5,g-1)
    c: Vertical(g5)
    c: Coincident(g6,g0)
    c: Coincident(g7,g0)
    c: Horizontal(g7)
    c: Vertical(g6)
    c: PointOnObject(g6,g-5)
    c: Equal(g7,g6)
    c: Equal(g6,g4)
    c: Equal(g4,g5)
    c: DistanceX(g4,g4) = 1
    c: Coincident(g5,g2)
FEATURE [PartDesign::Pocket] Pocket007
  BaseFeature = -> Pad013
  Length = 6
  Length2 = 100
  Placement = pos=(0,0,0) rot=(0.57735,0.57735,0.57735;2.0944rad)
  Profile = -> Sketch015
  Refine = true
  Type = 0
FEATURE [Sketcher::SketchObject] Sketch016
  ExternalGeometry = -> [Pocket007]
  MapMode = 5
  Placement = pos=(10,0,0) rot=(0.57735,0.57735,0.57735;2.0944rad)
  Support = -> [Pocket007]
  sketch-geometry (4):
    g0: LineSegment StartX=-4 StartY=5 StartZ=0 EndX=4 EndY=5 EndZ=0
    g1: LineSegment StartX=4 StartY=5 StartZ=0 EndX=4 EndY=4 EndZ=0
    g2: LineSegment StartX=4 StartY=4 StartZ=0 EndX=-4 EndY=4 EndZ=0
    g3: LineSegment StartX=-4 StartY=4 StartZ=0 EndX=-4 EndY=5 EndZ=0
  constraints (11):
    c: Coincident(g0,g1)
    c: Coincident(g1,g2)
    c: Coincident(g2,g3)
    c: Coincident(g3,g0)
    c: Horizontal(g0)
    c: Vertical(g1)
    c: Vertical(g3)
    c: PointOnObject(g0,g-3)
    c: PointOnObject(g1,g-4)
    c: Symmetric(g1,g2,g-2)
    c: DistanceX(g0,g0) = 8
FEATURE [PartDesign::Pocket] Pocket008
  BaseFeature = -> Pocket007
  Length = 4.5
  Length2 = 100
  Placement = pos=(0,0,0) rot=(0.57735,0.57735,0.57735;2.0944rad)
  Profile = -> Sketch016
  Refine = true
  Type = 0
FEATURE [Sketcher::SketchObject] Sketch033
  ExternalGeometry = -> [Pocket008]
  MapMode = 5
  Placement = pos=(0,0,5) rot=(0,0,-1;1.5708rad)
  Support = -> [Pocket008]
  sketch-geometry (11):
    g0: LineSegment StartX=-6.49 StartY=8.99 StartZ=0 EndX=-5.01 EndY=8.99 EndZ=0
    g1: LineSegment StartX=-5.01 StartY=8.99 StartZ=0 EndX=-5.01 EndY=4.5 EndZ=0
    g2: LineSegment StartX=-5.01 StartY=4.5 StartZ=0 EndX=-6.49 EndY=4.5 EndZ=0
    g3: LineSegment StartX=-6.49 StartY=4.5 StartZ=0 EndX=-6.49 EndY=8.99 EndZ=0
    g4: LineSegment StartX=5.01 StartY=8.99 StartZ=0 EndX=6.49 EndY=8.99 EndZ=0
    g5: LineSegment StartX=6.49 StartY=8.99 StartZ=0 EndX=6.49 EndY=4.5 EndZ=0
    g6: LineSegment StartX=6.49 StartY=4.5 StartZ=0 EndX=5.01 EndY=4.5 EndZ=0
    g7: LineSegment StartX=5.01 StartY=4.5 StartZ=0 EndX=5.01 EndY=8.99 EndZ=0
    g8: LineSegment [constr] StartX=-7.5 StartY=8.99 StartZ=0 EndX=-6.49 EndY=8.99 EndZ=0
    g9: LineSegment [constr] StartX=-6.49 StartY=10 StartZ=0 EndX=-6.49 EndY=8.99 EndZ=0
    g10: LineSegment [constr] StartX=-5.01 StartY=8.99 StartZ=0 EndX=-4 EndY=8.99 EndZ=0
  constraints (32):
    c: Coincident(g0,g1)
    c: Coincident(g1,g2)
    c: Coincident(g2,g3)
    c: Coincident(g3,g0)
    c: Horizontal(g0)
    c: Horizontal(g2)
    c: Vertical(g1)
    c: Vertical(g3)
    c: Coincident(g4,g5)
    c: Coincident(g5,g6)
    c: Coincident(g6,g7)
    c: Coincident(g7,g4)
    c: Horizontal(g4)
    c: Horizontal(g6)
    c: Vertical(g5)
    c: Vertical(g7)
    c: DistanceX(g4,g4) = 1.48
    c: Equal(g0,g4)
    c: Equal(g7,g1)
    c: PointOnObject(g8,g-4)
    c: Coincident(g8,g0)
    c: Horizontal(g8)
    c: PointOnObject(g9,g-5)
    c: Coincident(g9,g0)
    c: Vertical(g9)
    c: Coincident(g10,g0)
    c: PointOnObject(g10,g-3)
    c: Horizontal(g10)
    c: Symmetric(g4,g0,g-2)
    c: Equal(g10,g9)
    c: Equal(g9,g8)
    c: DistanceY(g3,g3) = 4.49
FEATURE [PartDesign::Pad] Pad015
  Length = 1
  Length2 = 100
  Placement = pos=(0,0,0) rot=(0.57735,0.57735,0.57735;2.0944rad)
  Profile = -> Sketch035
  Refine = true
  Type = 0
FEATURE [Sketcher::SketchObject] Sketch034
  ExternalGeometry = -> [Pad015]
  MapMode = 5
  Placement = pos=(0,0,1) rot=(0,0,-1;1.5708rad)
  Support = -> [Pad015]
  sketch-geometry (7):
    g0: LineSegment StartX=-5.5 StartY=1 StartZ=0 EndX=-4.5 EndY=1 EndZ=0
    g1: LineSegment StartX=-4.5 StartY=1 StartZ=0 EndX=-4.5 EndY=8 EndZ=0
    g2: LineSegment [constr] StartX=-4.5 StartY=8 StartZ=0 EndX=-5.5 EndY=8 EndZ=0
    g3: LineSegment StartX=-5.5 StartY=8 StartZ=0 EndX=-5.5 EndY=1 EndZ=0
    g4: LineSegment StartX=-5.5 StartY=8 StartZ=0 EndX=-5.25 EndY=8.7 EndZ=0
    g5: LineSegment StartX=-5.25 StartY=8.7 StartZ=0 EndX=-4.75 EndY=8.7 EndZ=0
    g6: LineSegment StartX=-4.75 StartY=8.7 StartZ=0 EndX=-4.5 EndY=8 EndZ=0
  constraints (19):
    c: Coincident(g0,g1)
    c: Coincident(g1,g2)
    c: Coincident(g2,g3)
    c: Coincident(g3,g0)
    c: Horizontal(g0)
    c: Horizontal(g2)
    c: Vertical(g1)
    c: Vertical(g3)
    c: Coincident(g0,g-3)
    c: Coincident(g2,g4)
    c: Coincident(g4,g5)
    c: Horizontal(g5)
    c: Coincident(g5,g6)
    c: Coincident(g6,g1)
    c: DistanceY(g1,g5) = 0.7
    c: DistanceX(g5,g5) = 0.5
    c: Equal(g6,g4)
    c: DistanceX(g0,g0) = 1
    c: DistanceY(g3,g3) = 7
FEATURE [PartDesign::Pocket] Pocket010
  BaseFeature = -> Pocket004
  Length = 5
  Length2 = 100
  Profile = -> Sketch036
  Refine = true
  Type = 0
FEATURE [PartDesign::Body] Body002  label="Aluminum front001"
  Group = -> [Sketch025,Pad003,Chamfer007,Fillet006,Sketch038,Pocket002,Sketch028,Pocket003,Sketch029,Pad014,Draft,Sketch039,Pocket004,Sketch036,Pocket010]
  Origin = -> Origin003
  Placement = pos=(0,0,32.35) rot=(0,0,1;0rad)
  Tip = -> Pocket010
FEATURE [App::Part] Part003  label="Aluminum front"
  Group = -> [Body002]
  Origin = -> Origin007
FEATURE [PartDesign::Pad] Pad016
  BaseFeature = -> Pad015
  Length = 1
  Length2 = 100
  Placement = pos=(0,0,0) rot=(0.57735,0.57735,0.57735;2.0944rad)
  Profile = -> Sketch034
  Refine = true
  Reversed = true
  Type = 0
FEATURE [PartDesign::LinearPattern] LinearPattern
  BaseFeature = -> Pad016
  Direction = -> Pad016 [Edge10]
  Length = 10
  Occurrences = 6
  Originals = -> [Pad016]
  Placement = pos=(0,0,0) rot=(0.57735,0.57735,0.57735;2.0944rad)
  Refine = true
  Reversed = true
FEATURE [PartDesign::Body] Body006  label="pin"
  Group = -> [Sketch035,Pad015,Sketch034,Pad016,LinearPattern]
  Origin = -> Origin013
  Placement = pos=(0,0,2) rot=(0,0,1;0rad)
  Tip = -> LinearPattern
FEATURE [PartDesign::Pocket] Pocket009
  BaseFeature = -> Pocket008
  Length = 2
  Length2 = 100
  Placement = pos=(0,0,0) rot=(0.57735,0.57735,0.57735;2.0944rad)
  Profile = -> Sketch033
  Refine = true
  Type = 0
FEATURE [PartDesign::Body] Body005  label="conector"
  Group = -> [Sketch041,Pad013,Sketch015,Pocket007,Sketch016,Pocket008,Sketch033,Pocket009]
  Origin = -> Origin012
  Tip = -> Pocket009
FEATURE [App::Part] Part006  label="Conector"
  Group = -> [Body005,Body006]
  Origin = -> Origin011
  Placement = pos=(17,0,4) rot=(0,0,1;0rad)
FEATURE [App::Part] Part  label="Nema 17"
  Group = -> [Part001,Part002,Part003,Part004,Part005,Part006]
  Origin = -> Origin
  Placement = pos=(43,588,590) rot=(0,0,1;0rad)
FEATURE [Sketcher::SketchObject] Sketch042
  MapMode = 5
  Support = -> [XY_Plane022]
  sketch-geometry (4):
    g0: LineSegment StartX=-21.15 StartY=21.15 StartZ=0 EndX=21.15 EndY=21.15 EndZ=0
    g1: LineSegment StartX=21.15 StartY=21.15 StartZ=0 EndX=21.15 EndY=-21.15 EndZ=0
    g2: LineSegment StartX=21.15 StartY=-21.15 StartZ=0 EndX=-21.15 EndY=-21.15 EndZ=0
    g3: LineSegment StartX=-21.15 StartY=-21.15 StartZ=0 EndX=-21.15 EndY=21.15 EndZ=0
  constraints (11):
    c: Coincident(g0,g1)
    c: Coincident(g1,g2)
    c: Coincident(g2,g3)
    c: Coincident(g3,g0)
    c: Horizontal(g0)
    c: Horizontal(g2)
    c: Vertical(g1)
    c: Vertical(g3)
    c: Symmetric(g0,g1,g-1)
    c: DistanceX(g0,g0) = 42.3
    c: Equal(g0,g3)
FEATURE [Sketcher::SketchObject] Sketch043
  MapMode = 5
  Support = -> [XY_Plane020]
  sketch-geometry (4):
    g0: LineSegment StartX=-21 StartY=21 StartZ=0 EndX=21 EndY=21 EndZ=0
    g1: LineSegment StartX=21 StartY=21 StartZ=0 EndX=21 EndY=-21 EndZ=0
    g2: LineSegment StartX=21 StartY=-21 StartZ=0 EndX=-21 EndY=-21 EndZ=0
    g3: LineSegment StartX=-21 StartY=-21 StartZ=0 EndX=-21 EndY=21 EndZ=0
  constraints (11):
    c: Coincident(g0,g1)
    c: Coincident(g1,g2)
    c: Coincident(g2,g3)
    c: Coincident(g3,g0)
    c: Horizontal(g0)
    c: Horizontal(g2)
    c: Vertical(g1)
    c: Vertical(g3)
    c: DistanceX(g0,g0) = 42
    c: Symmetric(g0,g1,g-1)
    c: Equal(g0,g3)
FEATURE [Sketcher::SketchObject] Sketch045
  MapMode = 5
  Support = -> [XY_Plane025]
  sketch-geometry (4):
    g0: LineSegment StartX=-21.15 StartY=21.15 StartZ=0 EndX=21.15 EndY=21.15 EndZ=0
    g1: LineSegment StartX=21.15 StartY=21.15 StartZ=0 EndX=21.15 EndY=-21.15 EndZ=0
    g2: LineSegment StartX=21.15 StartY=-21.15 StartZ=0 EndX=-21.15 EndY=-21.15 EndZ=0
    g3: LineSegment StartX=-21.15 StartY=-21.15 StartZ=0 EndX=-21.15 EndY=21.15 EndZ=0
  constraints (11):
    c: Coincident(g0,g1)
    c: Coincident(g1,g2)
    c: Coincident(g2,g3)
    c: Coincident(g3,g0)
    c: Horizontal(g0)
    c: Horizontal(g2)
    c: Vertical(g1)
    c: Vertical(g3)
    c: Symmetric(g0,g1,g-1)
    c: DistanceX(g0,g0) = 42.3
    c: Equal(g0,g3)
FEATURE [PartDesign::Pad] Pad018
  Length = 22.75
  Length2 = 100
  Profile = -> Sketch043
  Refine = true
  Type = 0
FEATURE [PartDesign::Chamfer] Chamfer012
  Base = -> Pad018 [Edge8,Edge1,Edge5,Edge2]
  BaseFeature = -> Pad018
  Size = 7.5
FEATURE [PartDesign::Pad] Pad019
  Length = 7.75
  Length2 = 100
  Profile = -> Sketch045
  Refine = true
  Type = 0
FEATURE [PartDesign::Chamfer] Chamfer010
  Base = -> Pad019 [Edge8,Edge5,Edge2,Edge1]
  BaseFeature = -> Pad019
  Size = 5
FEATURE [PartDesign::Fillet] Fillet007
  Base = -> Chamfer010 [Edge22,Edge24,Edge23,Edge21,Edge12,Edge2,Edge3,Edge14]
  BaseFeature = -> Chamfer010
  Radius = 2
FEATURE [PartDesign::Pad] Pad020
  Length = 9.6
  Length2 = 100
  Profile = -> Sketch042
  Refine = true
  Type = 0
FEATURE [Sketcher::SketchObject] Sketch044
  ExternalGeometry = -> [Pad020]
  MapMode = 5
  Support = -> [XY_Plane022]
  sketch-geometry (4):
    g0: LineSegment StartX=21.15 StartY=8.2 StartZ=0 EndX=25.45 EndY=8.2 EndZ=0
    g1: LineSegment StartX=25.45 StartY=8.2 StartZ=0 EndX=25.45 EndY=-8.2 EndZ=0
    g2: LineSegment StartX=25.45 StartY=-8.2 StartZ=0 EndX=21.15 EndY=-8.2 EndZ=0
    g3: LineSegment StartX=21.15 StartY=-8.2 StartZ=0 EndX=21.15 EndY=8.2 EndZ=0
  constraints (11):
    c: Coincident(g0,g1)
    c: Coincident(g1,g2)
    c: Coincident(g2,g3)
    c: Coincident(g3,g0)
    c: Horizontal(g0)
    c: Horizontal(g2)
    c: Vertical(g3)
    c: PointOnObject(g0,g-3)
    c: Symmetric(g1,g0,g-1)
    c: DistanceX(g0,g0) = 4.3
    c: DistanceY(g1,g1) = 16.4
FEATURE [PartDesign::Pad] Pad017
  BaseFeature = -> Pad020
  Length = 3.6
  Length2 = 100
  Profile = -> Sketch044
  Refine = true
  Type = 0
FEATURE [PartDesign::Chamfer] Chamfer011
  Base = -> Pad017 [Edge13,Edge5,Edge1,Edge2]
  BaseFeature = -> Pad017
  Size = 5
FEATURE [PartDesign::Fillet] Fillet008
  Base = -> Chamfer011 [Edge33,Edge28,Edge18,Edge3,Edge2,Edge16,Edge30,Edge25]
  BaseFeature = -> Chamfer011
  Radius = 2
FEATURE [Sketcher::SketchObject] Sketch047
  MapMode = 5
  Placement = pos=(0,0,0) rot=(1,0,0;3.14159rad)
  Support = -> [Chamfer012]
  sketch-geometry (8):
    g0: LineSegment [constr] StartX=-15.5 StartY=15.5 StartZ=0 EndX=15.5 EndY=15.5 EndZ=0
    g1: LineSegment [constr] StartX=15.5 StartY=15.5 StartZ=0 EndX=15.5 EndY=-15.5 EndZ=0
    g2: LineSegment [constr] StartX=15.5 StartY=-15.5 StartZ=0 EndX=-15.5 EndY=-15.5 EndZ=0
    g3: LineSegment [constr] StartX=-15.5 StartY=-15.5 StartZ=0 EndX=-15.5 EndY=15.5 EndZ=0
    g4: Circle CenterX=-15.5 CenterY=15.5 CenterZ=0 NormalX=0 NormalY=0 NormalZ=1 AngleXU=0 Radius=1.22
    g5: Circle CenterX=15.5 CenterY=15.5 CenterZ=0 NormalX=0 NormalY=0 NormalZ=1 AngleXU=0 Radius=1.22
    g6: Circle CenterX=15.5 CenterY=-15.5 CenterZ=0 NormalX=0 NormalY=0 NormalZ=1 AngleXU=0 Radius=1.22
    g7: Circle CenterX=-15.5 CenterY=-15.5 CenterZ=0 NormalX=0 NormalY=0 NormalZ=1 AngleXU=0 Radius=1.22
  constraints (19):
    c: Coincident(g0,g1)
    c: Coincident(g1,g2)
    c: Coincident(g2,g3)
    c: Coincident(g3,g0)
    c: Horizontal(g0)
    c: Horizontal(g2)
    c: Vertical(g1)
    c: Vertical(g3)
    c: Equal(g0,g3)
    c: Symmetric(g0,g1,g-1)
    c: DistanceX(g0,g0) = 31
    c: Coincident(g4,g0)
    c: Coincident(g5,g0)
    c: Coincident(g6,g1)
    c: Coincident(g7,g2)
    c: Equal(g6,g5)
    c: Equal(g5,g4)
    c: Equal(g4,g7)
    c: Radius(g4) = 1.22
FEATURE [PartDesign::Pocket] Pocket011
  BaseFeature = -> Chamfer012
  Length = 5
  Length2 = 100
  Profile = -> Sketch047
  Refine = true
  Type = 1
FEATURE [Sketcher::SketchObject] Sketch050
  MapMode = 5
  Placement = pos=(0,0,0) rot=(1,0,0;3.14159rad)
  Support = -> [Fillet008]
  sketch-geometry (8):
    g0: LineSegment [constr] StartX=-15.5 StartY=15.5 StartZ=0 EndX=15.5 EndY=15.5 EndZ=0
    g1: LineSegment [constr] StartX=15.5 StartY=15.5 StartZ=0 EndX=15.5 EndY=-15.5 EndZ=0
    g2: LineSegment [constr] StartX=15.5 StartY=-15.5 StartZ=0 EndX=-15.5 EndY=-15.5 EndZ=0
    g3: LineSegment [constr] StartX=-15.5 StartY=-15.5 StartZ=0 EndX=-15.5 EndY=15.5 EndZ=0
    g4: Circle CenterX=-15.5 CenterY=15.5 CenterZ=0 NormalX=0 NormalY=0 NormalZ=1 AngleXU=0 Radius=1.225
    g5: Circle CenterX=15.5 CenterY=15.5 CenterZ=0 NormalX=0 NormalY=0 NormalZ=1 AngleXU=0 Radius=1.225
    g6: Circle CenterX=15.5 CenterY=-15.5 CenterZ=0 NormalX=0 NormalY=0 NormalZ=1 AngleXU=0 Radius=1.225
    g7: Circle CenterX=-15.5 CenterY=-15.5 CenterZ=0 NormalX=0 NormalY=0 NormalZ=1 AngleXU=0 Radius=1.225
  constraints (19):
    c: Coincident(g0,g1)
    c: Coincident(g1,g2)
    c: Coincident(g2,g3)
    c: Coincident(g3,g0)
    c: Horizontal(g0)
    c: Horizontal(g2)
    c: Vertical(g1)
    c: Vertical(g3)
    c: Symmetric(g0,g1,g-1)
    c: DistanceX(g0,g0) = 31
    c: Equal(g3,g0)
    c: Coincident(g4,g0)
    c: Coincident(g5,g0)
    c: Coincident(g6,g1)
    c: Coincident(g7,g2)
    c: Equal(g6,g5)
    c: Equal(g5,g4)
    c: Equal(g4,g7)
    c: Radius(g4) = 1.225
FEATURE [PartDesign::Hole] Hole001
  BaseFeature = -> Fillet008
  Depth = 25
  DepthType = 0
  Diameter = 3
  DrillPoint = 1
  DrillPointAngle = 118
  HoleCutCountersinkAngle = 90
  HoleCutDepth = 5
  HoleCutDiameter = 5
  HoleCutType = 1
  ModelActualThread = false
  Profile = -> Sketch050
  Refine = true
  Tapered = false
  TaperedAngle = 90
  ThreadAngle = 0
  ThreadClass = 0
  ThreadCutOffInner = 0
  ThreadCutOffOuter = 0
  ThreadDirection = 0
  ThreadFit = 0
  ThreadPitch = 0
  ThreadSize = 0
  ThreadType = 0
  Threaded = false
FEATURE [Sketcher::SketchObject] Sketch051
  MapMode = 5
  Support = -> [XY_Plane023]
  sketch-geometry (1):
    g0: Circle CenterX=0 CenterY=0 CenterZ=0 NormalX=0 NormalY=0 NormalZ=1 AngleXU=0 Radius=2.5
  constraints (2):
    c: Coincident(g0,g-1)
    c: Radius(g0) = 2.5
FEATURE [PartDesign::Pad] Pad022
  Length = 60
  Length2 = 100
  Profile = -> Sketch051
  Refine = true
  Type = 0
FEATURE [Sketcher::SketchObject] Sketch046
  MapMode = 5
  Placement = pos=(0,0,60) rot=(0,0,1;0rad)
  Support = -> [Pad022]
  sketch-geometry (4):
    g0: LineSegment StartX=2 StartY=2 StartZ=0 EndX=6 EndY=2 EndZ=0
    g1: LineSegment StartX=6 StartY=2 StartZ=0 EndX=6 EndY=-2 EndZ=0
    g2: LineSegment StartX=6 StartY=-2 StartZ=0 EndX=2 EndY=-2 EndZ=0
    g3: LineSegment StartX=2 StartY=-2 StartZ=0 EndX=2 EndY=2 EndZ=0
  constraints (11):
    c: Coincident(g0,g1)
    c: Coincident(g1,g2)
    c: Coincident(g2,g3)
    c: Coincident(g3,g0)
    c: Horizontal(g0)
    c: Horizontal(g2)
    c: Vertical(g1)
    c: Symmetric(g2,g0,g-1)
    c: DistanceX(g-1,g0) = 2
    c: Equal(g0,g3)
    c: DistanceX(g0,g0) = 4
FEATURE [PartDesign::Pocket] Pocket013
  BaseFeature = -> Pad022
  Length = 16
  Length2 = 100
  Profile = -> Sketch046
  Refine = true
  Type = 0
FEATURE [PartDesign::Chamfer] Chamfer009
  Base = -> Pocket013 [Edge3,Edge5,Edge9]
  BaseFeature = -> Pocket013
  Size = 0.3
FEATURE [Sketcher::SketchObject] Sketch054
  MapMode = 5
  Placement = pos=(0,0,0) rot=(0.57735,0.57735,0.57735;2.0944rad)
  Support = -> [YZ_Plane025]
  sketch-geometry (4):
    g0: LineSegment StartX=-5.5 StartY=1 StartZ=0 EndX=5.5 EndY=1 EndZ=0
    g1: LineSegment StartX=5.5 StartY=1 StartZ=0 EndX=5.5 EndY=0 EndZ=0
    g2: LineSegment StartX=5.5 StartY=0 StartZ=0 EndX=-5.5 EndY=0 EndZ=0
    g3: LineSegment StartX=-5.5 StartY=0 StartZ=0 EndX=-5.5 EndY=1 EndZ=0
  constraints (11):
    c: Coincident(g0,g1)
    c: Coincident(g1,g2)
    c: Coincident(g2,g3)
    c: Coincident(g3,g0)
    c: Horizontal(g0)
    c: Vertical(g1)
    c: Vertical(g3)
    c: PointOnObject(g1,g-1)
    c: DistanceY(g3,g3) = 1
    c: DistanceX(g2,g2) = 11
    c: Symmetric(g1,g2,g-2)
FEATURE [Sketcher::SketchObject] Sketch057
  MapMode = 5
  Placement = pos=(0,0,7.75) rot=(0,0,1;0rad)
  Support = -> [Fillet007]
  sketch-geometry (8):
    g0: LineSegment [constr] StartX=-15.5 StartY=15.5 StartZ=0 EndX=15.5 EndY=15.5 EndZ=0
    g1: LineSegment [constr] StartX=15.5 StartY=15.5 StartZ=0 EndX=15.5 EndY=-15.5 EndZ=0
    g2: LineSegment [constr] StartX=15.5 StartY=-15.5 StartZ=0 EndX=-15.5 EndY=-15.5 EndZ=0
    g3: LineSegment [constr] StartX=-15.5 StartY=-15.5 StartZ=0 EndX=-15.5 EndY=15.5 EndZ=0
    g4: Circle CenterX=-15.5 CenterY=15.5 CenterZ=0 NormalX=0 NormalY=0 NormalZ=1 AngleXU=0 Radius=1.225
    g5: Circle CenterX=15.5 CenterY=15.5 CenterZ=0 NormalX=0 NormalY=0 NormalZ=1 AngleXU=0 Radius=1.225
    g6: Circle CenterX=15.5 CenterY=-15.5 CenterZ=0 NormalX=0 NormalY=0 NormalZ=1 AngleXU=0 Radius=1.225
    g7: Circle CenterX=-15.5 CenterY=-15.5 CenterZ=0 NormalX=0 NormalY=0 NormalZ=1 AngleXU=0 Radius=1.225
  constraints (19):
    c: Coincident(g0,g1)
    c: Coincident(g1,g2)
    c: Coincident(g2,g3)
    c: Coincident(g3,g0)
    c: Horizontal(g0)
    c: Horizontal(g2)
    c: Vertical(g1)
    c: Vertical(g3)
    c: Equal(g0,g3)
    c: Symmetric(g0,g1,g-1)
    c: DistanceX(g0,g0) = 31
    c: Coincident(g4,g0)
    c: Coincident(g7,g2)
    c: Coincident(g0,g5)
    c: Coincident(g1,g6)
    c: Equal(g7,g4)
    c: Equal(g4,g5)
    c: Equal(g5,g6)
    c: Radius(g4) = 1.225
FEATURE [PartDesign::Pocket] Pocket015
  BaseFeature = -> Fillet007
  Length = 5
  Length2 = 100
  Profile = -> Sketch057
  Refine = true
  Type = 1
FEATURE [Sketcher::SketchObject] Sketch048
  MapMode = 5
  Placement = pos=(0,0,7.75) rot=(0,0,1;0rad)
  Support = -> [Pocket015]
  sketch-geometry (1):
    g0: Circle CenterX=0 CenterY=0 CenterZ=0 NormalX=0 NormalY=0 NormalZ=1 AngleXU=0 Radius=14
  constraints (2):
    c: Coincident(g0,g-1)
    c: Radius(g0) = 14
FEATURE [PartDesign::Pocket] Pocket016
  BaseFeature = -> Pocket015
  Length = 1
  Length2 = 100
  Profile = -> Sketch048
  Refine = true
  Type = 0
FEATURE [Sketcher::SketchObject] Sketch049
  MapMode = 5
  Placement = pos=(0,0,6.75) rot=(0,0,1;0rad)
  Support = -> [Pocket016]
  sketch-geometry (1):
    g0: Circle CenterX=0 CenterY=0 CenterZ=0 NormalX=0 NormalY=0 NormalZ=1 AngleXU=0 Radius=11
  constraints (2):
    c: Coincident(g0,g-1)
    c: Radius(g0) = 11
FEATURE [Sketcher::SketchObject] Sketch059
  ExternalGeometry = -> [Hole001]
  MapMode = 5
  Placement = pos=(21.15,0,0) rot=(0.57735,0.57735,0.57735;2.0944rad)
  Support = -> [Hole001]
  sketch-geometry (4):
    g0: LineSegment StartX=-8.2 StartY=3.6 StartZ=0 EndX=8.2 EndY=3.6 EndZ=0
    g1: LineSegment StartX=8.2 StartY=3.6 StartZ=0 EndX=8.2 EndY=9.6 EndZ=0
    g2: LineSegment StartX=8.2 StartY=9.6 StartZ=0 EndX=-8.2 EndY=9.6 EndZ=0
    g3: LineSegment StartX=-8.2 StartY=9.6 StartZ=0 EndX=-8.2 EndY=3.6 EndZ=0
  constraints (10):
    c: Coincident(g0,g1)
    c: Coincident(g1,g2)
    c: Coincident(g2,g3)
    c: Coincident(g3,g0)
    c: Horizontal(g0)
    c: Vertical(g1)
    c: Vertical(g3)
    c: Coincident(g0,g-3)
    c: PointOnObject(g1,g-5)
    c: Symmetric(g2,g1,g-2)
FEATURE [Sketcher::SketchObject] Sketch060
  MapMode = 5
  Placement = pos=(0,0,22.75) rot=(0,0,1;0rad)
  Support = -> [Pocket011]
  sketch-geometry (1):
    g0: Circle CenterX=0 CenterY=0 CenterZ=0 NormalX=0 NormalY=0 NormalZ=1 AngleXU=0 Radius=18
  constraints (2):
    c: Coincident(g0,g-1)
    c: Radius(g0) = 18
FEATURE [Sketcher::SketchObject] Sketch062
  MapMode = 5
  Placement = pos=(0,0,0) rot=(0.57735,0.57735,0.57735;2.0944rad)
  Support = -> [YZ_Plane026]
  sketch-geometry (4):
    g0: LineSegment StartX=-7.5 StartY=0 StartZ=0 EndX=7.5 EndY=0 EndZ=0
    g1: LineSegment StartX=7.5 StartY=0 StartZ=0 EndX=7.5 EndY=5 EndZ=0
    g2: LineSegment StartX=7.5 StartY=5 StartZ=0 EndX=-7.5 EndY=5 EndZ=0
    g3: LineSegment StartX=-7.5 StartY=5 StartZ=0 EndX=-7.5 EndY=0 EndZ=0
  constraints (11):
    c: Coincident(g0,g1)
    c: Coincident(g1,g2)
    c: Coincident(g2,g3)
    c: Coincident(g3,g0)
    c: Horizontal(g0)
    c: Horizontal(g2)
    c: Vertical(g1)
    c: Vertical(g3)
    c: Symmetric(g0,g0,g-1)
    c: DistanceX(g0,g0) = 15
    c: DistanceY(g3,g3) = 5
FEATURE [PartDesign::Pad] Pad021
  Length = 10
  Length2 = 100
  Placement = pos=(0,0,0) rot=(0.57735,0.57735,0.57735;2.0944rad)
  Profile = -> Sketch062
  Refine = true
  Type = 0
FEATURE [Sketcher::SketchObject] Sketch055
  ExternalGeometry = -> [Pad021]
  MapMode = 5
  Placement = pos=(10,0,0) rot=(0.57735,0.57735,0.57735;2.0944rad)
  Support = -> [Pad021]
  sketch-geometry (8):
    g0: LineSegment StartX=-6.5 StartY=4 StartZ=0 EndX=6.5 EndY=4 EndZ=0
    g1: LineSegment StartX=6.5 StartY=4 StartZ=0 EndX=6.5 EndY=1 EndZ=0
    g2: LineSegment StartX=6.5 StartY=1 StartZ=0 EndX=-6.5 EndY=1 EndZ=0
    g3: LineSegment StartX=-6.5 StartY=1 StartZ=0 EndX=-6.5 EndY=4 EndZ=0
    g4: LineSegment [constr] StartX=-6.5 StartY=1 StartZ=0 EndX=-7.5 EndY=1 EndZ=0
    g5: LineSegment [constr] StartX=-6.5 StartY=1 StartZ=0 EndX=-6.5 EndY=0 EndZ=0
    g6: LineSegment [constr] StartX=6.5 StartY=4 StartZ=0 EndX=6.5 EndY=5 EndZ=0
    g7: LineSegment [constr] StartX=6.5 StartY=4 StartZ=0 EndX=7.5 EndY=4 EndZ=0
  constraints (23):
    c: Coincident(g0,g1)
    c: Coincident(g1,g2)
    c: Coincident(g2,g3)
    c: Coincident(g3,g0)
    c: Horizontal(g2)
    c: Vertical(g1)
    c: Vertical(g3)
    c: Symmetric(g0,g0,g-2)
    c: Coincident(g4,g2)
    c: PointOnObject(g4,g-4)
    c: Horizontal(g4)
    c: PointOnObject(g5,g-1)
    c: Vertical(g5)
    c: Coincident(g6,g0)
    c: Coincident(g7,g0)
    c: Horizontal(g7)
    c: Vertical(g6)
    c: PointOnObject(g6,g-5)
    c: Equal(g7,g6)
    c: Equal(g6,g4)
    c: Equal(g4,g5)
    c: DistanceX(g4,g4) = 1
    c: Coincident(g5,g2)
FEATURE [PartDesign::Pocket] Pocket012
  BaseFeature = -> Pad021
  Length = 6
  Length2 = 100
  Placement = pos=(0,0,0) rot=(0.57735,0.57735,0.57735;2.0944rad)
  Profile = -> Sketch055
  Refine = true
  Type = 0
FEATURE [Sketcher::SketchObject] Sketch056
  ExternalGeometry = -> [Pocket012]
  MapMode = 5
  Placement = pos=(10,0,0) rot=(0.57735,0.57735,0.57735;2.0944rad)
  Support = -> [Pocket012]
  sketch-geometry (4):
    g0: LineSegment StartX=-4 StartY=5 StartZ=0 EndX=4 EndY=5 EndZ=0
    g1: LineSegment StartX=4 StartY=5 StartZ=0 EndX=4 EndY=4 EndZ=0
    g2: LineSegment StartX=4 StartY=4 StartZ=0 EndX=-4 EndY=4 EndZ=0
    g3: LineSegment StartX=-4 StartY=4 StartZ=0 EndX=-4 EndY=5 EndZ=0
  constraints (11):
    c: Coincident(g0,g1)
    c: Coincident(g1,g2)
    c: Coincident(g2,g3)
    c: Coincident(g3,g0)
    c: Horizontal(g0)
    c: Vertical(g1)
    c: Vertical(g3)
    c: PointOnObject(g0,g-3)
    c: PointOnObject(g1,g-4)
    c: Symmetric(g1,g2,g-2)
    c: DistanceX(g0,g0) = 8
FEATURE [PartDesign::Body] Body010  label="Stator001"
  Origin = -> Origin026
FEATURE [PartDesign::Body] Body011  label="Rotor003"
  Group = -> [Sketch051,Pad022,Sketch046,Pocket013,Chamfer009]
  Origin = -> Origin015
  Placement = pos=(0,0,2) rot=(0,0,1;0rad)
  Tip = -> Chamfer009
FEATURE [App::Part] Part008  label="Rotor002"
  Group = -> [Body011]
  Origin = -> Origin023
FEATURE [PartDesign::Pad] Pad023
  Length = 1
  Length2 = 100
  Placement = pos=(0,0,0) rot=(0.57735,0.57735,0.57735;2.0944rad)
  Profile = -> Sketch054
  Refine = true
  Type = 0
FEATURE [Sketcher::SketchObject] Sketch053
  ExternalGeometry = -> [Pad023]
  MapMode = 5
  Placement = pos=(0,0,1) rot=(0,0,-1;1.5708rad)
  Support = -> [Pad023]
  sketch-geometry (7):
    g0: LineSegment StartX=-5.5 StartY=1 StartZ=0 EndX=-4.5 EndY=1 EndZ=0
    g1: LineSegment StartX=-4.5 StartY=1 StartZ=0 EndX=-4.5 EndY=8 EndZ=0
    g2: LineSegment [constr] StartX=-4.5 StartY=8 StartZ=0 EndX=-5.5 EndY=8 EndZ=0
    g3: LineSegment StartX=-5.5 StartY=8 StartZ=0 EndX=-5.5 EndY=1 EndZ=0
    g4: LineSegment StartX=-5.5 StartY=8 StartZ=0 EndX=-5.25 EndY=8.7 EndZ=0
    g5: LineSegment StartX=-5.25 StartY=8.7 StartZ=0 EndX=-4.75 EndY=8.7 EndZ=0
    g6: LineSegment StartX=-4.75 StartY=8.7 StartZ=0 EndX=-4.5 EndY=8 EndZ=0
  constraints (19):
    c: Coincident(g0,g1)
    c: Coincident(g1,g2)
    c: Coincident(g2,g3)
    c: Coincident(g3,g0)
    c: Horizontal(g0)
    c: Horizontal(g2)
    c: Vertical(g1)
    c: Vertical(g3)
    c: Coincident(g0,g-3)
    c: Coincident(g2,g4)
    c: Coincident(g4,g5)
    c: Horizontal(g5)
    c: Coincident(g5,g6)
    c: Coincident(g6,g1)
    c: DistanceY(g1,g5) = 0.7
    c: DistanceX(g5,g5) = 0.5
    c: Equal(g6,g4)
    c: DistanceX(g0,g0) = 1
    c: DistanceY(g3,g3) = 7
FEATURE [PartDesign::Pad] Pad024
  BaseFeature = -> Pocket016
  Length = 3
  Length2 = 100
  Profile = -> Sketch049
  Refine = true
  Type = 0
FEATURE [PartDesign::Draft] Draft001
  Angle = 10
  Base = -> Pad024 [Face25]
  BaseFeature = -> Pad024
  NeutralPlane = -> Pad024 [Face24]
FEATURE [Sketcher::SketchObject] Sketch061
  MapMode = 5
  Placement = pos=(0,0,9.75) rot=(0,0,1;0rad)
  Support = -> [Draft001]
  sketch-geometry (1):
    g0: Circle CenterX=0 CenterY=0 CenterZ=0 NormalX=0 NormalY=0 NormalZ=1 AngleXU=0 Radius=5
  constraints (2):
    c: Coincident(g0,g-1)
    c: Radius(g0) = 5
FEATURE [PartDesign::Pocket] Pocket014
  BaseFeature = -> Draft001
  Length = 8
  Length2 = 100
  Profile = -> Sketch061
  Refine = true
  Type = 1
FEATURE [Sketcher::SketchObject] Sketch058
  MapMode = 5
  Placement = pos=(0,0,0) rot=(1,0,0;3.14159rad)
  Support = -> [Pocket014]
  sketch-geometry (1):
    g0: Circle CenterX=0 CenterY=0 CenterZ=0 NormalX=0 NormalY=0 NormalZ=1 AngleXU=0 Radius=15.35
  constraints (2):
    c: Coincident(g0,g-1)
    c: Radius(g0) = 15.35
FEATURE [PartDesign::Pocket] Pocket017
  BaseFeature = -> Hole001
  Length = 4
  Length2 = 100
  Profile = -> Sketch059
  Refine = true
  Type = 0
FEATURE [PartDesign::Body] Body009  label="Aluminium rear003"
  Group = -> [Sketch042,Pad020,Sketch044,Pad017,Chamfer011,Fillet008,Sketch050,Hole001,Sketch059,Pocket017]
  Origin = -> Origin017
  Tip = -> Pocket017
FEATURE [App::Part] Part007  label="Aluminium rear002"
  Group = -> [Body009]
  Origin = -> Origin022
FEATURE [PartDesign::Pocket] Pocket018
  BaseFeature = -> Pocket011
  Length = 5
  Length2 = 100
  Profile = -> Sketch060
  Refine = true
  Type = 1
FEATURE [PartDesign::Body] Body012
  Group = -> [Sketch043,Pad018,Chamfer012,Sketch047,Pocket011,Sketch060,Pocket018]
  Origin = -> Origin016
  Placement = pos=(0,0,9.6) rot=(0,0,1;0rad)
  Tip = -> Pocket018
FEATURE [App::Part] Part012  label="Body009"
  Group = -> [Body012,Body010]
  Origin = -> Origin027
FEATURE [PartDesign::Pocket] Pocket019
  BaseFeature = -> Pocket012
  Length = 4.5
  Length2 = 100
  Placement = pos=(0,0,0) rot=(0.57735,0.57735,0.57735;2.0944rad)
  Profile = -> Sketch056
  Refine = true
  Type = 0
FEATURE [Sketcher::SketchObject] Sketch052
  ExternalGeometry = -> [Pocket019]
  MapMode = 5
  Placement = pos=(0,0,5) rot=(0,0,-1;1.5708rad)
  Support = -> [Pocket019]
  sketch-geometry (11):
    g0: LineSegment StartX=-6.49 StartY=8.99 StartZ=0 EndX=-5.01 EndY=8.99 EndZ=0
    g1: LineSegment StartX=-5.01 StartY=8.99 StartZ=0 EndX=-5.01 EndY=4.5 EndZ=0
    g2: LineSegment StartX=-5.01 StartY=4.5 StartZ=0 EndX=-6.49 EndY=4.5 EndZ=0
    g3: LineSegment StartX=-6.49 StartY=4.5 StartZ=0 EndX=-6.49 EndY=8.99 EndZ=0
    g4: LineSegment StartX=5.01 StartY=8.99 StartZ=0 EndX=6.49 EndY=8.99 EndZ=0
    g5: LineSegment StartX=6.49 StartY=8.99 StartZ=0 EndX=6.49 EndY=4.5 EndZ=0
    g6: LineSegment StartX=6.49 StartY=4.5 StartZ=0 EndX=5.01 EndY=4.5 EndZ=0
    g7: LineSegment StartX=5.01 StartY=4.5 StartZ=0 EndX=5.01 EndY=8.99 EndZ=0
    g8: LineSegment [constr] StartX=-7.5 StartY=8.99 StartZ=0 EndX=-6.49 EndY=8.99 EndZ=0
    g9: LineSegment [constr] StartX=-6.49 StartY=10 StartZ=0 EndX=-6.49 EndY=8.99 EndZ=0
    g10: LineSegment [constr] StartX=-5.01 StartY=8.99 StartZ=0 EndX=-4 EndY=8.99 EndZ=0
  constraints (32):
    c: Coincident(g0,g1)
    c: Coincident(g1,g2)
    c: Coincident(g2,g3)
    c: Coincident(g3,g0)
    c: Horizontal(g0)
    c: Horizontal(g2)
    c: Vertical(g1)
    c: Vertical(g3)
    c: Coincident(g4,g5)
    c: Coincident(g5,g6)
    c: Coincident(g6,g7)
    c: Coincident(g7,g4)
    c: Horizontal(g4)
    c: Horizontal(g6)
    c: Vertical(g5)
    c: Vertical(g7)
    c: DistanceX(g4,g4) = 1.48
    c: Equal(g0,g4)
    c: Equal(g7,g1)
    c: PointOnObject(g8,g-4)
    c: Coincident(g8,g0)
    c: Horizontal(g8)
    c: PointOnObject(g9,g-5)
    c: Coincident(g9,g0)
    c: Vertical(g9)
    c: Coincident(g10,g0)
    c: PointOnObject(g10,g-3)
    c: Horizontal(g10)
    c: Symmetric(g4,g0,g-2)
    c: Equal(g10,g9)
    c: Equal(g9,g8)
    c: DistanceY(g3,g3) = 4.49
FEATURE [PartDesign::Pocket] Pocket020
  BaseFeature = -> Pocket014
  Length = 5
  Length2 = 100
  Profile = -> Sketch058
  Refine = true
  Type = 0
FEATURE [PartDesign::Body] Body008  label="Aluminum front003"
  Group = -> [Sketch045,Pad019,Chamfer010,Fillet007,Sketch057,Pocket015,Sketch048,Pocket016,Sketch049,Pad024,Draft001,Sketch061,Pocket014,Sketch058,Pocket020]
  Origin = -> Origin014
  Placement = pos=(0,0,32.35) rot=(0,0,1;0rad)
  Tip = -> Pocket020
FEATURE [App::Part] Part011  label="Aluminum front002"
  Group = -> [Body008]
  Origin = -> Origin019
FEATURE [PartDesign::Pad] Pad025
  BaseFeature = -> Pad023
  Length = 1
  Length2 = 100
  Placement = pos=(0,0,0) rot=(0.57735,0.57735,0.57735;2.0944rad)
  Profile = -> Sketch053
  Refine = true
  Reversed = true
  Type = 0
FEATURE [PartDesign::LinearPattern] LinearPattern001
  BaseFeature = -> Pad025
  Direction = -> Pad025 [Edge10]
  Length = 10
  Occurrences = 6
  Originals = -> [Pad025]
  Placement = pos=(0,0,0) rot=(0.57735,0.57735,0.57735;2.0944rad)
  Refine = true
  Reversed = true
FEATURE [PartDesign::Pocket] Pocket021
  BaseFeature = -> Pocket019
  Length = 2
  Length2 = 100
  Placement = pos=(0,0,0) rot=(0.57735,0.57735,0.57735;2.0944rad)
  Profile = -> Sketch052
  Refine = true
  Type = 0
FEATURE [PartDesign::Body] Body007  label="conector001"
  Group = -> [Sketch062,Pad021,Sketch055,Pocket012,Sketch056,Pocket019,Sketch052,Pocket021]
  Origin = -> Origin025
  Tip = -> Pocket021
FEATURE [PartDesign::Body] Body013  label="pin001"
  Group = -> [Sketch054,Pad023,Sketch053,Pad025,LinearPattern001]
  Origin = -> Origin021
  Placement = pos=(0,0,2) rot=(0,0,1;0rad)
  Tip = -> LinearPattern001
FEATURE [App::Part] Part009  label="Conector001"
  Group = -> [Body007,Body013]
  Origin = -> Origin024
  Placement = pos=(17,0,4) rot=(0,0,1;0rad)
FEATURE [Part::FeaturePython] Screw004  label="M2.5x25-Screw008"  # Fasteners workbench fastener (typed FeaturePython)
  Placement = pos=(15.5,-15.5,4) rot=(0,1,0;3.14159rad)
  diameter = 3
  invert = true
  length = 10
  matchOuter = true
  offset = 1
  thread = true
  type = 16
FEATURE [Part::FeaturePython] Screw005  label="M2.5x25-Screw009"  # Fasteners workbench fastener (typed FeaturePython)
  Placement = pos=(-15.5,-15.5,4) rot=(0,1,0;3.14159rad)
  diameter = 3
  invert = true
  length = 10
  matchOuter = true
  offset = 1
  thread = true
  type = 16
FEATURE [Part::FeaturePython] Screw006  label="M2.5x25-Screw010"  # Fasteners workbench fastener (typed FeaturePython)
  Placement = pos=(15.5,15.5,4) rot=(0,1,0;3.14159rad)
  diameter = 3
  invert = true
  length = 10
  matchOuter = true
  offset = 1
  thread = true
  type = 16
FEATURE [Part::FeaturePython] Screw007  label="M2.5x25-Screw011"  # Fasteners workbench fastener (typed FeaturePython)
  Placement = pos=(-15.5,15.5,4) rot=(0,1,0;3.14159rad)
  diameter = 3
  invert = true
  length = 10
  matchOuter = true
  offset = 1
  thread = true
  type = 16
FEATURE [App::Part] Part010  label="Screw006"
  Group = -> [Screw006,Screw005,Screw004,Screw007]
  Origin = -> Origin020
FEATURE [App::Part] Part013  label="Nema 017_2"
  Group = -> [Part007,Part012,Part011,Part008,Part010,Part009]
  Origin = -> Origin018
  Placement = pos=(670,588,590) rot=(0,0,1;0rad)
FEATURE [App::DocumentObjectGroup] Group001  label="Eje XY+"
  Group = -> [Fusion045,BooleanFragments001,Fusion020,Fusion046,Fusion047,Part,Part013]
FEATURE [Part::FeaturePython] Screw008  label="M2.5x25-Screw012"  # Fasteners workbench fastener (typed FeaturePython)
  Placement = pos=(-15.5,-15.5,4) rot=(0,1,0;3.14159rad)
  diameter = 3
  invert = true
  length = 10
  matchOuter = true
  offset = 1
  thread = true
  type = 16
FEATURE [Part::FeaturePython] Screw009  label="M2.5x25-Screw013"  # Fasteners workbench fastener (typed FeaturePython)
  Placement = pos=(15.5,-15.5,4) rot=(0,1,0;3.14159rad)
  diameter = 3
  invert = true
  length = 10
  matchOuter = true
  offset = 1
  thread = true
  type = 16
FEATURE [Part::FeaturePython] Screw010  label="M2.5x25-Screw014"  # Fasteners workbench fastener (typed FeaturePython)
  Placement = pos=(15.5,15.5,4) rot=(0,1,0;3.14159rad)
  diameter = 3
  invert = true
  length = 10
  matchOuter = true
  offset = 1
  thread = true
  type = 16
FEATURE [PartDesign::Body] Body018  label="Stator002"
  Origin = -> Origin040
FEATURE [Sketcher::SketchObject] Sketch064
  MapMode = 5
  Support = -> [XY_Plane030]
  sketch-geometry (4):
    g0: LineSegment StartX=-21.15 StartY=21.15 StartZ=0 EndX=21.15 EndY=21.15 EndZ=0
    g1: LineSegment StartX=21.15 StartY=21.15 StartZ=0 EndX=21.15 EndY=-21.15 EndZ=0
    g2: LineSegment StartX=21.15 StartY=-21.15 StartZ=0 EndX=-21.15 EndY=-21.15 EndZ=0
    g3: LineSegment StartX=-21.15 StartY=-21.15 StartZ=0 EndX=-21.15 EndY=21.15 EndZ=0
  constraints (11):
    c: Coincident(g0,g1)
    c: Coincident(g1,g2)
    c: Coincident(g2,g3)
    c: Coincident(g3,g0)
    c: Horizontal(g0)
    c: Horizontal(g2)
    c: Vertical(g1)
    c: Vertical(g3)
    c: Symmetric(g0,g1,g-1)
    c: DistanceX(g0,g0) = 42.3
    c: Equal(g0,g3)
FEATURE [Sketcher::SketchObject] Sketch065
  MapMode = 5
  Support = -> [XY_Plane031]
  sketch-geometry (4):
    g0: LineSegment StartX=-21.15 StartY=21.15 StartZ=0 EndX=21.15 EndY=21.15 EndZ=0
    g1: LineSegment StartX=21.15 StartY=21.15 StartZ=0 EndX=21.15 EndY=-21.15 EndZ=0
    g2: LineSegment StartX=21.15 StartY=-21.15 StartZ=0 EndX=-21.15 EndY=-21.15 EndZ=0
    g3: LineSegment StartX=-21.15 StartY=-21.15 StartZ=0 EndX=-21.15 EndY=21.15 EndZ=0
  constraints (11):
    c: Coincident(g0,g1)
    c: Coincident(g1,g2)
    c: Coincident(g2,g3)
    c: Coincident(g3,g0)
    c: Horizontal(g0)
    c: Horizontal(g2)
    c: Vertical(g1)
    c: Vertical(g3)
    c: Symmetric(g0,g1,g-1)
    c: DistanceX(g0,g0) = 42.3
    c: Equal(g0,g3)
FEATURE [PartDesign::Pad] Pad026
  Length = 7.75
  Length2 = 100
  Profile = -> Sketch065
  Refine = true
  Type = 0
FEATURE [PartDesign::Chamfer] Chamfer015
  Base = -> Pad026 [Edge8,Edge5,Edge2,Edge1]
  BaseFeature = -> Pad026
  Size = 5
FEATURE [PartDesign::Fillet] Fillet010
  Base = -> Chamfer015 [Edge22,Edge24,Edge23,Edge21,Edge12,Edge2,Edge3,Edge14]
  BaseFeature = -> Chamfer015
  Radius = 2
FEATURE [PartDesign::Pad] Pad028
  Length = 9.6
  Length2 = 100
  Profile = -> Sketch064
  Refine = true
  Type = 0
FEATURE [Sketcher::SketchObject] Sketch063
  ExternalGeometry = -> [Pad028]
  MapMode = 5
  Support = -> [XY_Plane030]
  sketch-geometry (4):
    g0: LineSegment StartX=21.15 StartY=8.2 StartZ=0 EndX=25.45 EndY=8.2 EndZ=0
    g1: LineSegment StartX=25.45 StartY=8.2 StartZ=0 EndX=25.45 EndY=-8.2 EndZ=0
    g2: LineSegment StartX=25.45 StartY=-8.2 StartZ=0 EndX=21.15 EndY=-8.2 EndZ=0
    g3: LineSegment StartX=21.15 StartY=-8.2 StartZ=0 EndX=21.15 EndY=8.2 EndZ=0
  constraints (11):
    c: Coincident(g0,g1)
    c: Coincident(g1,g2)
    c: Coincident(g2,g3)
    c: Coincident(g3,g0)
    c: Horizontal(g0)
    c: Horizontal(g2)
    c: Vertical(g3)
    c: PointOnObject(g0,g-3)
    c: Symmetric(g1,g0,g-1)
    c: DistanceX(g0,g0) = 4.3
    c: DistanceY(g1,g1) = 16.4
FEATURE [PartDesign::Pad] Pad027
  BaseFeature = -> Pad028
  Length = 3.6
  Length2 = 100
  Profile = -> Sketch063
  Refine = true
  Type = 0
FEATURE [PartDesign::Chamfer] Chamfer014
  Base = -> Pad027 [Edge13,Edge5,Edge1,Edge2]
  BaseFeature = -> Pad027
  Size = 5
FEATURE [PartDesign::Fillet] Fillet009
  Base = -> Chamfer014 [Edge33,Edge28,Edge18,Edge3,Edge2,Edge16,Edge30,Edge25]
  BaseFeature = -> Chamfer014
  Radius = 2
FEATURE [Sketcher::SketchObject] Sketch067
  MapMode = 5
  Support = -> [XY_Plane029]
  sketch-geometry (4):
    g0: LineSegment StartX=-21 StartY=21 StartZ=0 EndX=21 EndY=21 EndZ=0
    g1: LineSegment StartX=21 StartY=21 StartZ=0 EndX=21 EndY=-21 EndZ=0
    g2: LineSegment StartX=21 StartY=-21 StartZ=0 EndX=-21 EndY=-21 EndZ=0
    g3: LineSegment StartX=-21 StartY=-21 StartZ=0 EndX=-21 EndY=21 EndZ=0
  constraints (11):
    c: Coincident(g0,g1)
    c: Coincident(g1,g2)
    c: Coincident(g2,g3)
    c: Coincident(g3,g0)
    c: Horizontal(g0)
    c: Horizontal(g2)
    c: Vertical(g1)
    c: Vertical(g3)
    c: DistanceX(g0,g0) = 42
    c: Symmetric(g0,g1,g-1)
    c: Equal(g0,g3)
FEATURE [PartDesign::Pad] Pad029
  Length = 22.75
  Length2 = 100
  Profile = -> Sketch067
  Refine = true
  Type = 0
FEATURE [PartDesign::Chamfer] Chamfer013
  Base = -> Pad029 [Edge8,Edge1,Edge5,Edge2]
  BaseFeature = -> Pad029
  Size = 7.5
FEATURE [Sketcher::SketchObject] Sketch070
  MapMode = 5
  Support = -> [XY_Plane032]
  sketch-geometry (1):
    g0: Circle CenterX=0 CenterY=0 CenterZ=0 NormalX=0 NormalY=0 NormalZ=1 AngleXU=0 Radius=2.5
  constraints (2):
    c: Coincident(g0,g-1)
    c: Radius(g0) = 2.5
FEATURE [Sketcher::SketchObject] Sketch071
  MapMode = 5
  Placement = pos=(0,0,0) rot=(1,0,0;3.14159rad)
  Support = -> [Fillet009]
  sketch-geometry (8):
    g0: LineSegment [constr] StartX=-15.5 StartY=15.5 StartZ=0 EndX=15.5 EndY=15.5 EndZ=0
    g1: LineSegment [constr] StartX=15.5 StartY=15.5 StartZ=0 EndX=15.5 EndY=-15.5 EndZ=0
    g2: LineSegment [constr] StartX=15.5 StartY=-15.5 StartZ=0 EndX=-15.5 EndY=-15.5 EndZ=0
    g3: LineSegment [constr] StartX=-15.5 StartY=-15.5 StartZ=0 EndX=-15.5 EndY=15.5 EndZ=0
    g4: Circle CenterX=-15.5 CenterY=15.5 CenterZ=0 NormalX=0 NormalY=0 NormalZ=1 AngleXU=0 Radius=1.225
    g5: Circle CenterX=15.5 CenterY=15.5 CenterZ=0 NormalX=0 NormalY=0 NormalZ=1 AngleXU=0 Radius=1.225
    g6: Circle CenterX=15.5 CenterY=-15.5 CenterZ=0 NormalX=0 NormalY=0 NormalZ=1 AngleXU=0 Radius=1.225
    g7: Circle CenterX=-15.5 CenterY=-15.5 CenterZ=0 NormalX=0 NormalY=0 NormalZ=1 AngleXU=0 Radius=1.225
  constraints (19):
    c: Coincident(g0,g1)
    c: Coincident(g1,g2)
    c: Coincident(g2,g3)
    c: Coincident(g3,g0)
    c: Horizontal(g0)
    c: Horizontal(g2)
    c: Vertical(g1)
    c: Vertical(g3)
    c: Symmetric(g0,g1,g-1)
    c: DistanceX(g0,g0) = 31
    c: Equal(g3,g0)
    c: Coincident(g4,g0)
    c: Coincident(g5,g0)
    c: Coincident(g6,g1)
    c: Coincident(g7,g2)
    c: Equal(g6,g5)
    c: Equal(g5,g4)
    c: Equal(g4,g7)
    c: Radius(g4) = 1.225
FEATURE [PartDesign::Hole] Hole002
  BaseFeature = -> Fillet009
  Depth = 25
  DepthType = 0
  Diameter = 3
  DrillPoint = 1
  DrillPointAngle = 118
  HoleCutCountersinkAngle = 90
  HoleCutDepth = 5
  HoleCutDiameter = 5
  HoleCutType = 1
  ModelActualThread = false
  Profile = -> Sketch071
  Refine = true
  Tapered = false
  TaperedAngle = 90
  ThreadAngle = 0
  ThreadClass = 0
  ThreadCutOffInner = 0
  ThreadCutOffOuter = 0
  ThreadDirection = 0
  ThreadFit = 0
  ThreadPitch = 0
  ThreadSize = 0
  ThreadType = 0
  Threaded = false
FEATURE [Sketcher::SketchObject] Sketch072
  MapMode = 5
  Placement = pos=(0,0,0) rot=(1,0,0;3.14159rad)
  Support = -> [Chamfer013]
  sketch-geometry (8):
    g0: LineSegment [constr] StartX=-15.5 StartY=15.5 StartZ=0 EndX=15.5 EndY=15.5 EndZ=0
    g1: LineSegment [constr] StartX=15.5 StartY=15.5 StartZ=0 EndX=15.5 EndY=-15.5 EndZ=0
    g2: LineSegment [constr] StartX=15.5 StartY=-15.5 StartZ=0 EndX=-15.5 EndY=-15.5 EndZ=0
    g3: LineSegment [constr] StartX=-15.5 StartY=-15.5 StartZ=0 EndX=-15.5 EndY=15.5 EndZ=0
    g4: Circle CenterX=-15.5 CenterY=15.5 CenterZ=0 NormalX=0 NormalY=0 NormalZ=1 AngleXU=0 Radius=1.22
    g5: Circle CenterX=15.5 CenterY=15.5 CenterZ=0 NormalX=0 NormalY=0 NormalZ=1 AngleXU=0 Radius=1.22
    g6: Circle CenterX=15.5 CenterY=-15.5 CenterZ=0 NormalX=0 NormalY=0 NormalZ=1 AngleXU=0 Radius=1.22
    g7: Circle CenterX=-15.5 CenterY=-15.5 CenterZ=0 NormalX=0 NormalY=0 NormalZ=1 AngleXU=0 Radius=1.22
  constraints (19):
    c: Coincident(g0,g1)
    c: Coincident(g1,g2)
    c: Coincident(g2,g3)
    c: Coincident(g3,g0)
    c: Horizontal(g0)
    c: Horizontal(g2)
    c: Vertical(g1)
    c: Vertical(g3)
    c: Equal(g0,g3)
    c: Symmetric(g0,g1,g-1)
    c: DistanceX(g0,g0) = 31
    c: Coincident(g4,g0)
    c: Coincident(g5,g0)
    c: Coincident(g6,g1)
    c: Coincident(g7,g2)
    c: Equal(g6,g5)
    c: Equal(g5,g4)
    c: Equal(g4,g7)
    c: Radius(g4) = 1.22
FEATURE [PartDesign::Pocket] Pocket024
  BaseFeature = -> Chamfer013
  Length = 5
  Length2 = 100
  Profile = -> Sketch072
  Refine = true
  Type = 1
FEATURE [Sketcher::SketchObject] Sketch075
  MapMode = 5
  Placement = pos=(0,0,0) rot=(0.57735,0.57735,0.57735;2.0944rad)
  Support = -> [YZ_Plane039]
  sketch-geometry (4):
    g0: LineSegment StartX=-5.5 StartY=1 StartZ=0 EndX=5.5 EndY=1 EndZ=0
    g1: LineSegment StartX=5.5 StartY=1 StartZ=0 EndX=5.5 EndY=0 EndZ=0
    g2: LineSegment StartX=5.5 StartY=0 StartZ=0 EndX=-5.5 EndY=0 EndZ=0
    g3: LineSegment StartX=-5.5 StartY=0 StartZ=0 EndX=-5.5 EndY=1 EndZ=0
  constraints (11):
    c: Coincident(g0,g1)
    c: Coincident(g1,g2)
    c: Coincident(g2,g3)
    c: Coincident(g3,g0)
    c: Horizontal(g0)
    c: Vertical(g1)
    c: Vertical(g3)
    c: PointOnObject(g1,g-1)
    c: DistanceY(g3,g3) = 1
    c: DistanceX(g2,g2) = 11
    c: Symmetric(g1,g2,g-2)
FEATURE [PartDesign::Pad] Pad030
  Length = 60
  Length2 = 100
  Profile = -> Sketch070
  Refine = true
  Type = 0
FEATURE [Sketcher::SketchObject] Sketch066
  MapMode = 5
  Placement = pos=(0,0,60) rot=(0,0,1;0rad)
  Support = -> [Pad030]
  sketch-geometry (4):
    g0: LineSegment StartX=2 StartY=2 StartZ=0 EndX=6 EndY=2 EndZ=0
    g1: LineSegment StartX=6 StartY=2 StartZ=0 EndX=6 EndY=-2 EndZ=0
    g2: LineSegment StartX=6 StartY=-2 StartZ=0 EndX=2 EndY=-2 EndZ=0
    g3: LineSegment StartX=2 StartY=-2 StartZ=0 EndX=2 EndY=2 EndZ=0
  constraints (11):
    c: Coincident(g0,g1)
    c: Coincident(g1,g2)
    c: Coincident(g2,g3)
    c: Coincident(g3,g0)
    c: Horizontal(g0)
    c: Horizontal(g2)
    c: Vertical(g1)
    c: Symmetric(g2,g0,g-1)
    c: DistanceX(g-1,g0) = 2
    c: Equal(g0,g3)
    c: DistanceX(g0,g0) = 4
FEATURE [PartDesign::Pocket] Pocket022
  BaseFeature = -> Pad030
  Length = 16
  Length2 = 100
  Profile = -> Sketch066
  Refine = true
  Type = 0
FEATURE [PartDesign::Chamfer] Chamfer016
  Base = -> Pocket022 [Edge3,Edge5,Edge9]
  BaseFeature = -> Pocket022
  Size = 0.3
FEATURE [PartDesign::Body] Body019  label="Rotor005"
  Group = -> [Sketch070,Pad030,Sketch066,Pocket022,Chamfer016]
  Origin = -> Origin032
  Placement = pos=(0,0,2) rot=(0,0,1;0rad)
  Tip = -> Chamfer016
FEATURE [App::Part] Part016  label="Rotor004"
  Group = -> [Body019]
  Origin = -> Origin033
FEATURE [Sketcher::SketchObject] Sketch079
  MapMode = 5
  Placement = pos=(0,0,22.75) rot=(0,0,1;0rad)
  Support = -> [Pocket024]
  sketch-geometry (1):
    g0: Circle CenterX=0 CenterY=0 CenterZ=0 NormalX=0 NormalY=0 NormalZ=1 AngleXU=0 Radius=18
  constraints (2):
    c: Coincident(g0,g-1)
    c: Radius(g0) = 18
FEATURE [Sketcher::SketchObject] Sketch080
  MapMode = 5
  Placement = pos=(0,0,7.75) rot=(0,0,1;0rad)
  Support = -> [Fillet010]
  sketch-geometry (8):
    g0: LineSegment [constr] StartX=-15.5 StartY=15.5 StartZ=0 EndX=15.5 EndY=15.5 EndZ=0
    g1: LineSegment [constr] StartX=15.5 StartY=15.5 StartZ=0 EndX=15.5 EndY=-15.5 EndZ=0
    g2: LineSegment [constr] StartX=15.5 StartY=-15.5 StartZ=0 EndX=-15.5 EndY=-15.5 EndZ=0
    g3: LineSegment [constr] StartX=-15.5 StartY=-15.5 StartZ=0 EndX=-15.5 EndY=15.5 EndZ=0
    g4: Circle CenterX=-15.5 CenterY=15.5 CenterZ=0 NormalX=0 NormalY=0 NormalZ=1 AngleXU=0 Radius=1.225
    g5: Circle CenterX=15.5 CenterY=15.5 CenterZ=0 NormalX=0 NormalY=0 NormalZ=1 AngleXU=0 Radius=1.225
    g6: Circle CenterX=15.5 CenterY=-15.5 CenterZ=0 NormalX=0 NormalY=0 NormalZ=1 AngleXU=0 Radius=1.225
    g7: Circle CenterX=-15.5 CenterY=-15.5 CenterZ=0 NormalX=0 NormalY=0 NormalZ=1 AngleXU=0 Radius=1.225
  constraints (19):
    c: Coincident(g0,g1)
    c: Coincident(g1,g2)
    c: Coincident(g2,g3)
    c: Coincident(g3,g0)
    c: Horizontal(g0)
    c: Horizontal(g2)
    c: Vertical(g1)
    c: Vertical(g3)
    c: Equal(g0,g3)
    c: Symmetric(g0,g1,g-1)
    c: DistanceX(g0,g0) = 31
    c: Coincident(g4,g0)
    c: Coincident(g7,g2)
    c: Coincident(g0,g5)
    c: Coincident(g1,g6)
    c: Equal(g7,g4)
    c: Equal(g4,g5)
    c: Equal(g5,g6)
    c: Radius(g4) = 1.225
FEATURE [PartDesign::Pocket] Pocket027
  BaseFeature = -> Fillet010
  Length = 5
  Length2 = 100
  Profile = -> Sketch080
  Refine = true
  Type = 1
FEATURE [Sketcher::SketchObject] Sketch068
  MapMode = 5
  Placement = pos=(0,0,7.75) rot=(0,0,1;0rad)
  Support = -> [Pocket027]
  sketch-geometry (1):
    g0: Circle CenterX=0 CenterY=0 CenterZ=0 NormalX=0 NormalY=0 NormalZ=1 AngleXU=0 Radius=14
  constraints (2):
    c: Coincident(g0,g-1)
    c: Radius(g0) = 14
FEATURE [PartDesign::Pocket] Pocket025
  BaseFeature = -> Pocket027
  Length = 1
  Length2 = 100
  Profile = -> Sketch068
  Refine = true
  Type = 0
FEATURE [Sketcher::SketchObject] Sketch069
  MapMode = 5
  Placement = pos=(0,0,6.75) rot=(0,0,1;0rad)
  Support = -> [Pocket025]
  sketch-geometry (1):
    g0: Circle CenterX=0 CenterY=0 CenterZ=0 NormalX=0 NormalY=0 NormalZ=1 AngleXU=0 Radius=11
  constraints (2):
    c: Coincident(g0,g-1)
    c: Radius(g0) = 11
FEATURE [PartDesign::Pad] Pad032
  BaseFeature = -> Pocket025
  Length = 3
  Length2 = 100
  Profile = -> Sketch069
  Refine = true
  Type = 0
FEATURE [PartDesign::Draft] Draft002
  Angle = 10
  Base = -> Pad032 [Face25]
  BaseFeature = -> Pad032
  NeutralPlane = -> Pad032 [Face24]
FEATURE [Sketcher::SketchObject] Sketch081
  MapMode = 5
  Placement = pos=(0,0,9.75) rot=(0,0,1;0rad)
  Support = -> [Draft002]
  sketch-geometry (1):
    g0: Circle CenterX=0 CenterY=0 CenterZ=0 NormalX=0 NormalY=0 NormalZ=1 AngleXU=0 Radius=5
  constraints (2):
    c: Coincident(g0,g-1)
    c: Radius(g0) = 5
FEATURE [PartDesign::Pocket] Pocket026
  BaseFeature = -> Draft002
  Length = 8
  Length2 = 100
  Profile = -> Sketch081
  Refine = true
  Type = 1
FEATURE [Sketcher::SketchObject] Sketch078
  MapMode = 5
  Placement = pos=(0,0,0) rot=(1,0,0;3.14159rad)
  Support = -> [Pocket026]
  sketch-geometry (1):
    g0: Circle CenterX=0 CenterY=0 CenterZ=0 NormalX=0 NormalY=0 NormalZ=1 AngleXU=0 Radius=15.35
  constraints (2):
    c: Coincident(g0,g-1)
    c: Radius(g0) = 15.35
FEATURE [PartDesign::Pocket] Pocket029
  BaseFeature = -> Pocket024
  Length = 5
  Length2 = 100
  Profile = -> Sketch079
  Refine = true
  Type = 1
FEATURE [PartDesign::Body] Body017
  Group = -> [Sketch067,Pad029,Chamfer013,Sketch072,Pocket024,Sketch079,Pocket029]
  Origin = -> Origin031
  Placement = pos=(0,0,9.6) rot=(0,0,1;0rad)
  Tip = -> Pocket029
FEATURE [App::Part] Part017  label="Body016"
  Group = -> [Body017,Body018]
  Origin = -> Origin034
FEATURE [Part::FeaturePython] Screw011  label="M2.5x25-Screw015"  # Fasteners workbench fastener (typed FeaturePython)
  Placement = pos=(-15.5,15.5,4) rot=(0,1,0;3.14159rad)
  diameter = 3
  invert = true
  length = 10
  matchOuter = true
  offset = 1
  thread = true
  type = 16
FEATURE [App::Part] Part018  label="Screw010"
  Group = -> [Screw010,Screw008,Screw009,Screw011]
  Origin = -> Origin041
FEATURE [Sketcher::SketchObject] Sketch082
  ExternalGeometry = -> [Hole002]
  MapMode = 5
  Placement = pos=(21.15,0,0) rot=(0.57735,0.57735,0.57735;2.0944rad)
  Support = -> [Hole002]
  sketch-geometry (4):
    g0: LineSegment StartX=-8.2 StartY=3.6 StartZ=0 EndX=8.2 EndY=3.6 EndZ=0
    g1: LineSegment StartX=8.2 StartY=3.6 StartZ=0 EndX=8.2 EndY=9.6 EndZ=0
    g2: LineSegment StartX=8.2 StartY=9.6 StartZ=0 EndX=-8.2 EndY=9.6 EndZ=0
    g3: LineSegment StartX=-8.2 StartY=9.6 StartZ=0 EndX=-8.2 EndY=3.6 EndZ=0
  constraints (10):
    c: Coincident(g0,g1)
    c: Coincident(g1,g2)
    c: Coincident(g2,g3)
    c: Coincident(g3,g0)
    c: Horizontal(g0)
    c: Vertical(g1)
    c: Vertical(g3)
    c: Coincident(g0,g-3)
    c: PointOnObject(g1,g-5)
    c: Symmetric(g2,g1,g-2)
FEATURE [PartDesign::Pocket] Pocket028
  BaseFeature = -> Hole002
  Length = 4
  Length2 = 100
  Profile = -> Sketch082
  Refine = true
  Type = 0
FEATURE [PartDesign::Body] Body016  label="Aluminium rear005"
  Group = -> [Sketch064,Pad028,Sketch063,Pad027,Chamfer014,Fillet009,Sketch071,Hole002,Sketch082,Pocket028]
  Origin = -> Origin028
  Tip = -> Pocket028
FEATURE [App::Part] Part015  label="Aluminium rear004"
  Group = -> [Body016]
  Origin = -> Origin036
FEATURE [Sketcher::SketchObject] Sketch083
  MapMode = 5
  Placement = pos=(0,0,0) rot=(0.57735,0.57735,0.57735;2.0944rad)
  Support = -> [YZ_Plane038]
  sketch-geometry (4):
    g0: LineSegment StartX=-7.5 StartY=0 StartZ=0 EndX=7.5 EndY=0 EndZ=0
    g1: LineSegment StartX=7.5 StartY=0 StartZ=0 EndX=7.5 EndY=5 EndZ=0
    g2: LineSegment StartX=7.5 StartY=5 StartZ=0 EndX=-7.5 EndY=5 EndZ=0
    g3: LineSegment StartX=-7.5 StartY=5 StartZ=0 EndX=-7.5 EndY=0 EndZ=0
  constraints (11):
    c: Coincident(g0,g1)
    c: Coincident(g1,g2)
    c: Coincident(g2,g3)
    c: Coincident(g3,g0)
    c: Horizontal(g0)
    c: Horizontal(g2)
    c: Vertical(g1)
    c: Vertical(g3)
    c: Symmetric(g0,g0,g-1)
    c: DistanceX(g0,g0) = 15
    c: DistanceY(g3,g3) = 5
FEATURE [PartDesign::Pad] Pad031
  Length = 10
  Length2 = 100
  Placement = pos=(0,0,0) rot=(0.57735,0.57735,0.57735;2.0944rad)
  Profile = -> Sketch083
  Refine = true
  Type = 0
FEATURE [Sketcher::SketchObject] Sketch076
  ExternalGeometry = -> [Pad031]
  MapMode = 5
  Placement = pos=(10,0,0) rot=(0.57735,0.57735,0.57735;2.0944rad)
  Support = -> [Pad031]
  sketch-geometry (8):
    g0: LineSegment StartX=-6.5 StartY=4 StartZ=0 EndX=6.5 EndY=4 EndZ=0
    g1: LineSegment StartX=6.5 StartY=4 StartZ=0 EndX=6.5 EndY=1 EndZ=0
    g2: LineSegment StartX=6.5 StartY=1 StartZ=0 EndX=-6.5 EndY=1 EndZ=0
    g3: LineSegment StartX=-6.5 StartY=1 StartZ=0 EndX=-6.5 EndY=4 EndZ=0
    g4: LineSegment [constr] StartX=-6.5 StartY=1 StartZ=0 EndX=-7.5 EndY=1 EndZ=0
    g5: LineSegment [constr] StartX=-6.5 StartY=1 StartZ=0 EndX=-6.5 EndY=0 EndZ=0
    g6: LineSegment [constr] StartX=6.5 StartY=4 StartZ=0 EndX=6.5 EndY=5 EndZ=0
    g7: LineSegment [constr] StartX=6.5 StartY=4 StartZ=0 EndX=7.5 EndY=4 EndZ=0
  constraints (23):
    c: Coincident(g0,g1)
    c: Coincident(g1,g2)
    c: Coincident(g2,g3)
    c: Coincident(g3,g0)
    c: Horizontal(g2)
    c: Vertical(g1)
    c: Vertical(g3)
    c: Symmetric(g0,g0,g-2)
    c: Coincident(g4,g2)
    c: PointOnObject(g4,g-4)
    c: Horizontal(g4)
    c: PointOnObject(g5,g-1)
    c: Vertical(g5)
    c: Coincident(g6,g0)
    c: Coincident(g7,g0)
    c: Horizontal(g7)
    c: Vertical(g6)
    c: PointOnObject(g6,g-5)
    c: Equal(g7,g6)
    c: Equal(g6,g4)
    c: Equal(g4,g5)
    c: DistanceX(g4,g4) = 1
    c: Coincident(g5,g2)
FEATURE [PartDesign::Pocket] Pocket023
  BaseFeature = -> Pad031
  Length = 6
  Length2 = 100
  Placement = pos=(0,0,0) rot=(0.57735,0.57735,0.57735;2.0944rad)
  Profile = -> Sketch076
  Refine = true
  Type = 0
FEATURE [Sketcher::SketchObject] Sketch077
  ExternalGeometry = -> [Pocket023]
  MapMode = 5
  Placement = pos=(10,0,0) rot=(0.57735,0.57735,0.57735;2.0944rad)
  Support = -> [Pocket023]
  sketch-geometry (4):
    g0: LineSegment StartX=-4 StartY=5 StartZ=0 EndX=4 EndY=5 EndZ=0
    g1: LineSegment StartX=4 StartY=5 StartZ=0 EndX=4 EndY=4 EndZ=0
    g2: LineSegment StartX=4 StartY=4 StartZ=0 EndX=-4 EndY=4 EndZ=0
    g3: LineSegment StartX=-4 StartY=4 StartZ=0 EndX=-4 EndY=5 EndZ=0
  constraints (11):
    c: Coincident(g0,g1)
    c: Coincident(g1,g2)
    c: Coincident(g2,g3)
    c: Coincident(g3,g0)
    c: Horizontal(g0)
    c: Vertical(g1)
    c: Vertical(g3)
    c: PointOnObject(g0,g-3)
    c: PointOnObject(g1,g-4)
    c: Symmetric(g1,g2,g-2)
    c: DistanceX(g0,g0) = 8
FEATURE [PartDesign::Pocket] Pocket030
  BaseFeature = -> Pocket023
  Length = 4.5
  Length2 = 100
  Placement = pos=(0,0,0) rot=(0.57735,0.57735,0.57735;2.0944rad)
  Profile = -> Sketch077
  Refine = true
  Type = 0
FEATURE [Sketcher::SketchObject] Sketch073
  ExternalGeometry = -> [Pocket030]
  MapMode = 5
  Placement = pos=(0,0,5) rot=(0,0,-1;1.5708rad)
  Support = -> [Pocket030]
  sketch-geometry (11):
    g0: LineSegment StartX=-6.49 StartY=8.99 StartZ=0 EndX=-5.01 EndY=8.99 EndZ=0
    g1: LineSegment StartX=-5.01 StartY=8.99 StartZ=0 EndX=-5.01 EndY=4.5 EndZ=0
    g2: LineSegment StartX=-5.01 StartY=4.5 StartZ=0 EndX=-6.49 EndY=4.5 EndZ=0
    g3: LineSegment StartX=-6.49 StartY=4.5 StartZ=0 EndX=-6.49 EndY=8.99 EndZ=0
    g4: LineSegment StartX=5.01 StartY=8.99 StartZ=0 EndX=6.49 EndY=8.99 EndZ=0
    g5: LineSegment StartX=6.49 StartY=8.99 StartZ=0 EndX=6.49 EndY=4.5 EndZ=0
    g6: LineSegment StartX=6.49 StartY=4.5 StartZ=0 EndX=5.01 EndY=4.5 EndZ=0
    g7: LineSegment StartX=5.01 StartY=4.5 StartZ=0 EndX=5.01 EndY=8.99 EndZ=0
    g8: LineSegment [constr] StartX=-7.5 StartY=8.99 StartZ=0 EndX=-6.49 EndY=8.99 EndZ=0
    g9: LineSegment [constr] StartX=-6.49 StartY=10 StartZ=0 EndX=-6.49 EndY=8.99 EndZ=0
    g10: LineSegment [constr] StartX=-5.01 StartY=8.99 StartZ=0 EndX=-4 EndY=8.99 EndZ=0
  constraints (32):
    c: Coincident(g0,g1)
    c: Coincident(g1,g2)
    c: Coincident(g2,g3)
    c: Coincident(g3,g0)
    c: Horizontal(g0)
    c: Horizontal(g2)
    c: Vertical(g1)
    c: Vertical(g3)
    c: Coincident(g4,g5)
    c: Coincident(g5,g6)
    c: Coincident(g6,g7)
    c: Coincident(g7,g4)
    c: Horizontal(g4)
    c: Horizontal(g6)
    c: Vertical(g5)
    c: Vertical(g7)
    c: DistanceX(g4,g4) = 1.48
    c: Equal(g0,g4)
    c: Equal(g7,g1)
    c: PointOnObject(g8,g-4)
    c: Coincident(g8,g0)
    c: Horizontal(g8)
    c: PointOnObject(g9,g-5)
    c: Coincident(g9,g0)
    c: Vertical(g9)
    c: Coincident(g10,g0)
    c: PointOnObject(g10,g-3)
    c: Horizontal(g10)
    c: Symmetric(g4,g0,g-2)
    c: Equal(g10,g9)
    c: Equal(g9,g8)
    c: DistanceY(g3,g3) = 4.49
FEATURE [PartDesign::Pad] Pad033
  Length = 1
  Length2 = 100
  Placement = pos=(0,0,0) rot=(0.57735,0.57735,0.57735;2.0944rad)
  Profile = -> Sketch075
  Refine = true
  Type = 0
FEATURE [Sketcher::SketchObject] Sketch074
  ExternalGeometry = -> [Pad033]
  MapMode = 5
  Placement = pos=(0,0,1) rot=(0,0,-1;1.5708rad)
  Support = -> [Pad033]
  sketch-geometry (7):
    g0: LineSegment StartX=-5.5 StartY=1 StartZ=0 EndX=-4.5 EndY=1 EndZ=0
    g1: LineSegment StartX=-4.5 StartY=1 StartZ=0 EndX=-4.5 EndY=8 EndZ=0
    g2: LineSegment [constr] StartX=-4.5 StartY=8 StartZ=0 EndX=-5.5 EndY=8 EndZ=0
    g3: LineSegment StartX=-5.5 StartY=8 StartZ=0 EndX=-5.5 EndY=1 EndZ=0
    g4: LineSegment StartX=-5.5 StartY=8 StartZ=0 EndX=-5.25 EndY=8.7 EndZ=0
    g5: LineSegment StartX=-5.25 StartY=8.7 StartZ=0 EndX=-4.75 EndY=8.7 EndZ=0
    g6: LineSegment StartX=-4.75 StartY=8.7 StartZ=0 EndX=-4.5 EndY=8 EndZ=0
  constraints (19):
    c: Coincident(g0,g1)
    c: Coincident(g1,g2)
    c: Coincident(g2,g3)
    c: Coincident(g3,g0)
    c: Horizontal(g0)
    c: Horizontal(g2)
    c: Vertical(g1)
    c: Vertical(g3)
    c: Coincident(g0,g-3)
    c: Coincident(g2,g4)
    c: Coincident(g4,g5)
    c: Horizontal(g5)
    c: Coincident(g5,g6)
    c: Coincident(g6,g1)
    c: DistanceY(g1,g5) = 0.7
    c: DistanceX(g5,g5) = 0.5
    c: Equal(g6,g4)
    c: DistanceX(g0,g0) = 1
    c: DistanceY(g3,g3) = 7
FEATURE [PartDesign::Pocket] Pocket031
  BaseFeature = -> Pocket026
  Length = 5
  Length2 = 100
  Profile = -> Sketch078
  Refine = true
  Type = 0
FEATURE [PartDesign::Body] Body014  label="Aluminum front005"
  Group = -> [Sketch065,Pad026,Chamfer015,Fillet010,Sketch080,Pocket027,Sketch068,Pocket025,Sketch069,Pad032,Draft002,Sketch081,Pocket026,Sketch078,Pocket031]
  Origin = -> Origin030
  Placement = pos=(0,0,32.35) rot=(0,0,1;0rad)
  Tip = -> Pocket031
FEATURE [App::Part] Part020  label="Aluminum front004"
  Group = -> [Body014]
  Origin = -> Origin035
FEATURE [PartDesign::Pad] Pad034
  BaseFeature = -> Pad033
  Length = 1
  Length2 = 100
  Placement = pos=(0,0,0) rot=(0.57735,0.57735,0.57735;2.0944rad)
  Profile = -> Sketch074
  Refine = true
  Reversed = true
  Type = 0
FEATURE [PartDesign::LinearPattern] LinearPattern002
  BaseFeature = -> Pad034
  Direction = -> Pad034 [Edge10]
  Length = 10
  Occurrences = 6
  Originals = -> [Pad034]
  Placement = pos=(0,0,0) rot=(0.57735,0.57735,0.57735;2.0944rad)
  Refine = true
  Reversed = true
FEATURE [PartDesign::Body] Body020  label="pin002"
  Group = -> [Sketch075,Pad033,Sketch074,Pad034,LinearPattern002]
  Origin = -> Origin039
  Placement = pos=(0,0,2) rot=(0,0,1;0rad)
  Tip = -> LinearPattern002
FEATURE [PartDesign::Pocket] Pocket032
  BaseFeature = -> Pocket030
  Length = 2
  Length2 = 100
  Placement = pos=(0,0,0) rot=(0.57735,0.57735,0.57735;2.0944rad)
  Profile = -> Sketch073
  Refine = true
  Type = 0
FEATURE [PartDesign::Body] Body015  label="conector002"
  Group = -> [Sketch083,Pad031,Sketch076,Pocket023,Sketch077,Pocket030,Sketch073,Pocket032]
  Origin = -> Origin038
  Tip = -> Pocket032
FEATURE [App::Part] Part014  label="Conector002"
  Group = -> [Body015,Body020]
  Origin = -> Origin037
  Placement = pos=(17,0,4) rot=(0,0,1;0rad)
FEATURE [App::Part] Part019  label="Nema 018"
  Group = -> [Part015,Part017,Part020,Part016,Part018,Part014]
  Origin = -> Origin029
  Placement = pos=(41,306,51) rot=(0,0,1;0rad)
FEATURE [Part::FeaturePython] Screw012  label="M2.5x25-Screw016"  # Fasteners workbench fastener (typed FeaturePython)
  Placement = pos=(-15.5,15.5,4) rot=(0,1,0;3.14159rad)
  diameter = 3
  invert = true
  length = 10
  matchOuter = true
  offset = 1
  thread = true
  type = 16
FEATURE [Part::FeaturePython] Screw013  label="M2.5x25-Screw017"  # Fasteners workbench fastener (typed FeaturePython)
  Placement = pos=(15.5,-15.5,4) rot=(0,1,0;3.14159rad)
  diameter = 3
  invert = true
  length = 10
  matchOuter = true
  offset = 1
  thread = true
  type = 16
FEATURE [Part::FeaturePython] Screw014  label="M2.5x25-Screw018"  # Fasteners workbench fastener (typed FeaturePython)
  Placement = pos=(15.5,15.5,4) rot=(0,1,0;3.14159rad)
  diameter = 3
  invert = true
  length = 10
  matchOuter = true
  offset = 1
  thread = true
  type = 16
FEATURE [Part::FeaturePython] Screw015  label="M2.5x25-Screw019"  # Fasteners workbench fastener (typed FeaturePython)
  Placement = pos=(-15.5,-15.5,4) rot=(0,1,0;3.14159rad)
  diameter = 3
  invert = true
  length = 10
  matchOuter = true
  offset = 1
  thread = true
  type = 16
FEATURE [Sketcher::SketchObject] Sketch085
  MapMode = 5
  Placement = pos=(0,0,0) rot=(0.57735,0.57735,0.57735;2.0944rad)
  Support = -> [YZ_Plane045]
  sketch-geometry (4):
    g0: LineSegment StartX=-5.5 StartY=1 StartZ=0 EndX=5.5 EndY=1 EndZ=0
    g1: LineSegment StartX=5.5 StartY=1 StartZ=0 EndX=5.5 EndY=0 EndZ=0
    g2: LineSegment StartX=5.5 StartY=0 StartZ=0 EndX=-5.5 EndY=0 EndZ=0
    g3: LineSegment StartX=-5.5 StartY=0 StartZ=0 EndX=-5.5 EndY=1 EndZ=0
  constraints (11):
    c: Coincident(g0,g1)
    c: Coincident(g1,g2)
    c: Coincident(g2,g3)
    c: Coincident(g3,g0)
    c: Horizontal(g0)
    c: Vertical(g1)
    c: Vertical(g3)
    c: PointOnObject(g1,g-1)
    c: DistanceY(g3,g3) = 1
    c: DistanceX(g2,g2) = 11
    c: Symmetric(g1,g2,g-2)
FEATURE [Sketcher::SketchObject] Sketch089
  MapMode = 5
  Support = -> [XY_Plane054]
  sketch-geometry (1):
    g0: Circle CenterX=0 CenterY=0 CenterZ=0 NormalX=0 NormalY=0 NormalZ=1 AngleXU=0 Radius=2.5
  constraints (2):
    c: Coincident(g0,g-1)
    c: Radius(g0) = 2.5
FEATURE [PartDesign::Body] Body026  label="Stator003"
  Origin = -> Origin050
FEATURE [Sketcher::SketchObject] Sketch096
  MapMode = 5
  Placement = pos=(0,0,0) rot=(0.57735,0.57735,0.57735;2.0944rad)
  Support = -> [YZ_Plane044]
  sketch-geometry (4):
    g0: LineSegment StartX=-7.5 StartY=0 StartZ=0 EndX=7.5 EndY=0 EndZ=0
    g1: LineSegment StartX=7.5 StartY=0 StartZ=0 EndX=7.5 EndY=5 EndZ=0
    g2: LineSegment StartX=7.5 StartY=5 StartZ=0 EndX=-7.5 EndY=5 EndZ=0
    g3: LineSegment StartX=-7.5 StartY=5 StartZ=0 EndX=-7.5 EndY=0 EndZ=0
  constraints (11):
    c: Coincident(g0,g1)
    c: Coincident(g1,g2)
    c: Coincident(g2,g3)
    c: Coincident(g3,g0)
    c: Horizontal(g0)
    c: Horizontal(g2)
    c: Vertical(g1)
    c: Vertical(g3)
    c: Symmetric(g0,g0,g-1)
    c: DistanceX(g0,g0) = 15
    c: DistanceY(g3,g3) = 5
FEATURE [PartDesign::Pad] Pad038
  Length = 60
  Length2 = 100
  Profile = -> Sketch089
  Refine = true
  Type = 0
FEATURE [PartDesign::Pad] Pad040
  Length = 10
  Length2 = 100
  Placement = pos=(0,0,0) rot=(0.57735,0.57735,0.57735;2.0944rad)
  Profile = -> Sketch096
  Refine = true
  Type = 0
FEATURE [Sketcher::SketchObject] Sketch094
  ExternalGeometry = -> [Pad040]
  MapMode = 5
  Placement = pos=(10,0,0) rot=(0.57735,0.57735,0.57735;2.0944rad)
  Support = -> [Pad040]
  sketch-geometry (8):
    g0: LineSegment StartX=-6.5 StartY=4 StartZ=0 EndX=6.5 EndY=4 EndZ=0
    g1: LineSegment StartX=6.5 StartY=4 StartZ=0 EndX=6.5 EndY=1 EndZ=0
    g2: LineSegment StartX=6.5 StartY=1 StartZ=0 EndX=-6.5 EndY=1 EndZ=0
    g3: LineSegment StartX=-6.5 StartY=1 StartZ=0 EndX=-6.5 EndY=4 EndZ=0
    g4: LineSegment [constr] StartX=-6.5 StartY=1 StartZ=0 EndX=-7.5 EndY=1 EndZ=0
    g5: LineSegment [constr] StartX=-6.5 StartY=1 StartZ=0 EndX=-6.5 EndY=0 EndZ=0
    g6: LineSegment [constr] StartX=6.5 StartY=4 StartZ=0 EndX=6.5 EndY=5 EndZ=0
    g7: LineSegment [constr] StartX=6.5 StartY=4 StartZ=0 EndX=7.5 EndY=4 EndZ=0
  constraints (23):
    c: Coincident(g0,g1)
    c: Coincident(g1,g2)
    c: Coincident(g2,g3)
    c: Coincident(g3,g0)
    c: Horizontal(g2)
    c: Vertical(g1)
    c: Vertical(g3)
    c: Symmetric(g0,g0,g-2)
    c: Coincident(g4,g2)
    c: PointOnObject(g4,g-4)
    c: Horizontal(g4)
    c: PointOnObject(g5,g-1)
    c: Vertical(g5)
    c: Coincident(g6,g0)
    c: Coincident(g7,g0)
    c: Horizontal(g7)
    c: Vertical(g6)
    c: PointOnObject(g6,g-5)
    c: Equal(g7,g6)
    c: Equal(g6,g4)
    c: Equal(g4,g5)
    c: DistanceX(g4,g4) = 1
    c: Coincident(g5,g2)
FEATURE [PartDesign::Pocket] Pocket035
  BaseFeature = -> Pad040
  Length = 6
  Length2 = 100
  Placement = pos=(0,0,0) rot=(0.57735,0.57735,0.57735;2.0944rad)
  Profile = -> Sketch094
  Refine = true
  Type = 0
FEATURE [Sketcher::SketchObject] Sketch091
  ExternalGeometry = -> [Pocket035]
  MapMode = 5
  Placement = pos=(10,0,0) rot=(0.57735,0.57735,0.57735;2.0944rad)
  Support = -> [Pocket035]
  sketch-geometry (4):
    g0: LineSegment StartX=-4 StartY=5 StartZ=0 EndX=4 EndY=5 EndZ=0
    g1: LineSegment StartX=4 StartY=5 StartZ=0 EndX=4 EndY=4 EndZ=0
    g2: LineSegment StartX=4 StartY=4 StartZ=0 EndX=-4 EndY=4 EndZ=0
    g3: LineSegment StartX=-4 StartY=4 StartZ=0 EndX=-4 EndY=5 EndZ=0
  constraints (11):
    c: Coincident(g0,g1)
    c: Coincident(g1,g2)
    c: Coincident(g2,g3)
    c: Coincident(g3,g0)
    c: Horizontal(g0)
    c: Vertical(g1)
    c: Vertical(g3)
    c: PointOnObject(g0,g-3)
    c: PointOnObject(g1,g-4)
    c: Symmetric(g1,g2,g-2)
    c: DistanceX(g0,g0) = 8
FEATURE [PartDesign::Pad] Pad042
  Length = 1
  Length2 = 100
  Placement = pos=(0,0,0) rot=(0.57735,0.57735,0.57735;2.0944rad)
  Profile = -> Sketch085
  Refine = true
  Type = 0
FEATURE [Sketcher::SketchObject] Sketch090
  ExternalGeometry = -> [Pad042]
  MapMode = 5
  Placement = pos=(0,0,1) rot=(0,0,-1;1.5708rad)
  Support = -> [Pad042]
  sketch-geometry (7):
    g0: LineSegment StartX=-5.5 StartY=1 StartZ=0 EndX=-4.5 EndY=1 EndZ=0
    g1: LineSegment StartX=-4.5 StartY=1 StartZ=0 EndX=-4.5 EndY=8 EndZ=0
    g2: LineSegment [constr] StartX=-4.5 StartY=8 StartZ=0 EndX=-5.5 EndY=8 EndZ=0
    g3: LineSegment StartX=-5.5 StartY=8 StartZ=0 EndX=-5.5 EndY=1 EndZ=0
    g4: LineSegment StartX=-5.5 StartY=8 StartZ=0 EndX=-5.25 EndY=8.7 EndZ=0
    g5: LineSegment StartX=-5.25 StartY=8.7 StartZ=0 EndX=-4.75 EndY=8.7 EndZ=0
    g6: LineSegment StartX=-4.75 StartY=8.7 StartZ=0 EndX=-4.5 EndY=8 EndZ=0
  constraints (19):
    c: Coincident(g0,g1)
    c: Coincident(g1,g2)
    c: Coincident(g2,g3)
    c: Coincident(g3,g0)
    c: Horizontal(g0)
    c: Horizontal(g2)
    c: Vertical(g1)
    c: Vertical(g3)
    c: Coincident(g0,g-3)
    c: Coincident(g2,g4)
    c: Coincident(g4,g5)
    c: Horizontal(g5)
    c: Coincident(g5,g6)
    c: Coincident(g6,g1)
    c: DistanceY(g1,g5) = 0.7
    c: DistanceX(g5,g5) = 0.5
    c: Equal(g6,g4)
    c: DistanceX(g0,g0) = 1
    c: DistanceY(g3,g3) = 7
FEATURE [PartDesign::Pad] Pad043
  BaseFeature = -> Pad042
  Length = 1
  Length2 = 100
  Placement = pos=(0,0,0) rot=(0.57735,0.57735,0.57735;2.0944rad)
  Profile = -> Sketch090
  Refine = true
  Reversed = true
  Type = 0
FEATURE [PartDesign::LinearPattern] LinearPattern003
  BaseFeature = -> Pad043
  Direction = -> Pad043 [Edge10]
  Length = 10
  Occurrences = 6
  Originals = -> [Pad043]
  Placement = pos=(0,0,0) rot=(0.57735,0.57735,0.57735;2.0944rad)
  Refine = true
  Reversed = true
FEATURE [PartDesign::Body] Body027  label="pin003"
  Group = -> [Sketch085,Pad042,Sketch090,Pad043,LinearPattern003]
  Origin = -> Origin047
  Placement = pos=(0,0,2) rot=(0,0,1;0rad)
  Tip = -> LinearPattern003
FEATURE [PartDesign::Pocket] Pocket041
  BaseFeature = -> Pocket035
  Length = 4.5
  Length2 = 100
  Placement = pos=(0,0,0) rot=(0.57735,0.57735,0.57735;2.0944rad)
  Profile = -> Sketch091
  Refine = true
  Type = 0
FEATURE [Sketcher::SketchObject] Sketch088
  ExternalGeometry = -> [Pocket041]
  MapMode = 5
  Placement = pos=(0,0,5) rot=(0,0,-1;1.5708rad)
  Support = -> [Pocket041]
  sketch-geometry (11):
    g0: LineSegment StartX=-6.49 StartY=8.99 StartZ=0 EndX=-5.01 EndY=8.99 EndZ=0
    g1: LineSegment StartX=-5.01 StartY=8.99 StartZ=0 EndX=-5.01 EndY=4.5 EndZ=0
    g2: LineSegment StartX=-5.01 StartY=4.5 StartZ=0 EndX=-6.49 EndY=4.5 EndZ=0
    g3: LineSegment StartX=-6.49 StartY=4.5 StartZ=0 EndX=-6.49 EndY=8.99 EndZ=0
    g4: LineSegment StartX=5.01 StartY=8.99 StartZ=0 EndX=6.49 EndY=8.99 EndZ=0
    g5: LineSegment StartX=6.49 StartY=8.99 StartZ=0 EndX=6.49 EndY=4.5 EndZ=0
    g6: LineSegment StartX=6.49 StartY=4.5 StartZ=0 EndX=5.01 EndY=4.5 EndZ=0
    g7: LineSegment StartX=5.01 StartY=4.5 StartZ=0 EndX=5.01 EndY=8.99 EndZ=0
    g8: LineSegment [constr] StartX=-7.5 StartY=8.99 StartZ=0 EndX=-6.49 EndY=8.99 EndZ=0
    g9: LineSegment [constr] StartX=-6.49 StartY=10 StartZ=0 EndX=-6.49 EndY=8.99 EndZ=0
    g10: LineSegment [constr] StartX=-5.01 StartY=8.99 StartZ=0 EndX=-4 EndY=8.99 EndZ=0
  constraints (32):
    c: Coincident(g0,g1)
    c: Coincident(g1,g2)
    c: Coincident(g2,g3)
    c: Coincident(g3,g0)
    c: Horizontal(g0)
    c: Horizontal(g2)
    c: Vertical(g1)
    c: Vertical(g3)
    c: Coincident(g4,g5)
    c: Coincident(g5,g6)
    c: Coincident(g6,g7)
    c: Coincident(g7,g4)
    c: Horizontal(g4)
    c: Horizontal(g6)
    c: Vertical(g5)
    c: Vertical(g7)
    c: DistanceX(g4,g4) = 1.48
    c: Equal(g0,g4)
    c: Equal(g7,g1)
    c: PointOnObject(g8,g-4)
    c: Coincident(g8,g0)
    c: Horizontal(g8)
    c: PointOnObject(g9,g-5)
    c: Coincident(g9,g0)
    c: Vertical(g9)
    c: Coincident(g10,g0)
    c: PointOnObject(g10,g-3)
    c: Horizontal(g10)
    c: Symmetric(g4,g0,g-2)
    c: Equal(g10,g9)
    c: Equal(g9,g8)
    c: DistanceY(g3,g3) = 4.49
FEATURE [PartDesign::Pocket] Pocket043
  BaseFeature = -> Pocket041
  Length = 2
  Length2 = 100
  Placement = pos=(0,0,0) rot=(0.57735,0.57735,0.57735;2.0944rad)
  Profile = -> Sketch088
  Refine = true
  Type = 0
FEATURE [PartDesign::Body] Body023  label="conector003"
  Group = -> [Sketch096,Pad040,Sketch094,Pocket035,Sketch091,Pocket041,Sketch088,Pocket043]
  Origin = -> Origin046
  Tip = -> Pocket043
FEATURE [App::Part] Part021  label="Conector003"
  Group = -> [Body023,Body027]
  Origin = -> Origin053
  Placement = pos=(17,0,4) rot=(0,0,1;0rad)
FEATURE [App::Part] Part024  label="Screw014"
  Group = -> [Screw014,Screw015,Screw013,Screw012]
  Origin = -> Origin045
FEATURE [Sketcher::SketchObject] Sketch099
  MapMode = 5
  Support = -> [XY_Plane055]
  sketch-geometry (4):
    g0: LineSegment StartX=-21.15 StartY=21.15 StartZ=0 EndX=21.15 EndY=21.15 EndZ=0
    g1: LineSegment StartX=21.15 StartY=21.15 StartZ=0 EndX=21.15 EndY=-21.15 EndZ=0
    g2: LineSegment StartX=21.15 StartY=-21.15 StartZ=0 EndX=-21.15 EndY=-21.15 EndZ=0
    g3: LineSegment StartX=-21.15 StartY=-21.15 StartZ=0 EndX=-21.15 EndY=21.15 EndZ=0
  constraints (11):
    c: Coincident(g0,g1)
    c: Coincident(g1,g2)
    c: Coincident(g2,g3)
    c: Coincident(g3,g0)
    c: Horizontal(g0)
    c: Horizontal(g2)
    c: Vertical(g1)
    c: Vertical(g3)
    c: Symmetric(g0,g1,g-1)
    c: DistanceX(g0,g0) = 42.3
    c: Equal(g0,g3)
FEATURE [PartDesign::Pad] Pad037
  Length = 9.6
  Length2 = 100
  Profile = -> Sketch099
  Refine = true
  Type = 0
FEATURE [Sketcher::SketchObject] Sketch100
  MapMode = 5
  Support = -> [XY_Plane042]
  sketch-geometry (4):
    g0: LineSegment StartX=-21 StartY=21 StartZ=0 EndX=21 EndY=21 EndZ=0
    g1: LineSegment StartX=21 StartY=21 StartZ=0 EndX=21 EndY=-21 EndZ=0
    g2: LineSegment StartX=21 StartY=-21 StartZ=0 EndX=-21 EndY=-21 EndZ=0
    g3: LineSegment StartX=-21 StartY=-21 StartZ=0 EndX=-21 EndY=21 EndZ=0
  constraints (11):
    c: Coincident(g0,g1)
    c: Coincident(g1,g2)
    c: Coincident(g2,g3)
    c: Coincident(g3,g0)
    c: Horizontal(g0)
    c: Horizontal(g2)
    c: Vertical(g1)
    c: Vertical(g3)
    c: DistanceX(g0,g0) = 42
    c: Symmetric(g0,g1,g-1)
    c: Equal(g0,g3)
FEATURE [PartDesign::Pad] Pad039
  Length = 22.75
  Length2 = 100
  Profile = -> Sketch100
  Refine = true
  Type = 0
FEATURE [PartDesign::Chamfer] Chamfer017
  Base = -> Pad039 [Edge8,Edge1,Edge5,Edge2]
  BaseFeature = -> Pad039
  Size = 7.5
FEATURE [Sketcher::SketchObject] Sketch087
  MapMode = 5
  Placement = pos=(0,0,0) rot=(1,0,0;3.14159rad)
  Support = -> [Chamfer017]
  sketch-geometry (8):
    g0: LineSegment [constr] StartX=-15.5 StartY=15.5 StartZ=0 EndX=15.5 EndY=15.5 EndZ=0
    g1: LineSegment [constr] StartX=15.5 StartY=15.5 StartZ=0 EndX=15.5 EndY=-15.5 EndZ=0
    g2: LineSegment [constr] StartX=15.5 StartY=-15.5 StartZ=0 EndX=-15.5 EndY=-15.5 EndZ=0
    g3: LineSegment [constr] StartX=-15.5 StartY=-15.5 StartZ=0 EndX=-15.5 EndY=15.5 EndZ=0
    g4: Circle CenterX=-15.5 CenterY=15.5 CenterZ=0 NormalX=0 NormalY=0 NormalZ=1 AngleXU=0 Radius=1.22
    g5: Circle CenterX=15.5 CenterY=15.5 CenterZ=0 NormalX=0 NormalY=0 NormalZ=1 AngleXU=0 Radius=1.22
    g6: Circle CenterX=15.5 CenterY=-15.5 CenterZ=0 NormalX=0 NormalY=0 NormalZ=1 AngleXU=0 Radius=1.22
    g7: Circle CenterX=-15.5 CenterY=-15.5 CenterZ=0 NormalX=0 NormalY=0 NormalZ=1 AngleXU=0 Radius=1.22
  constraints (19):
    c: Coincident(g0,g1)
    c: Coincident(g1,g2)
    c: Coincident(g2,g3)
    c: Coincident(g3,g0)
    c: Horizontal(g0)
    c: Horizontal(g2)
    c: Vertical(g1)
    c: Vertical(g3)
    c: Equal(g0,g3)
    c: Symmetric(g0,g1,g-1)
    c: DistanceX(g0,g0) = 31
    c: Coincident(g4,g0)
    c: Coincident(g5,g0)
    c: Coincident(g6,g1)
    c: Coincident(g7,g2)
    c: Equal(g6,g5)
    c: Equal(g5,g4)
    c: Equal(g4,g7)
    c: Radius(g4) = 1.22
FEATURE [PartDesign::Pocket] Pocket034
  BaseFeature = -> Chamfer017
  Length = 5
  Length2 = 100
  Profile = -> Sketch087
  Refine = true
  Type = 1
FEATURE [Sketcher::SketchObject] Sketch093
  MapMode = 5
  Placement = pos=(0,0,22.75) rot=(0,0,1;0rad)
  Support = -> [Pocket034]
  sketch-geometry (1):
    g0: Circle CenterX=0 CenterY=0 CenterZ=0 NormalX=0 NormalY=0 NormalZ=1 AngleXU=0 Radius=18
  constraints (2):
    c: Coincident(g0,g-1)
    c: Radius(g0) = 18
FEATURE [PartDesign::Pocket] Pocket037
  BaseFeature = -> Pocket034
  Length = 5
  Length2 = 100
  Profile = -> Sketch093
  Refine = true
  Type = 1
FEATURE [PartDesign::Body] Body025
  Group = -> [Sketch100,Pad039,Chamfer017,Sketch087,Pocket034,Sketch093,Pocket037]
  Origin = -> Origin043
  Placement = pos=(0,0,9.6) rot=(0,0,1;0rad)
  Tip = -> Pocket037
FEATURE [App::Part] Part026  label="Body024"
  Group = -> [Body025,Body026]
  Origin = -> Origin051
FEATURE [Sketcher::SketchObject] Sketch102
  MapMode = 5
  Placement = pos=(0,0,60) rot=(0,0,1;0rad)
  Support = -> [Pad038]
  sketch-geometry (4):
    g0: LineSegment StartX=2 StartY=2 StartZ=0 EndX=6 EndY=2 EndZ=0
    g1: LineSegment StartX=6 StartY=2 StartZ=0 EndX=6 EndY=-2 EndZ=0
    g2: LineSegment StartX=6 StartY=-2 StartZ=0 EndX=2 EndY=-2 EndZ=0
    g3: LineSegment StartX=2 StartY=-2 StartZ=0 EndX=2 EndY=2 EndZ=0
  constraints (11):
    c: Coincident(g0,g1)
    c: Coincident(g1,g2)
    c: Coincident(g2,g3)
    c: Coincident(g3,g0)
    c: Horizontal(g0)
    c: Horizontal(g2)
    c: Vertical(g1)
    c: Symmetric(g2,g0,g-1)
    c: DistanceX(g-1,g0) = 2
    c: Equal(g0,g3)
    c: DistanceX(g0,g0) = 4
FEATURE [PartDesign::Pocket] Pocket033
  BaseFeature = -> Pad038
  Length = 16
  Length2 = 100
  Profile = -> Sketch102
  Refine = true
  Type = 0
FEATURE [PartDesign::Chamfer] Chamfer019
  Base = -> Pocket033 [Edge3,Edge5,Edge9]
  BaseFeature = -> Pocket033
  Size = 0.3
FEATURE [PartDesign::Body] Body021  label="Rotor006"
  Group = -> [Sketch089,Pad038,Sketch102,Pocket033,Chamfer019]
  Origin = -> Origin044
  Placement = pos=(0,0,2) rot=(0,0,1;0rad)
  Tip = -> Chamfer019
FEATURE [App::Part] Part025  label="Rotor007"
  Group = -> [Body021]
  Origin = -> Origin052
FEATURE [Sketcher::SketchObject] Sketch103
  MapMode = 5
  Support = -> [XY_Plane053]
  sketch-geometry (4):
    g0: LineSegment StartX=-21.15 StartY=21.15 StartZ=0 EndX=21.15 EndY=21.15 EndZ=0
    g1: LineSegment StartX=21.15 StartY=21.15 StartZ=0 EndX=21.15 EndY=-21.15 EndZ=0
    g2: LineSegment StartX=21.15 StartY=-21.15 StartZ=0 EndX=-21.15 EndY=-21.15 EndZ=0
    g3: LineSegment StartX=-21.15 StartY=-21.15 StartZ=0 EndX=-21.15 EndY=21.15 EndZ=0
  constraints (11):
    c: Coincident(g0,g1)
    c: Coincident(g1,g2)
    c: Coincident(g2,g3)
    c: Coincident(g3,g0)
    c: Horizontal(g0)
    c: Horizontal(g2)
    c: Vertical(g1)
    c: Vertical(g3)
    c: Symmetric(g0,g1,g-1)
    c: DistanceX(g0,g0) = 42.3
    c: Equal(g0,g3)
FEATURE [PartDesign::Pad] Pad036
  Length = 7.75
  Length2 = 100
  Profile = -> Sketch103
  Refine = true
  Type = 0
FEATURE [PartDesign::Chamfer] Chamfer018
  Base = -> Pad036 [Edge8,Edge5,Edge2,Edge1]
  BaseFeature = -> Pad036
  Size = 5
FEATURE [PartDesign::Fillet] Fillet012
  Base = -> Chamfer018 [Edge22,Edge24,Edge23,Edge21,Edge12,Edge2,Edge3,Edge14]
  BaseFeature = -> Chamfer018
  Radius = 2
FEATURE [Sketcher::SketchObject] Sketch095
  MapMode = 5
  Placement = pos=(0,0,7.75) rot=(0,0,1;0rad)
  Support = -> [Fillet012]
  sketch-geometry (8):
    g0: LineSegment [constr] StartX=-15.5 StartY=15.5 StartZ=0 EndX=15.5 EndY=15.5 EndZ=0
    g1: LineSegment [constr] StartX=15.5 StartY=15.5 StartZ=0 EndX=15.5 EndY=-15.5 EndZ=0
    g2: LineSegment [constr] StartX=15.5 StartY=-15.5 StartZ=0 EndX=-15.5 EndY=-15.5 EndZ=0
    g3: LineSegment [constr] StartX=-15.5 StartY=-15.5 StartZ=0 EndX=-15.5 EndY=15.5 EndZ=0
    g4: Circle CenterX=-15.5 CenterY=15.5 CenterZ=0 NormalX=0 NormalY=0 NormalZ=1 AngleXU=0 Radius=1.225
    g5: Circle CenterX=15.5 CenterY=15.5 CenterZ=0 NormalX=0 NormalY=0 NormalZ=1 AngleXU=0 Radius=1.225
    g6: Circle CenterX=15.5 CenterY=-15.5 CenterZ=0 NormalX=0 NormalY=0 NormalZ=1 AngleXU=0 Radius=1.225
    g7: Circle CenterX=-15.5 CenterY=-15.5 CenterZ=0 NormalX=0 NormalY=0 NormalZ=1 AngleXU=0 Radius=1.225
  constraints (19):
    c: Coincident(g0,g1)
    c: Coincident(g1,g2)
    c: Coincident(g2,g3)
    c: Coincident(g3,g0)
    c: Horizontal(g0)
    c: Horizontal(g2)
    c: Vertical(g1)
    c: Vertical(g3)
    c: Equal(g0,g3)
    c: Symmetric(g0,g1,g-1)
    c: DistanceX(g0,g0) = 31
    c: Coincident(g4,g0)
    c: Coincident(g7,g2)
    c: Coincident(g0,g5)
    c: Coincident(g1,g6)
    c: Equal(g7,g4)
    c: Equal(g4,g5)
    c: Equal(g5,g6)
    c: Radius(g4) = 1.225
FEATURE [PartDesign::Pocket] Pocket036
  BaseFeature = -> Fillet012
  Length = 5
  Length2 = 100
  Profile = -> Sketch095
  Refine = true
  Type = 1
FEATURE [Sketcher::SketchObject] Sketch101
  MapMode = 5
  Placement = pos=(0,0,7.75) rot=(0,0,1;0rad)
  Support = -> [Pocket036]
  sketch-geometry (1):
    g0: Circle CenterX=0 CenterY=0 CenterZ=0 NormalX=0 NormalY=0 NormalZ=1 AngleXU=0 Radius=14
  constraints (2):
    c: Coincident(g0,g-1)
    c: Radius(g0) = 14
FEATURE [PartDesign::Pocket] Pocket039
  BaseFeature = -> Pocket036
  Length = 1
  Length2 = 100
  Profile = -> Sketch101
  Refine = true
  Type = 0
FEATURE [Sketcher::SketchObject] Sketch086
  MapMode = 5
  Placement = pos=(0,0,6.75) rot=(0,0,1;0rad)
  Support = -> [Pocket039]
  sketch-geometry (1):
    g0: Circle CenterX=0 CenterY=0 CenterZ=0 NormalX=0 NormalY=0 NormalZ=1 AngleXU=0 Radius=11
  constraints (2):
    c: Coincident(g0,g-1)
    c: Radius(g0) = 11
FEATURE [PartDesign::Pad] Pad041
  BaseFeature = -> Pocket039
  Length = 3
  Length2 = 100
  Profile = -> Sketch086
  Refine = true
  Type = 0
FEATURE [PartDesign::Draft] Draft003
  Angle = 10
  Base = -> Pad041 [Face25]
  BaseFeature = -> Pad041
  NeutralPlane = -> Pad041 [Face24]
FEATURE [Sketcher::SketchObject] Sketch098
  MapMode = 5
  Placement = pos=(0,0,9.75) rot=(0,0,1;0rad)
  Support = -> [Draft003]
  sketch-geometry (1):
    g0: Circle CenterX=0 CenterY=0 CenterZ=0 NormalX=0 NormalY=0 NormalZ=1 AngleXU=0 Radius=5
  constraints (2):
    c: Coincident(g0,g-1)
    c: Radius(g0) = 5
FEATURE [PartDesign::Pocket] Pocket038
  BaseFeature = -> Draft003
  Length = 8
  Length2 = 100
  Profile = -> Sketch098
  Refine = true
  Type = 1
FEATURE [Sketcher::SketchObject] Sketch092
  MapMode = 5
  Placement = pos=(0,0,0) rot=(1,0,0;3.14159rad)
  Support = -> [Pocket038]
  sketch-geometry (1):
    g0: Circle CenterX=0 CenterY=0 CenterZ=0 NormalX=0 NormalY=0 NormalZ=1 AngleXU=0 Radius=15.35
  constraints (2):
    c: Coincident(g0,g-1)
    c: Radius(g0) = 15.35
FEATURE [PartDesign::Pocket] Pocket042
  BaseFeature = -> Pocket038
  Length = 5
  Length2 = 100
  Profile = -> Sketch092
  Refine = true
  Type = 0
FEATURE [PartDesign::Body] Body022  label="Aluminum front006"
  Group = -> [Sketch103,Pad036,Chamfer018,Fillet012,Sketch095,Pocket036,Sketch101,Pocket039,Sketch086,Pad041,Draft003,Sketch098,Pocket038,Sketch092,Pocket042]
  Origin = -> Origin042
  Placement = pos=(0,0,32.35) rot=(0,0,1;0rad)
  Tip = -> Pocket042
FEATURE [App::Part] Part022  label="Aluminum front007"
  Group = -> [Body022]
  Origin = -> Origin048
FEATURE [Sketcher::SketchObject] Sketch104
  ExternalGeometry = -> [Pad037]
  MapMode = 5
  Support = -> [XY_Plane055]
  sketch-geometry (4):
    g0: LineSegment StartX=21.15 StartY=8.2 StartZ=0 EndX=25.45 EndY=8.2 EndZ=0
    g1: LineSegment StartX=25.45 StartY=8.2 StartZ=0 EndX=25.45 EndY=-8.2 EndZ=0
    g2: LineSegment StartX=25.45 StartY=-8.2 StartZ=0 EndX=21.15 EndY=-8.2 EndZ=0
    g3: LineSegment StartX=21.15 StartY=-8.2 StartZ=0 EndX=21.15 EndY=8.2 EndZ=0
  constraints (11):
    c: Coincident(g0,g1)
    c: Coincident(g1,g2)
    c: Coincident(g2,g3)
    c: Coincident(g3,g0)
    c: Horizontal(g0)
    c: Horizontal(g2)
    c: Vertical(g3)
    c: PointOnObject(g0,g-3)
    c: Symmetric(g1,g0,g-1)
    c: DistanceX(g0,g0) = 4.3
    c: DistanceY(g1,g1) = 16.4
FEATURE [PartDesign::Pad] Pad035
  BaseFeature = -> Pad037
  Length = 3.6
  Length2 = 100
  Profile = -> Sketch104
  Refine = true
  Type = 0
FEATURE [PartDesign::Chamfer] Chamfer020
  Base = -> Pad035 [Edge13,Edge5,Edge1,Edge2]
  BaseFeature = -> Pad035
  Size = 5
FEATURE [PartDesign::Fillet] Fillet011
  Base = -> Chamfer020 [Edge33,Edge28,Edge18,Edge3,Edge2,Edge16,Edge30,Edge25]
  BaseFeature = -> Chamfer020
  Radius = 2
FEATURE [Sketcher::SketchObject] Sketch084
  MapMode = 5
  Placement = pos=(0,0,0) rot=(1,0,0;3.14159rad)
  Support = -> [Fillet011]
  sketch-geometry (8):
    g0: LineSegment [constr] StartX=-15.5 StartY=15.5 StartZ=0 EndX=15.5 EndY=15.5 EndZ=0
    g1: LineSegment [constr] StartX=15.5 StartY=15.5 StartZ=0 EndX=15.5 EndY=-15.5 EndZ=0
    g2: LineSegment [constr] StartX=15.5 StartY=-15.5 StartZ=0 EndX=-15.5 EndY=-15.5 EndZ=0
    g3: LineSegment [constr] StartX=-15.5 StartY=-15.5 StartZ=0 EndX=-15.5 EndY=15.5 EndZ=0
    g4: Circle CenterX=-15.5 CenterY=15.5 CenterZ=0 NormalX=0 NormalY=0 NormalZ=1 AngleXU=0 Radius=1.225
    g5: Circle CenterX=15.5 CenterY=15.5 CenterZ=0 NormalX=0 NormalY=0 NormalZ=1 AngleXU=0 Radius=1.225
    g6: Circle CenterX=15.5 CenterY=-15.5 CenterZ=0 NormalX=0 NormalY=0 NormalZ=1 AngleXU=0 Radius=1.225
    g7: Circle CenterX=-15.5 CenterY=-15.5 CenterZ=0 NormalX=0 NormalY=0 NormalZ=1 AngleXU=0 Radius=1.225
  constraints (19):
    c: Coincident(g0,g1)
    c: Coincident(g1,g2)
    c: Coincident(g2,g3)
    c: Coincident(g3,g0)
    c: Horizontal(g0)
    c: Horizontal(g2)
    c: Vertical(g1)
    c: Vertical(g3)
    c: Symmetric(g0,g1,g-1)
    c: DistanceX(g0,g0) = 31
    c: Equal(g3,g0)
    c: Coincident(g4,g0)
    c: Coincident(g5,g0)
    c: Coincident(g6,g1)
    c: Coincident(g7,g2)
    c: Equal(g6,g5)
    c: Equal(g5,g4)
    c: Equal(g4,g7)
    c: Radius(g4) = 1.225
FEATURE [PartDesign::Hole] Hole003
  BaseFeature = -> Fillet011
  Depth = 25
  DepthType = 0
  Diameter = 3
  DrillPoint = 1
  DrillPointAngle = 118
  HoleCutCountersinkAngle = 90
  HoleCutDepth = 5
  HoleCutDiameter = 5
  HoleCutType = 1
  ModelActualThread = false
  Profile = -> Sketch084
  Refine = true
  Tapered = false
  TaperedAngle = 90
  ThreadAngle = 0
  ThreadClass = 0
  ThreadCutOffInner = 0
  ThreadCutOffOuter = 0
  ThreadDirection = 0
  ThreadFit = 0
  ThreadPitch = 0
  ThreadSize = 0
  ThreadType = 0
  Threaded = false
FEATURE [Sketcher::SketchObject] Sketch097
  ExternalGeometry = -> [Hole003]
  MapMode = 5
  Placement = pos=(21.15,0,0) rot=(0.57735,0.57735,0.57735;2.0944rad)
  Support = -> [Hole003]
  sketch-geometry (4):
    g0: LineSegment StartX=-8.2 StartY=3.6 StartZ=0 EndX=8.2 EndY=3.6 EndZ=0
    g1: LineSegment StartX=8.2 StartY=3.6 StartZ=0 EndX=8.2 EndY=9.6 EndZ=0
    g2: LineSegment StartX=8.2 StartY=9.6 StartZ=0 EndX=-8.2 EndY=9.6 EndZ=0
    g3: LineSegment StartX=-8.2 StartY=9.6 StartZ=0 EndX=-8.2 EndY=3.6 EndZ=0
  constraints (10):
    c: Coincident(g0,g1)
    c: Coincident(g1,g2)
    c: Coincident(g2,g3)
    c: Coincident(g3,g0)
    c: Horizontal(g0)
    c: Vertical(g1)
    c: Vertical(g3)
    c: Coincident(g0,g-3)
    c: PointOnObject(g1,g-5)
    c: Symmetric(g2,g1,g-2)
FEATURE [PartDesign::Pocket] Pocket040
  BaseFeature = -> Hole003
  Length = 4
  Length2 = 100
  Profile = -> Sketch097
  Refine = true
  Type = 0
FEATURE [PartDesign::Body] Body024  label="Aluminium rear006"
  Group = -> [Sketch099,Pad037,Sketch104,Pad035,Chamfer020,Fillet011,Sketch084,Hole003,Sketch097,Pocket040]
  Origin = -> Origin054
  Tip = -> Pocket040
FEATURE [App::Part] Part023  label="Aluminium rear007"
  Group = -> [Body024]
  Origin = -> Origin049
FEATURE [App::Part] Part027  label="Nema 019"
  Group = -> [Part023,Part026,Part022,Part025,Part024,Part021]
  Origin = -> Origin055
  Placement = pos=(669,306,51) rot=(0,0,1;0rad)
FEATURE [Part::Fuse] Fusion040  label="Sujetacamas izq 003"
  Base = -> Fusion039
  Placement = pos=(0,345,0) rot=(0,0,1;0rad)
  Tool = -> Fusion038
FEATURE [Part::Fuse] Fusion042  label="Sujetacamas iz001"
  Base = -> Fusion041
  Placement = pos=(726,605,0) rot=(0,0,1;3.14159rad)
  Tool = -> Fusion040
FEATURE [Part::Cut] Cut037  label="Z_axis_LM12UU_nut005"
  Base = -> Cut039
  Tool = -> Cylinder037
FEATURE [Part::Cylinder] Cylinder035  label="Cilindro019"
  Angle = 360
  AttacherType = Attacher::AttachEngine3D
  Height = 80
  Placement = pos=(0,-2,14) rot=(-1,0,0;1.5708rad)
  Radius = 7
FEATURE [Part::Cut] Cut034  label="Z_axis_LM12UU_nut004"
  Base = -> Cut036
  Tool = -> Cylinder036
FEATURE [Part::Cut] Cut032
  Base = -> Cut033
  Tool = -> Cylinder039
FEATURE [Part::Cylinder] Cylinder034  label="Cilindro018"
  Angle = 360
  AttacherType = Attacher::AttachEngine3D
  Height = 80
  Placement = pos=(0,-2,14) rot=(-1,0,0;1.5708rad)
  Radius = 7
FEATURE [Part::Cylinder] Cylinder040  label="Cilindro023"
  Angle = 360
  AttacherType = Attacher::AttachEngine3D
  Height = 10
  Placement = pos=(17,7,7) rot=(1,0,0;1.5708rad)
  Radius = 2
FEATURE [Part::Cut] Cut038  label="CoreXY_Z_Axix_LM12UU_Nut A002"
  Base = -> Cut037
  Placement = pos=(24,305,330) rot=(0.57735,-0.57735,0.57735;4.18879rad)
  Tool = -> Cylinder035
FEATURE [Part::Cut] Cut035  label="CoreXY_Z_Axix_LM12UU_Nut B002"
  Base = -> Cut034
  Placement = pos=(53,305,330) rot=(0.57735,0.57735,-0.57735;4.18879rad)
  Tool = -> Cylinder034
FEATURE [Part::Cylinder] Cylinder038  label="Tornillo sin fin002"
  Angle = 360
  AttacherType = Attacher::AttachEngine3D
  Height = 510
  Placement = pos=(40,130,90) rot=(0,0,1;0rad)
  Radius = 5
FEATURE [Part::Cut] Cut031  label="Sujección barilla eje zZ001"
  Base = -> Cut032
  Placement = pos=(32,135,95) rot=(0,0,-1;1.5708rad)
  Tool = -> Cylinder040
FEATURE [Part::Fuse] Fusion032  label="sujetacamas izquierdo001"
  Base = -> Cut038
  Placement = pos=(0,-174,0) rot=(0,0,1;0rad)
  Tool = -> Cut035
FEATURE [Part::Fuse] Fusion031  label="Barra sujeeción 002"
  Base = -> Cylinder038
  Tool = -> Cut031
FEATURE [Part::Fuse] Fusion033  label="Sujetacamas izq 002"
  Base = -> Fusion032
  Placement = pos=(0,345,0) rot=(0,0,1;0rad)
  Tool = -> Fusion031
FEATURE [Part::Fuse] Fusion035  label="Sujetacamas iz"
  Base = -> Fusion030
  Tool = -> Fusion033
FEATURE [App::DocumentObjectGroup] Group  label="Eje Z"
  Group = -> [Fusion042,Fusion035,BooleanFragments002,Part019,Part027]
